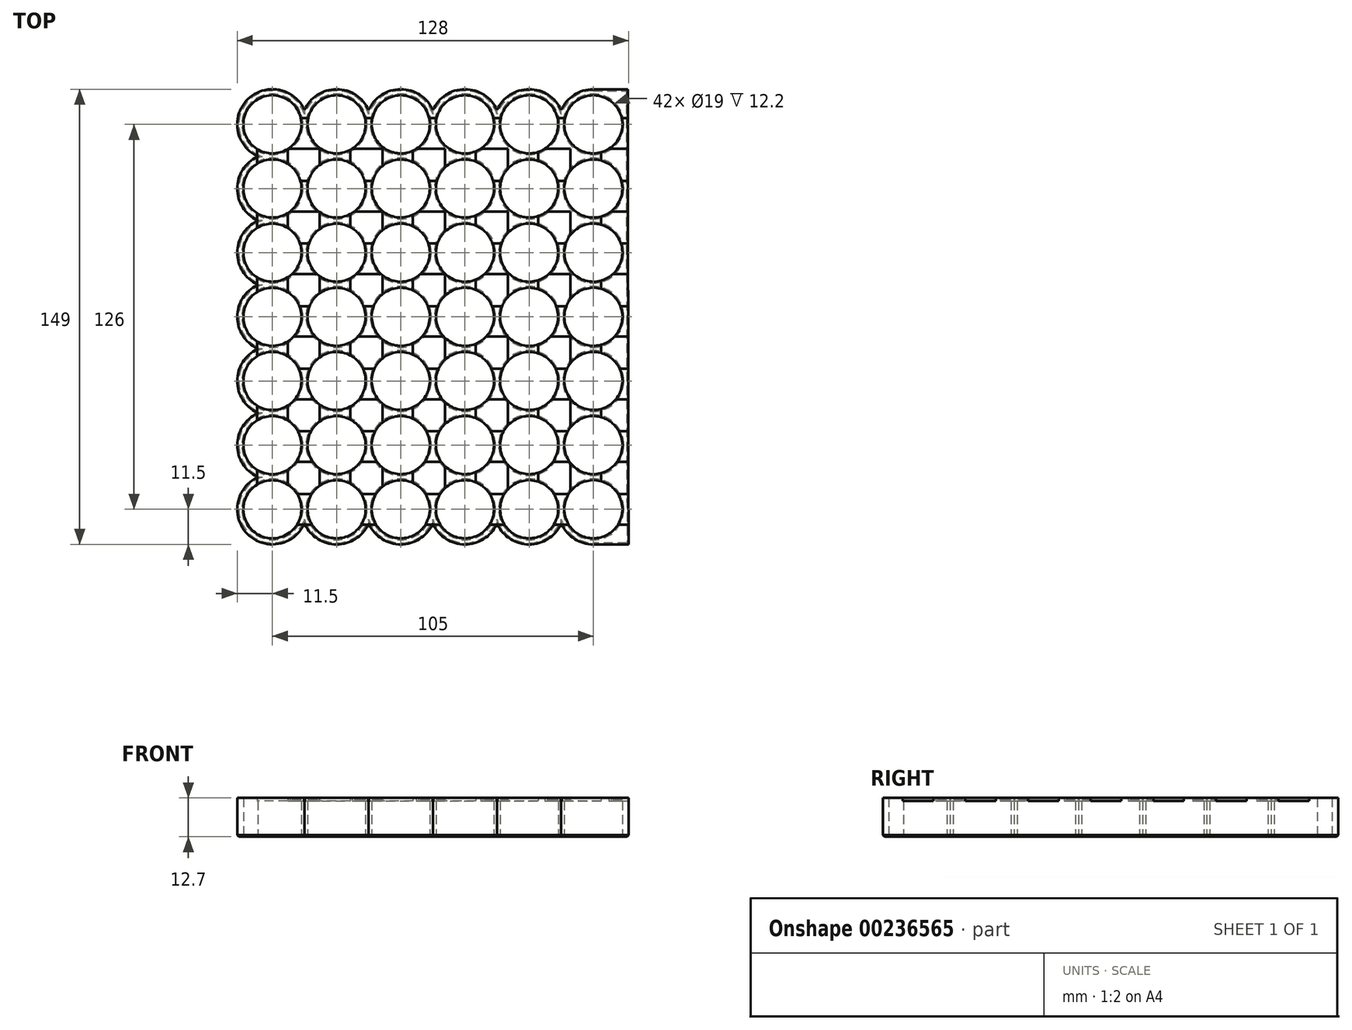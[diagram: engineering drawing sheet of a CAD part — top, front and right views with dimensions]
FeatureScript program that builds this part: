
annotation { "Feature Type Name" : "Feature", "Feature Type Description" : "" }
export const myFeature = defineFeature(function(context is Context, id is Id, definition is map)
    precondition{}
    {
        {
            var Q0;
            Q0=qCreatedBy(makeId("Top.planeOp"),FACE);
            var sketch = newSketch(context, id + "F0", { "sketchPlane" : qUnion([Q0])});
            skCircle(sketch, "E0", {"center": v(0, 0) * mm, "radius": 9.5 * mm});
            skCircle(sketch, "E1.0", {"center": v(0, 0) * mm, "radius": 11.5 * mm});
            skCircle(sketch, "E2.0.1.0", {"center": v(0, 21) * mm, "radius": 11.5 * mm});
            skCircle(sketch, "E2.0.1.1", {"center": v(0, 21) * mm, "radius": 9.5 * mm});
            skCircle(sketch, "E2.0.2.0", {"center": v(0, 42) * mm, "radius": 11.5 * mm});
            skCircle(sketch, "E2.0.2.1", {"center": v(0, 42) * mm, "radius": 9.5 * mm});
            skCircle(sketch, "E2.0.3.0", {"center": v(0, 63) * mm, "radius": 11.5 * mm});
            skCircle(sketch, "E2.0.3.1", {"center": v(0, 63) * mm, "radius": 9.5 * mm});
            skCircle(sketch, "E2.0.4.0", {"center": v(0, 84) * mm, "radius": 11.5 * mm});
            skCircle(sketch, "E2.0.4.1", {"center": v(0, 84) * mm, "radius": 9.5 * mm});
            skCircle(sketch, "E2.0.5.0", {"center": v(0, 105) * mm, "radius": 11.5 * mm});
            skCircle(sketch, "E2.0.5.1", {"center": v(0, 105) * mm, "radius": 9.5 * mm});
            skCircle(sketch, "E2.0.6.0", {"center": v(0, 126) * mm, "radius": 11.5 * mm});
            skCircle(sketch, "E2.0.6.1", {"center": v(0, 126) * mm, "radius": 9.5 * mm});
            skCircle(sketch, "E2.1.0.0", {"center": v(21, 0) * mm, "radius": 11.5 * mm});
            skCircle(sketch, "E2.1.0.1", {"center": v(21, 0) * mm, "radius": 9.5 * mm});
            skCircle(sketch, "E2.1.1.0", {"center": v(21, 21) * mm, "radius": 11.5 * mm});
            skCircle(sketch, "E2.1.1.1", {"center": v(21, 21) * mm, "radius": 9.5 * mm});
            skCircle(sketch, "E2.1.2.0", {"center": v(21, 42) * mm, "radius": 11.5 * mm});
            skCircle(sketch, "E2.1.2.1", {"center": v(21, 42) * mm, "radius": 9.5 * mm});
            skCircle(sketch, "E2.1.3.0", {"center": v(21, 63) * mm, "radius": 11.5 * mm});
            skCircle(sketch, "E2.1.3.1", {"center": v(21, 63) * mm, "radius": 9.5 * mm});
            skCircle(sketch, "E2.1.4.0", {"center": v(21, 84) * mm, "radius": 11.5 * mm});
            skCircle(sketch, "E2.1.4.1", {"center": v(21, 84) * mm, "radius": 9.5 * mm});
            skCircle(sketch, "E2.1.5.0", {"center": v(21, 105) * mm, "radius": 11.5 * mm});
            skCircle(sketch, "E2.1.5.1", {"center": v(21, 105) * mm, "radius": 9.5 * mm});
            skCircle(sketch, "E2.1.6.0", {"center": v(21, 126) * mm, "radius": 11.5 * mm});
            skCircle(sketch, "E2.1.6.1", {"center": v(21, 126) * mm, "radius": 9.5 * mm});
            skCircle(sketch, "E2.2.0.0", {"center": v(42, 0) * mm, "radius": 11.5 * mm});
            skCircle(sketch, "E2.2.0.1", {"center": v(42, 0) * mm, "radius": 9.5 * mm});
            skCircle(sketch, "E2.2.1.0", {"center": v(42, 21) * mm, "radius": 11.5 * mm});
            skCircle(sketch, "E2.2.1.1", {"center": v(42, 21) * mm, "radius": 9.5 * mm});
            skCircle(sketch, "E2.2.2.0", {"center": v(42, 42) * mm, "radius": 11.5 * mm});
            skCircle(sketch, "E2.2.2.1", {"center": v(42, 42) * mm, "radius": 9.5 * mm});
            skCircle(sketch, "E2.2.3.0", {"center": v(42, 63) * mm, "radius": 11.5 * mm});
            skCircle(sketch, "E2.2.3.1", {"center": v(42, 63) * mm, "radius": 9.5 * mm});
            skCircle(sketch, "E2.2.4.0", {"center": v(42, 84) * mm, "radius": 11.5 * mm});
            skCircle(sketch, "E2.2.4.1", {"center": v(42, 84) * mm, "radius": 9.5 * mm});
            skCircle(sketch, "E2.2.5.0", {"center": v(42, 105) * mm, "radius": 11.5 * mm});
            skCircle(sketch, "E2.2.5.1", {"center": v(42, 105) * mm, "radius": 9.5 * mm});
            skCircle(sketch, "E2.2.6.0", {"center": v(42, 126) * mm, "radius": 11.5 * mm});
            skCircle(sketch, "E2.2.6.1", {"center": v(42, 126) * mm, "radius": 9.5 * mm});
            skCircle(sketch, "E2.3.0.0", {"center": v(63, 0) * mm, "radius": 11.5 * mm});
            skCircle(sketch, "E2.3.0.1", {"center": v(63, 0) * mm, "radius": 9.5 * mm});
            skCircle(sketch, "E2.3.1.0", {"center": v(63, 21) * mm, "radius": 11.5 * mm});
            skCircle(sketch, "E2.3.1.1", {"center": v(63, 21) * mm, "radius": 9.5 * mm});
            skCircle(sketch, "E2.3.2.0", {"center": v(63, 42) * mm, "radius": 11.5 * mm});
            skCircle(sketch, "E2.3.2.1", {"center": v(63, 42) * mm, "radius": 9.5 * mm});
            skCircle(sketch, "E2.3.3.0", {"center": v(63, 63) * mm, "radius": 11.5 * mm});
            skCircle(sketch, "E2.3.3.1", {"center": v(63, 63) * mm, "radius": 9.5 * mm});
            skCircle(sketch, "E2.3.4.0", {"center": v(63, 84) * mm, "radius": 11.5 * mm});
            skCircle(sketch, "E2.3.4.1", {"center": v(63, 84) * mm, "radius": 9.5 * mm});
            skCircle(sketch, "E2.3.5.0", {"center": v(63, 105) * mm, "radius": 11.5 * mm});
            skCircle(sketch, "E2.3.5.1", {"center": v(63, 105) * mm, "radius": 9.5 * mm});
            skCircle(sketch, "E2.3.6.0", {"center": v(63, 126) * mm, "radius": 11.5 * mm});
            skCircle(sketch, "E2.3.6.1", {"center": v(63, 126) * mm, "radius": 9.5 * mm});
            skCircle(sketch, "E2.4.0.0", {"center": v(84, 0) * mm, "radius": 11.5 * mm});
            skCircle(sketch, "E2.4.0.1", {"center": v(84, 0) * mm, "radius": 9.5 * mm});
            skCircle(sketch, "E2.4.1.0", {"center": v(84, 21) * mm, "radius": 11.5 * mm});
            skCircle(sketch, "E2.4.1.1", {"center": v(84, 21) * mm, "radius": 9.5 * mm});
            skCircle(sketch, "E2.4.2.0", {"center": v(84, 42) * mm, "radius": 11.5 * mm});
            skCircle(sketch, "E2.4.2.1", {"center": v(84, 42) * mm, "radius": 9.5 * mm});
            skCircle(sketch, "E2.4.3.0", {"center": v(84, 63) * mm, "radius": 11.5 * mm});
            skCircle(sketch, "E2.4.3.1", {"center": v(84, 63) * mm, "radius": 9.5 * mm});
            skCircle(sketch, "E2.4.4.0", {"center": v(84, 84) * mm, "radius": 11.5 * mm});
            skCircle(sketch, "E2.4.4.1", {"center": v(84, 84) * mm, "radius": 9.5 * mm});
            skCircle(sketch, "E2.4.5.0", {"center": v(84, 105) * mm, "radius": 11.5 * mm});
            skCircle(sketch, "E2.4.5.1", {"center": v(84, 105) * mm, "radius": 9.5 * mm});
            skCircle(sketch, "E2.4.6.0", {"center": v(84, 126) * mm, "radius": 11.5 * mm});
            skCircle(sketch, "E2.4.6.1", {"center": v(84, 126) * mm, "radius": 9.5 * mm});
            skCircle(sketch, "E2.5.0.0", {"center": v(105, 0) * mm, "radius": 11.5 * mm});
            skCircle(sketch, "E2.5.0.1", {"center": v(105, 0) * mm, "radius": 9.5 * mm});
            skCircle(sketch, "E2.5.1.0", {"center": v(105, 21) * mm, "radius": 11.5 * mm});
            skCircle(sketch, "E2.5.1.1", {"center": v(105, 21) * mm, "radius": 9.5 * mm});
            skCircle(sketch, "E2.5.2.0", {"center": v(105, 42) * mm, "radius": 11.5 * mm});
            skCircle(sketch, "E2.5.2.1", {"center": v(105, 42) * mm, "radius": 9.5 * mm});
            skCircle(sketch, "E2.5.3.0", {"center": v(105, 63) * mm, "radius": 11.5 * mm});
            skCircle(sketch, "E2.5.3.1", {"center": v(105, 63) * mm, "radius": 9.5 * mm});
            skCircle(sketch, "E2.5.4.0", {"center": v(105, 84) * mm, "radius": 11.5 * mm});
            skCircle(sketch, "E2.5.4.1", {"center": v(105, 84) * mm, "radius": 9.5 * mm});
            skCircle(sketch, "E2.5.5.0", {"center": v(105, 105) * mm, "radius": 11.5 * mm});
            skCircle(sketch, "E2.5.5.1", {"center": v(105, 105) * mm, "radius": 9.5 * mm});
            skCircle(sketch, "E2.5.6.0", {"center": v(105, 126) * mm, "radius": 11.5 * mm});
            skCircle(sketch, "E2.5.6.1", {"center": v(105, 126) * mm, "radius": 9.5 * mm});
            skLineSegment(sketch, "E2.direction1", {"start": v(0, 0) * mm, "end": v(21, 0) * mm, "construction": true});
            skLineSegment(sketch, "E2.direction2", {"start": v(0, 0) * mm, "end": v(0, 21) * mm, "construction": true});
            skLineSegment(sketch, "E3", {"start": v(105, 0) * mm, "end": v(105, -11.5) * mm, "construction": true});
            skLineSegment(sketch, "E4", {"start": v(105, -11.5) * mm, "end": v(116.5, -11.5) * mm});
            skLineSegment(sketch, "E5", {"start": v(105, 126) * mm, "end": v(105, 137.5) * mm, "construction": true});
            skLineSegment(sketch, "E6", {"start": v(105, 137.5) * mm, "end": v(116.25, 137.5) * mm});
            skLineSegment(sketch, "E7", {"start": v(116.25, 137.5) * mm, "end": v(116.5, -11.5) * mm});
            skSolve(sketch);
        }
        {
            var Q0;
            {var subQ0=sQuery(id+"F0.wireOp",EDGE,"E2.10.4.0");var subQ1=sQuery(id+"F0.wireOp",EDGE,"E2.10.3.0");var subQ2=makeQuery(id+"F0.imprint","INTERSECT",VERTEX,{"disambiguationData":[OD(0.0)],"derivedFrom":[subQ1,subQ0]});Q0=makeQuery(id+"F0.imprint","IMPRINT",FACE,{"disambiguationData":[TD([[makeQuery(id+"F0.imprint","IMPRINT",EDGE,{"disambiguationData":[TD([[subQ2,-1.0]])],"derivedFrom":subQ1}),1.0]])]});}
            var Q1;
            {var subQ0=sQuery(id+"F0.wireOp",EDGE,"E2.1.5.0");var subQ1=sQuery(id+"F0.wireOp",EDGE,"E2.0.5.0");var subQ2=makeQuery(id+"F0.imprint","INTERSECT",VERTEX,{"disambiguationData":[OD(0.0)],"derivedFrom":[subQ1,subQ0]});Q1=makeQuery(id+"F0.imprint","IMPRINT",FACE,{"disambiguationData":[TD([[makeQuery(id+"F0.imprint","IMPRINT",EDGE,{"disambiguationData":[TD([[subQ2,-1.0]])],"derivedFrom":subQ1}),-1.0]])]});}
            var Q2;
            {var subQ0=sQuery(id+"F0.wireOp",EDGE,"E2.0.1.0");var subQ1=sQuery(id+"F0.wireOp",EDGE,"E1.0");var subQ2=makeQuery(id+"F0.imprint","INTERSECT",VERTEX,{"disambiguationData":[OD(1.0)],"derivedFrom":[subQ1,subQ0]});Q2=makeQuery(id+"F0.imprint","IMPRINT",FACE,{"disambiguationData":[TD([[makeQuery(id+"F0.imprint","IMPRINT",EDGE,{"disambiguationData":[TD([[subQ2,-1.0]])],"derivedFrom":subQ1}),-1.0]])]});}
            var Q3;
            {var subQ0=sQuery(id+"F0.wireOp",EDGE,"E2.2.3.0");var subQ1=sQuery(id+"F0.wireOp",EDGE,"E2.1.3.0");var subQ2=makeQuery(id+"F0.imprint","INTERSECT",VERTEX,{"disambiguationData":[OD(0.0)],"derivedFrom":[subQ1,subQ0]});Q3=makeQuery(id+"F0.imprint","IMPRINT",FACE,{"disambiguationData":[TD([[makeQuery(id+"F0.imprint","IMPRINT",EDGE,{"disambiguationData":[TD([[subQ2,-1.0]])],"derivedFrom":subQ1}),-1.0]])]});}
            var Q4;
            {var subQ0=sQuery(id+"F0.wireOp",EDGE,"E2.2.5.0");var subQ1=sQuery(id+"F0.wireOp",EDGE,"E2.1.5.0");var subQ2=makeQuery(id+"F0.imprint","INTERSECT",VERTEX,{"disambiguationData":[OD(0.0)],"derivedFrom":[subQ1,subQ0]});Q4=makeQuery(id+"F0.imprint","IMPRINT",FACE,{"disambiguationData":[TD([[makeQuery(id+"F0.imprint","IMPRINT",EDGE,{"disambiguationData":[TD([[subQ2,-1.0]])],"derivedFrom":subQ1}),-1.0]])]});}
            var Q5;
            {var subQ0=sQuery(id+"F0.wireOp",EDGE,"E2.3.1.0");var subQ1=sQuery(id+"F0.wireOp",EDGE,"E2.2.1.0");var subQ2=makeQuery(id+"F0.imprint","INTERSECT",VERTEX,{"disambiguationData":[OD(0.0)],"derivedFrom":[subQ1,subQ0]});Q5=makeQuery(id+"F0.imprint","IMPRINT",FACE,{"disambiguationData":[TD([[makeQuery(id+"F0.imprint","IMPRINT",EDGE,{"disambiguationData":[TD([[subQ2,-1.0]])],"derivedFrom":subQ1}),-1.0]])]});}
            var Q6;
            {var subQ0=sQuery(id+"F0.wireOp",EDGE,"E2.3.3.0");var subQ1=sQuery(id+"F0.wireOp",EDGE,"E2.2.3.0");var subQ2=makeQuery(id+"F0.imprint","INTERSECT",VERTEX,{"disambiguationData":[OD(0.0)],"derivedFrom":[subQ1,subQ0]});Q6=makeQuery(id+"F0.imprint","IMPRINT",FACE,{"disambiguationData":[TD([[makeQuery(id+"F0.imprint","IMPRINT",EDGE,{"disambiguationData":[TD([[subQ2,-1.0]])],"derivedFrom":subQ1}),-1.0]])]});}
            var Q7;
            {var subQ0=sQuery(id+"F0.wireOp",EDGE,"E2.1.3.0");var subQ1=sQuery(id+"F0.wireOp",EDGE,"E2.0.3.0");var subQ2=makeQuery(id+"F0.imprint","INTERSECT",VERTEX,{"disambiguationData":[OD(0.0)],"derivedFrom":[subQ1,subQ0]});Q7=makeQuery(id+"F0.imprint","IMPRINT",FACE,{"disambiguationData":[TD([[makeQuery(id+"F0.imprint","IMPRINT",EDGE,{"disambiguationData":[TD([[subQ2,1.0]])],"derivedFrom":subQ1}),1.0]])]});}
            var Q8;
            {var subQ0=sQuery(id+"F0.wireOp",EDGE,"E2.2.1.0");var subQ1=sQuery(id+"F0.wireOp",EDGE,"E2.1.1.0");var subQ2=makeQuery(id+"F0.imprint","INTERSECT",VERTEX,{"disambiguationData":[OD(0.0)],"derivedFrom":[subQ1,subQ0]});Q8=makeQuery(id+"F0.imprint","IMPRINT",FACE,{"disambiguationData":[TD([[makeQuery(id+"F0.imprint","IMPRINT",EDGE,{"disambiguationData":[TD([[subQ2,-1.0]])],"derivedFrom":subQ1}),-1.0]])]});}
            var Q9;
            {var subQ0=sQuery(id+"F0.wireOp",EDGE,"E2.7.6.0");var subQ1=sQuery(id+"F0.wireOp",EDGE,"E2.6.6.0");var subQ2=makeQuery(id+"F0.imprint","INTERSECT",VERTEX,{"disambiguationData":[OD(0.0)],"derivedFrom":[subQ1,subQ0]});Q9=makeQuery(id+"F0.imprint","IMPRINT",FACE,{"disambiguationData":[TD([[makeQuery(id+"F0.imprint","IMPRINT",EDGE,{"disambiguationData":[TD([[subQ2,1.0]])],"derivedFrom":subQ1}),-1.0]])]});}
            var Q10;
            {var subQ0=sQuery(id+"F0.wireOp",EDGE,"E2.11.6.0");var subQ1=sQuery(id+"F0.wireOp",EDGE,"E2.10.6.0");var subQ2=makeQuery(id+"F0.imprint","INTERSECT",VERTEX,{"disambiguationData":[OD(0.0)],"derivedFrom":[subQ1,subQ0]});Q10=makeQuery(id+"F0.imprint","IMPRINT",FACE,{"disambiguationData":[TD([[makeQuery(id+"F0.imprint","IMPRINT",EDGE,{"disambiguationData":[TD([[subQ2,1.0]])],"derivedFrom":subQ1}),-1.0]])]});}
            var Q11;
            {var subQ0=sQuery(id+"F0.wireOp",EDGE,"E2.11.3.0");var subQ1=sQuery(id+"F0.wireOp",EDGE,"E2.10.3.0");var subQ2=makeQuery(id+"F0.imprint","INTERSECT",VERTEX,{"disambiguationData":[OD(0.0)],"derivedFrom":[subQ1,subQ0]});Q11=makeQuery(id+"F0.imprint","IMPRINT",FACE,{"disambiguationData":[TD([[makeQuery(id+"F0.imprint","IMPRINT",EDGE,{"disambiguationData":[TD([[subQ2,-1.0]])],"derivedFrom":subQ1}),-1.0]])]});}
            var Q12;
            {var subQ0=sQuery(id+"F0.wireOp",EDGE,"E2.11.5.0");var subQ1=sQuery(id+"F0.wireOp",EDGE,"E2.10.5.0");var subQ2=makeQuery(id+"F0.imprint","INTERSECT",VERTEX,{"disambiguationData":[OD(0.0)],"derivedFrom":[subQ1,subQ0]});Q12=makeQuery(id+"F0.imprint","IMPRINT",FACE,{"disambiguationData":[TD([[makeQuery(id+"F0.imprint","IMPRINT",EDGE,{"disambiguationData":[TD([[subQ2,-1.0]])],"derivedFrom":subQ1}),-1.0]])]});}
            var Q13;
            {var subQ0=sQuery(id+"F0.wireOp",EDGE,"E2.9.5.0");var subQ1=sQuery(id+"F0.wireOp",EDGE,"E2.8.5.0");var subQ2=makeQuery(id+"F0.imprint","INTERSECT",VERTEX,{"disambiguationData":[OD(0.0)],"derivedFrom":[subQ1,subQ0]});Q13=makeQuery(id+"F0.imprint","IMPRINT",FACE,{"disambiguationData":[TD([[makeQuery(id+"F0.imprint","IMPRINT",EDGE,{"disambiguationData":[TD([[subQ2,-1.0]])],"derivedFrom":subQ1}),-1.0]])]});}
            var Q14;
            {var subQ0=sQuery(id+"F0.wireOp",EDGE,"E2.10.1.0");var subQ1=sQuery(id+"F0.wireOp",EDGE,"E2.9.1.0");var subQ2=makeQuery(id+"F0.imprint","INTERSECT",VERTEX,{"disambiguationData":[OD(0.0)],"derivedFrom":[subQ1,subQ0]});Q14=makeQuery(id+"F0.imprint","IMPRINT",FACE,{"disambiguationData":[TD([[makeQuery(id+"F0.imprint","IMPRINT",EDGE,{"disambiguationData":[TD([[subQ2,-1.0]])],"derivedFrom":subQ1}),-1.0]])]});}
            var Q15;
            {var subQ0=sQuery(id+"F0.wireOp",EDGE,"E2.10.3.0");var subQ1=sQuery(id+"F0.wireOp",EDGE,"E2.9.3.0");var subQ2=makeQuery(id+"F0.imprint","INTERSECT",VERTEX,{"disambiguationData":[OD(0.0)],"derivedFrom":[subQ1,subQ0]});Q15=makeQuery(id+"F0.imprint","IMPRINT",FACE,{"disambiguationData":[TD([[makeQuery(id+"F0.imprint","IMPRINT",EDGE,{"disambiguationData":[TD([[subQ2,-1.0]])],"derivedFrom":subQ1}),-1.0]])]});}
            var Q16;
            {var subQ0=sQuery(id+"F0.wireOp",EDGE,"E2.10.5.0");var subQ1=sQuery(id+"F0.wireOp",EDGE,"E2.9.5.0");var subQ2=makeQuery(id+"F0.imprint","INTERSECT",VERTEX,{"disambiguationData":[OD(0.0)],"derivedFrom":[subQ1,subQ0]});Q16=makeQuery(id+"F0.imprint","IMPRINT",FACE,{"disambiguationData":[TD([[makeQuery(id+"F0.imprint","IMPRINT",EDGE,{"disambiguationData":[TD([[subQ2,-1.0]])],"derivedFrom":subQ1}),-1.0]])]});}
            var Q17;
            {var subQ0=sQuery(id+"F0.wireOp",EDGE,"E2.8.3.0");var subQ1=sQuery(id+"F0.wireOp",EDGE,"E2.7.3.0");var subQ2=makeQuery(id+"F0.imprint","INTERSECT",VERTEX,{"disambiguationData":[OD(0.0)],"derivedFrom":[subQ1,subQ0]});Q17=makeQuery(id+"F0.imprint","IMPRINT",FACE,{"disambiguationData":[TD([[makeQuery(id+"F0.imprint","IMPRINT",EDGE,{"disambiguationData":[TD([[subQ2,-1.0]])],"derivedFrom":subQ1}),-1.0]])]});}
            var Q18;
            {var subQ0=sQuery(id+"F0.wireOp",EDGE,"E2.8.5.0");var subQ1=sQuery(id+"F0.wireOp",EDGE,"E2.7.5.0");var subQ2=makeQuery(id+"F0.imprint","INTERSECT",VERTEX,{"disambiguationData":[OD(0.0)],"derivedFrom":[subQ1,subQ0]});Q18=makeQuery(id+"F0.imprint","IMPRINT",FACE,{"disambiguationData":[TD([[makeQuery(id+"F0.imprint","IMPRINT",EDGE,{"disambiguationData":[TD([[subQ2,-1.0]])],"derivedFrom":subQ1}),-1.0]])]});}
            var Q19;
            {var subQ0=sQuery(id+"F0.wireOp",EDGE,"E2.9.1.0");var subQ1=sQuery(id+"F0.wireOp",EDGE,"E2.8.1.0");var subQ2=makeQuery(id+"F0.imprint","INTERSECT",VERTEX,{"disambiguationData":[OD(0.0)],"derivedFrom":[subQ1,subQ0]});Q19=makeQuery(id+"F0.imprint","IMPRINT",FACE,{"disambiguationData":[TD([[makeQuery(id+"F0.imprint","IMPRINT",EDGE,{"disambiguationData":[TD([[subQ2,-1.0]])],"derivedFrom":subQ1}),-1.0]])]});}
            var Q20;
            {var subQ0=sQuery(id+"F0.wireOp",EDGE,"E2.9.3.0");var subQ1=sQuery(id+"F0.wireOp",EDGE,"E2.8.3.0");var subQ2=makeQuery(id+"F0.imprint","INTERSECT",VERTEX,{"disambiguationData":[OD(0.0)],"derivedFrom":[subQ1,subQ0]});Q20=makeQuery(id+"F0.imprint","IMPRINT",FACE,{"disambiguationData":[TD([[makeQuery(id+"F0.imprint","IMPRINT",EDGE,{"disambiguationData":[TD([[subQ2,-1.0]])],"derivedFrom":subQ1}),-1.0]])]});}
            var Q21;
            {var subQ0=sQuery(id+"F0.wireOp",EDGE,"E2.7.5.0");var subQ1=sQuery(id+"F0.wireOp",EDGE,"E2.6.5.0");var subQ2=makeQuery(id+"F0.imprint","INTERSECT",VERTEX,{"disambiguationData":[OD(0.0)],"derivedFrom":[subQ1,subQ0]});Q21=makeQuery(id+"F0.imprint","IMPRINT",FACE,{"disambiguationData":[TD([[makeQuery(id+"F0.imprint","IMPRINT",EDGE,{"disambiguationData":[TD([[subQ2,-1.0]])],"derivedFrom":subQ1}),-1.0]])]});}
            var Q22;
            {var subQ0=sQuery(id+"F0.wireOp",EDGE,"E2.8.1.0");var subQ1=sQuery(id+"F0.wireOp",EDGE,"E2.7.1.0");var subQ2=makeQuery(id+"F0.imprint","INTERSECT",VERTEX,{"disambiguationData":[OD(0.0)],"derivedFrom":[subQ1,subQ0]});Q22=makeQuery(id+"F0.imprint","IMPRINT",FACE,{"disambiguationData":[TD([[makeQuery(id+"F0.imprint","IMPRINT",EDGE,{"disambiguationData":[TD([[subQ2,-1.0]])],"derivedFrom":subQ1}),-1.0]])]});}
            var Q23;
            {var subQ0=sQuery(id+"F0.wireOp",EDGE,"E2.6.3.0");var subQ1=sQuery(id+"F0.wireOp",EDGE,"E2.5.3.0");var subQ2=makeQuery(id+"F0.imprint","INTERSECT",VERTEX,{"disambiguationData":[OD(0.0)],"derivedFrom":[subQ1,subQ0]});Q23=makeQuery(id+"F0.imprint","IMPRINT",FACE,{"disambiguationData":[TD([[makeQuery(id+"F0.imprint","IMPRINT",EDGE,{"disambiguationData":[TD([[subQ2,-1.0]])],"derivedFrom":subQ1}),-1.0]])]});}
            var Q24;
            {var subQ0=sQuery(id+"F0.wireOp",EDGE,"E2.6.5.0");var subQ1=sQuery(id+"F0.wireOp",EDGE,"E2.5.5.0");var subQ2=makeQuery(id+"F0.imprint","INTERSECT",VERTEX,{"disambiguationData":[OD(0.0)],"derivedFrom":[subQ1,subQ0]});Q24=makeQuery(id+"F0.imprint","IMPRINT",FACE,{"disambiguationData":[TD([[makeQuery(id+"F0.imprint","IMPRINT",EDGE,{"disambiguationData":[TD([[subQ2,-1.0]])],"derivedFrom":subQ1}),-1.0]])]});}
            var Q25;
            {var subQ0=sQuery(id+"F0.wireOp",EDGE,"E2.7.1.0");var subQ1=sQuery(id+"F0.wireOp",EDGE,"E2.6.1.0");var subQ2=makeQuery(id+"F0.imprint","INTERSECT",VERTEX,{"disambiguationData":[OD(0.0)],"derivedFrom":[subQ1,subQ0]});Q25=makeQuery(id+"F0.imprint","IMPRINT",FACE,{"disambiguationData":[TD([[makeQuery(id+"F0.imprint","IMPRINT",EDGE,{"disambiguationData":[TD([[subQ2,-1.0]])],"derivedFrom":subQ1}),-1.0]])]});}
            var Q26;
            {var subQ0=sQuery(id+"F0.wireOp",EDGE,"E2.7.3.0");var subQ1=sQuery(id+"F0.wireOp",EDGE,"E2.6.3.0");var subQ2=makeQuery(id+"F0.imprint","INTERSECT",VERTEX,{"disambiguationData":[OD(0.0)],"derivedFrom":[subQ1,subQ0]});Q26=makeQuery(id+"F0.imprint","IMPRINT",FACE,{"disambiguationData":[TD([[makeQuery(id+"F0.imprint","IMPRINT",EDGE,{"disambiguationData":[TD([[subQ2,-1.0]])],"derivedFrom":subQ1}),-1.0]])]});}
            var Q27;
            {var subQ0=sQuery(id+"F0.wireOp",EDGE,"E2.5.1.0");var subQ1=sQuery(id+"F0.wireOp",EDGE,"E2.4.1.0");var subQ2=makeQuery(id+"F0.imprint","INTERSECT",VERTEX,{"disambiguationData":[OD(0.0)],"derivedFrom":[subQ1,subQ0]});Q27=makeQuery(id+"F0.imprint","IMPRINT",FACE,{"disambiguationData":[TD([[makeQuery(id+"F0.imprint","IMPRINT",EDGE,{"disambiguationData":[TD([[subQ2,-1.0]])],"derivedFrom":subQ1}),-1.0]])]});}
            var Q28;
            {var subQ0=sQuery(id+"F0.wireOp",EDGE,"E2.5.3.0");var subQ1=sQuery(id+"F0.wireOp",EDGE,"E2.4.3.0");var subQ2=makeQuery(id+"F0.imprint","INTERSECT",VERTEX,{"disambiguationData":[OD(0.0)],"derivedFrom":[subQ1,subQ0]});Q28=makeQuery(id+"F0.imprint","IMPRINT",FACE,{"disambiguationData":[TD([[makeQuery(id+"F0.imprint","IMPRINT",EDGE,{"disambiguationData":[TD([[subQ2,-1.0]])],"derivedFrom":subQ1}),-1.0]])]});}
            var Q29;
            {var subQ0=sQuery(id+"F0.wireOp",EDGE,"E2.5.5.0");var subQ1=sQuery(id+"F0.wireOp",EDGE,"E2.4.5.0");var subQ2=makeQuery(id+"F0.imprint","INTERSECT",VERTEX,{"disambiguationData":[OD(0.0)],"derivedFrom":[subQ1,subQ0]});Q29=makeQuery(id+"F0.imprint","IMPRINT",FACE,{"disambiguationData":[TD([[makeQuery(id+"F0.imprint","IMPRINT",EDGE,{"disambiguationData":[TD([[subQ2,-1.0]])],"derivedFrom":subQ1}),-1.0]])]});}
            var Q30;
            {var subQ0=sQuery(id+"F0.wireOp",EDGE,"E2.6.1.0");var subQ1=sQuery(id+"F0.wireOp",EDGE,"E2.5.1.0");var subQ2=makeQuery(id+"F0.imprint","INTERSECT",VERTEX,{"disambiguationData":[OD(0.0)],"derivedFrom":[subQ1,subQ0]});Q30=makeQuery(id+"F0.imprint","IMPRINT",FACE,{"disambiguationData":[TD([[makeQuery(id+"F0.imprint","IMPRINT",EDGE,{"disambiguationData":[TD([[subQ2,-1.0]])],"derivedFrom":subQ1}),-1.0]])]});}
            var Q31;
            {var subQ0=sQuery(id+"F0.wireOp",EDGE,"E2.3.5.0");var subQ1=sQuery(id+"F0.wireOp",EDGE,"E2.2.5.0");var subQ2=makeQuery(id+"F0.imprint","INTERSECT",VERTEX,{"disambiguationData":[OD(0.0)],"derivedFrom":[subQ1,subQ0]});Q31=makeQuery(id+"F0.imprint","IMPRINT",FACE,{"disambiguationData":[TD([[makeQuery(id+"F0.imprint","IMPRINT",EDGE,{"disambiguationData":[TD([[subQ2,-1.0]])],"derivedFrom":subQ1}),-1.0]])]});}
            var Q32;
            {var subQ0=sQuery(id+"F0.wireOp",EDGE,"E2.4.1.0");var subQ1=sQuery(id+"F0.wireOp",EDGE,"E2.3.1.0");var subQ2=makeQuery(id+"F0.imprint","INTERSECT",VERTEX,{"disambiguationData":[OD(0.0)],"derivedFrom":[subQ1,subQ0]});Q32=makeQuery(id+"F0.imprint","IMPRINT",FACE,{"disambiguationData":[TD([[makeQuery(id+"F0.imprint","IMPRINT",EDGE,{"disambiguationData":[TD([[subQ2,-1.0]])],"derivedFrom":subQ1}),-1.0]])]});}
            var Q33;
            {var subQ0=sQuery(id+"F0.wireOp",EDGE,"E2.4.3.0");var subQ1=sQuery(id+"F0.wireOp",EDGE,"E2.3.3.0");var subQ2=makeQuery(id+"F0.imprint","INTERSECT",VERTEX,{"disambiguationData":[OD(0.0)],"derivedFrom":[subQ1,subQ0]});Q33=makeQuery(id+"F0.imprint","IMPRINT",FACE,{"disambiguationData":[TD([[makeQuery(id+"F0.imprint","IMPRINT",EDGE,{"disambiguationData":[TD([[subQ2,-1.0]])],"derivedFrom":subQ1}),-1.0]])]});}
            var Q34;
            {var subQ0=sQuery(id+"F0.wireOp",EDGE,"E2.4.5.0");var subQ1=sQuery(id+"F0.wireOp",EDGE,"E2.3.5.0");var subQ2=makeQuery(id+"F0.imprint","INTERSECT",VERTEX,{"disambiguationData":[OD(0.0)],"derivedFrom":[subQ1,subQ0]});Q34=makeQuery(id+"F0.imprint","IMPRINT",FACE,{"disambiguationData":[TD([[makeQuery(id+"F0.imprint","IMPRINT",EDGE,{"disambiguationData":[TD([[subQ2,-1.0]])],"derivedFrom":subQ1}),-1.0]])]});}
            var Q35;
            {var subQ0=sQuery(id+"F0.wireOp",EDGE,"E2.11.1.0");var subQ1=sQuery(id+"F0.wireOp",EDGE,"E2.10.1.0");var subQ2=makeQuery(id+"F0.imprint","INTERSECT",VERTEX,{"disambiguationData":[OD(0.0)],"derivedFrom":[subQ1,subQ0]});Q35=makeQuery(id+"F0.imprint","IMPRINT",FACE,{"disambiguationData":[TD([[makeQuery(id+"F0.imprint","IMPRINT",EDGE,{"disambiguationData":[TD([[subQ2,-1.0]])],"derivedFrom":subQ1}),1.0]])]});}
            var Q36;
            {var subQ0=sQuery(id+"F0.wireOp",EDGE,"E2.1.0.0");var subQ1=sQuery(id+"F0.wireOp",EDGE,"E1.0");var subQ2=makeQuery(id+"F0.imprint","INTERSECT",VERTEX,{"disambiguationData":[OD(1.0)],"derivedFrom":[subQ1,subQ0]});Q36=makeQuery(id+"F0.imprint","IMPRINT",FACE,{"disambiguationData":[TD([[makeQuery(id+"F0.imprint","IMPRINT",EDGE,{"disambiguationData":[TD([[subQ2,-1.0]])],"derivedFrom":subQ1}),-1.0]])]});}
            var Q37;
            {var subQ0=sQuery(id+"F0.wireOp",EDGE,"E2.10.3.0");var subQ1=sQuery(id+"F0.wireOp",EDGE,"E2.9.3.0");var subQ2=makeQuery(id+"F0.imprint","INTERSECT",VERTEX,{"disambiguationData":[OD(0.0)],"derivedFrom":[subQ1,subQ0]});Q37=makeQuery(id+"F0.imprint","IMPRINT",FACE,{"disambiguationData":[TD([[makeQuery(id+"F0.imprint","IMPRINT",EDGE,{"disambiguationData":[TD([[subQ2,-1.0]])],"derivedFrom":subQ1}),1.0]])]});}
            var Q38;
            {var subQ0=sQuery(id+"F0.wireOp",EDGE,"E2.8.5.0");var subQ1=sQuery(id+"F0.wireOp",EDGE,"E2.7.5.0");var subQ2=makeQuery(id+"F0.imprint","INTERSECT",VERTEX,{"disambiguationData":[OD(0.0)],"derivedFrom":[subQ1,subQ0]});Q38=makeQuery(id+"F0.imprint","IMPRINT",FACE,{"disambiguationData":[TD([[makeQuery(id+"F0.imprint","IMPRINT",EDGE,{"disambiguationData":[TD([[subQ2,-1.0]])],"derivedFrom":subQ1}),1.0]])]});}
            var Q39;
            {var subQ0=sQuery(id+"F0.wireOp",EDGE,"E2.9.3.0");var subQ1=sQuery(id+"F0.wireOp",EDGE,"E2.8.3.0");var subQ2=makeQuery(id+"F0.imprint","INTERSECT",VERTEX,{"disambiguationData":[OD(0.0)],"derivedFrom":[subQ1,subQ0]});Q39=makeQuery(id+"F0.imprint","IMPRINT",FACE,{"disambiguationData":[TD([[makeQuery(id+"F0.imprint","IMPRINT",EDGE,{"disambiguationData":[TD([[subQ2,-1.0]])],"derivedFrom":subQ1}),1.0]])]});}
            var Q40;
            {var subQ0=sQuery(id+"F0.wireOp",EDGE,"E2.5.3.0");var subQ1=sQuery(id+"F0.wireOp",EDGE,"E2.4.3.0");var subQ2=makeQuery(id+"F0.imprint","INTERSECT",VERTEX,{"disambiguationData":[OD(0.0)],"derivedFrom":[subQ1,subQ0]});Q40=makeQuery(id+"F0.imprint","IMPRINT",FACE,{"disambiguationData":[TD([[makeQuery(id+"F0.imprint","IMPRINT",EDGE,{"disambiguationData":[TD([[subQ2,-1.0]])],"derivedFrom":subQ1}),1.0]])]});}
            var Q41;
            {var subQ0=sQuery(id+"F0.wireOp",EDGE,"E2.0.2.0");var subQ1=sQuery(id+"F0.wireOp",EDGE,"E2.0.1.0");var subQ2=makeQuery(id+"F0.imprint","INTERSECT",VERTEX,{"disambiguationData":[OD(0.0)],"derivedFrom":[subQ1,subQ0]});Q41=makeQuery(id+"F0.imprint","IMPRINT",FACE,{"disambiguationData":[TD([[makeQuery(id+"F0.imprint","IMPRINT",EDGE,{"disambiguationData":[TD([[subQ2,1.0]])],"derivedFrom":subQ1}),-1.0]])]});}
            var Q42;
            {var subQ0=sQuery(id+"F0.wireOp",EDGE,"E2.6.1.0");var subQ1=sQuery(id+"F0.wireOp",EDGE,"E2.5.1.0");var subQ2=makeQuery(id+"F0.imprint","INTERSECT",VERTEX,{"disambiguationData":[OD(0.0)],"derivedFrom":[subQ1,subQ0]});Q42=makeQuery(id+"F0.imprint","IMPRINT",FACE,{"disambiguationData":[TD([[makeQuery(id+"F0.imprint","IMPRINT",EDGE,{"disambiguationData":[TD([[subQ2,-1.0]])],"derivedFrom":subQ1}),1.0]])]});}
            var Q43;
            {var subQ0=sQuery(id+"F0.wireOp",EDGE,"E2.3.5.0");var subQ1=sQuery(id+"F0.wireOp",EDGE,"E2.2.5.0");var subQ2=makeQuery(id+"F0.imprint","INTERSECT",VERTEX,{"disambiguationData":[OD(0.0)],"derivedFrom":[subQ1,subQ0]});Q43=makeQuery(id+"F0.imprint","IMPRINT",FACE,{"disambiguationData":[TD([[makeQuery(id+"F0.imprint","IMPRINT",EDGE,{"disambiguationData":[TD([[subQ2,-1.0]])],"derivedFrom":subQ1}),1.0]])]});}
            var Q44;
            {var subQ0=sQuery(id+"F0.wireOp",EDGE,"E2.1.0.0");var subQ1=sQuery(id+"F0.wireOp",EDGE,"E1.0");var subQ2=makeQuery(id+"F0.imprint","INTERSECT",VERTEX,{"disambiguationData":[OD(0.0)],"derivedFrom":[subQ1,subQ0]});Q44=makeQuery(id+"F0.imprint","IMPRINT",FACE,{"disambiguationData":[TD([[makeQuery(id+"F0.imprint","IMPRINT",EDGE,{"disambiguationData":[TD([[subQ2,-1.0]])],"derivedFrom":subQ1}),-1.0]])]});}
            var Q45;
            {var subQ0=sQuery(id+"F0.wireOp",EDGE,"E2.4.3.0");var subQ1=sQuery(id+"F0.wireOp",EDGE,"E2.3.3.0");var subQ2=makeQuery(id+"F0.imprint","INTERSECT",VERTEX,{"disambiguationData":[OD(0.0)],"derivedFrom":[subQ1,subQ0]});Q45=makeQuery(id+"F0.imprint","IMPRINT",FACE,{"disambiguationData":[TD([[makeQuery(id+"F0.imprint","IMPRINT",EDGE,{"disambiguationData":[TD([[subQ2,-1.0]])],"derivedFrom":subQ1}),1.0]])]});}
            var Q46;
            {var subQ0=sQuery(id+"F0.wireOp",EDGE,"E2.0.1.0");var subQ1=sQuery(id+"F0.wireOp",EDGE,"E1.0");var subQ2=makeQuery(id+"F0.imprint","INTERSECT",VERTEX,{"disambiguationData":[OD(0.0)],"derivedFrom":[subQ1,subQ0]});Q46=makeQuery(id+"F0.imprint","IMPRINT",FACE,{"disambiguationData":[TD([[makeQuery(id+"F0.imprint","IMPRINT",EDGE,{"disambiguationData":[TD([[subQ2,1.0]])],"derivedFrom":subQ1}),-1.0]])]});}
            var Q47;
            {var subQ0=sQuery(id+"F0.wireOp",EDGE,"E2.0.1.0");var subQ1=sQuery(id+"F0.wireOp",EDGE,"E0");var subQ2=makeQuery(id+"F0.imprint","INTERSECT",VERTEX,{"derivedFrom":[subQ1,subQ0]});Q47=makeQuery(id+"F0.imprint","IMPRINT",FACE,{"disambiguationData":[TD([[makeQuery(id+"F0.imprint","IMPRINT",EDGE,{"disambiguationData":[TD([[subQ2,-1.0]])],"derivedFrom":subQ1}),-1.0]])]});}
            var Q48;
            {var subQ0=sQuery(id+"F0.wireOp",EDGE,"E2.11.1.0");var subQ1=sQuery(id+"F0.wireOp",EDGE,"E2.10.1.0");var subQ2=makeQuery(id+"F0.imprint","INTERSECT",VERTEX,{"disambiguationData":[OD(0.0)],"derivedFrom":[subQ1,subQ0]});Q48=makeQuery(id+"F0.imprint","IMPRINT",FACE,{"disambiguationData":[TD([[makeQuery(id+"F0.imprint","IMPRINT",EDGE,{"disambiguationData":[TD([[subQ2,1.0]])],"derivedFrom":subQ1}),-1.0]])]});}
            var Q49;
            {var subQ0=sQuery(id+"F0.wireOp",EDGE,"E2.9.5.0");var subQ1=sQuery(id+"F0.wireOp",EDGE,"E2.8.5.0");var subQ2=makeQuery(id+"F0.imprint","INTERSECT",VERTEX,{"disambiguationData":[OD(0.0)],"derivedFrom":[subQ1,subQ0]});Q49=makeQuery(id+"F0.imprint","IMPRINT",FACE,{"disambiguationData":[TD([[makeQuery(id+"F0.imprint","IMPRINT",EDGE,{"disambiguationData":[TD([[subQ2,1.0]])],"derivedFrom":subQ1}),-1.0]])]});}
            var Q50;
            {var subQ0=sQuery(id+"F0.wireOp",EDGE,"E2.0.5.0");var subQ1=sQuery(id+"F0.wireOp",EDGE,"E2.0.4.0");var subQ2=makeQuery(id+"F0.imprint","INTERSECT",VERTEX,{"disambiguationData":[OD(0.0)],"derivedFrom":[subQ1,subQ0]});Q50=makeQuery(id+"F0.imprint","IMPRINT",FACE,{"disambiguationData":[TD([[makeQuery(id+"F0.imprint","IMPRINT",EDGE,{"disambiguationData":[TD([[subQ2,1.0]])],"derivedFrom":subQ1}),-1.0]])]});}
            var Q51;
            {var subQ0=sQuery(id+"F0.wireOp",EDGE,"E2.0.6.0");var subQ1=sQuery(id+"F0.wireOp",EDGE,"E2.0.5.0");var subQ2=makeQuery(id+"F0.imprint","INTERSECT",VERTEX,{"disambiguationData":[OD(0.0)],"derivedFrom":[subQ1,subQ0]});Q51=makeQuery(id+"F0.imprint","IMPRINT",FACE,{"disambiguationData":[TD([[makeQuery(id+"F0.imprint","IMPRINT",EDGE,{"disambiguationData":[TD([[subQ2,1.0]])],"derivedFrom":subQ1}),-1.0]])]});}
            var Q52;
            {var subQ0=sQuery(id+"F0.wireOp",EDGE,"E2.11.0.0");var subQ1=sQuery(id+"F0.wireOp",EDGE,"E2.10.0.0");var subQ2=makeQuery(id+"F0.imprint","INTERSECT",VERTEX,{"disambiguationData":[OD(0.0)],"derivedFrom":[subQ1,subQ0]});Q52=makeQuery(id+"F0.imprint","IMPRINT",FACE,{"disambiguationData":[TD([[makeQuery(id+"F0.imprint","IMPRINT",EDGE,{"disambiguationData":[TD([[subQ2,-1.0]])],"derivedFrom":subQ1}),-1.0]])]});}
            var Q53;
            {var subQ0=sQuery(id+"F0.wireOp",EDGE,"E2.8.3.0");var subQ1=sQuery(id+"F0.wireOp",EDGE,"E2.7.3.0");var subQ2=makeQuery(id+"F0.imprint","INTERSECT",VERTEX,{"disambiguationData":[OD(0.0)],"derivedFrom":[subQ1,subQ0]});Q53=makeQuery(id+"F0.imprint","IMPRINT",FACE,{"disambiguationData":[TD([[makeQuery(id+"F0.imprint","IMPRINT",EDGE,{"disambiguationData":[TD([[subQ2,1.0]])],"derivedFrom":subQ1}),-1.0]])]});}
            var Q54;
            {var subQ0=sQuery(id+"F0.wireOp",EDGE,"E2.8.5.0");var subQ1=sQuery(id+"F0.wireOp",EDGE,"E2.7.5.0");var subQ2=makeQuery(id+"F0.imprint","INTERSECT",VERTEX,{"disambiguationData":[OD(0.0)],"derivedFrom":[subQ1,subQ0]});Q54=makeQuery(id+"F0.imprint","IMPRINT",FACE,{"disambiguationData":[TD([[makeQuery(id+"F0.imprint","IMPRINT",EDGE,{"disambiguationData":[TD([[subQ2,1.0]])],"derivedFrom":subQ1}),-1.0]])]});}
            var Q55;
            {var subQ0=sQuery(id+"F0.wireOp",EDGE,"E2.7.3.0");var subQ1=sQuery(id+"F0.wireOp",EDGE,"E2.6.3.0");var subQ2=makeQuery(id+"F0.imprint","INTERSECT",VERTEX,{"disambiguationData":[OD(0.0)],"derivedFrom":[subQ1,subQ0]});Q55=makeQuery(id+"F0.imprint","IMPRINT",FACE,{"disambiguationData":[TD([[makeQuery(id+"F0.imprint","IMPRINT",EDGE,{"disambiguationData":[TD([[subQ2,1.0]])],"derivedFrom":subQ1}),-1.0]])]});}
            var Q56;
            {var subQ0=sQuery(id+"F0.wireOp",EDGE,"E2.5.5.0");var subQ1=sQuery(id+"F0.wireOp",EDGE,"E2.4.5.0");var subQ2=makeQuery(id+"F0.imprint","INTERSECT",VERTEX,{"disambiguationData":[OD(0.0)],"derivedFrom":[subQ1,subQ0]});Q56=makeQuery(id+"F0.imprint","IMPRINT",FACE,{"disambiguationData":[TD([[makeQuery(id+"F0.imprint","IMPRINT",EDGE,{"disambiguationData":[TD([[subQ2,1.0]])],"derivedFrom":subQ1}),-1.0]])]});}
            var Q57;
            {var subQ0=sQuery(id+"F0.wireOp",EDGE,"E2.6.1.0");var subQ1=sQuery(id+"F0.wireOp",EDGE,"E2.5.1.0");var subQ2=makeQuery(id+"F0.imprint","INTERSECT",VERTEX,{"disambiguationData":[OD(0.0)],"derivedFrom":[subQ1,subQ0]});Q57=makeQuery(id+"F0.imprint","IMPRINT",FACE,{"disambiguationData":[TD([[makeQuery(id+"F0.imprint","IMPRINT",EDGE,{"disambiguationData":[TD([[subQ2,1.0]])],"derivedFrom":subQ1}),-1.0]])]});}
            var Q58;
            {var subQ0=sQuery(id+"F0.wireOp",EDGE,"E2.4.5.0");var subQ1=sQuery(id+"F0.wireOp",EDGE,"E2.3.5.0");var subQ2=makeQuery(id+"F0.imprint","INTERSECT",VERTEX,{"disambiguationData":[OD(0.0)],"derivedFrom":[subQ1,subQ0]});Q58=makeQuery(id+"F0.imprint","IMPRINT",FACE,{"disambiguationData":[TD([[makeQuery(id+"F0.imprint","IMPRINT",EDGE,{"disambiguationData":[TD([[subQ2,1.0]])],"derivedFrom":subQ1}),-1.0]])]});}
            var Q59;
            {var subQ0=sQuery(id+"F0.wireOp",EDGE,"E2.3.3.0");var subQ1=sQuery(id+"F0.wireOp",EDGE,"E2.2.3.0");var subQ2=makeQuery(id+"F0.imprint","INTERSECT",VERTEX,{"disambiguationData":[OD(0.0)],"derivedFrom":[subQ1,subQ0]});Q59=makeQuery(id+"F0.imprint","IMPRINT",FACE,{"disambiguationData":[TD([[makeQuery(id+"F0.imprint","IMPRINT",EDGE,{"disambiguationData":[TD([[subQ2,1.0]])],"derivedFrom":subQ1}),-1.0]])]});}
            var Q60;
            {var subQ0=sQuery(id+"F0.wireOp",EDGE,"E2.1.5.0");var subQ1=sQuery(id+"F0.wireOp",EDGE,"E2.0.5.0");var subQ2=makeQuery(id+"F0.imprint","INTERSECT",VERTEX,{"disambiguationData":[OD(0.0)],"derivedFrom":[subQ1,subQ0]});Q60=makeQuery(id+"F0.imprint","IMPRINT",FACE,{"disambiguationData":[TD([[makeQuery(id+"F0.imprint","IMPRINT",EDGE,{"disambiguationData":[TD([[subQ2,1.0]])],"derivedFrom":subQ1}),1.0]])]});}
            var Q61;
            {var subQ0=sQuery(id+"F0.wireOp",EDGE,"E2.11.5.0");var subQ1=sQuery(id+"F0.wireOp",EDGE,"E2.10.5.0");var subQ2=makeQuery(id+"F0.imprint","INTERSECT",VERTEX,{"disambiguationData":[OD(0.0)],"derivedFrom":[subQ1,subQ0]});Q61=makeQuery(id+"F0.imprint","IMPRINT",FACE,{"disambiguationData":[TD([[makeQuery(id+"F0.imprint","IMPRINT",EDGE,{"disambiguationData":[TD([[subQ2,1.0]])],"derivedFrom":subQ1}),1.0]])]});}
            var Q62;
            {var subQ0=sQuery(id+"F0.wireOp",EDGE,"E2.11.1.0");var subQ1=sQuery(id+"F0.wireOp",EDGE,"E2.10.1.0");var subQ2=makeQuery(id+"F0.imprint","INTERSECT",VERTEX,{"disambiguationData":[OD(0.0)],"derivedFrom":[subQ1,subQ0]});Q62=makeQuery(id+"F0.imprint","IMPRINT",FACE,{"disambiguationData":[TD([[makeQuery(id+"F0.imprint","IMPRINT",EDGE,{"disambiguationData":[TD([[subQ2,1.0]])],"derivedFrom":subQ1}),1.0]])]});}
            var Q63;
            {var subQ0=sQuery(id+"F0.wireOp",EDGE,"E2.11.3.0");var subQ1=sQuery(id+"F0.wireOp",EDGE,"E2.10.3.0");var subQ2=makeQuery(id+"F0.imprint","INTERSECT",VERTEX,{"disambiguationData":[OD(0.0)],"derivedFrom":[subQ1,subQ0]});Q63=makeQuery(id+"F0.imprint","IMPRINT",FACE,{"disambiguationData":[TD([[makeQuery(id+"F0.imprint","IMPRINT",EDGE,{"disambiguationData":[TD([[subQ2,1.0]])],"derivedFrom":subQ1}),1.0]])]});}
            var Q64;
            {var subQ0=sQuery(id+"F0.wireOp",EDGE,"E2.6.1.0");var subQ1=sQuery(id+"F0.wireOp",EDGE,"E2.5.1.0");var subQ2=makeQuery(id+"F0.imprint","INTERSECT",VERTEX,{"disambiguationData":[OD(0.0)],"derivedFrom":[subQ1,subQ0]});Q64=makeQuery(id+"F0.imprint","IMPRINT",FACE,{"disambiguationData":[TD([[makeQuery(id+"F0.imprint","IMPRINT",EDGE,{"disambiguationData":[TD([[subQ2,1.0]])],"derivedFrom":subQ1}),1.0]])]});}
            var Q65;
            {var subQ0=sQuery(id+"F0.wireOp",EDGE,"E2.6.3.0");var subQ1=sQuery(id+"F0.wireOp",EDGE,"E2.5.3.0");var subQ2=makeQuery(id+"F0.imprint","INTERSECT",VERTEX,{"disambiguationData":[OD(0.0)],"derivedFrom":[subQ1,subQ0]});Q65=makeQuery(id+"F0.imprint","IMPRINT",FACE,{"disambiguationData":[TD([[makeQuery(id+"F0.imprint","IMPRINT",EDGE,{"disambiguationData":[TD([[subQ2,1.0]])],"derivedFrom":subQ1}),1.0]])]});}
            var Q66;
            {var subQ0=sQuery(id+"F0.wireOp",EDGE,"E2.6.5.0");var subQ1=sQuery(id+"F0.wireOp",EDGE,"E2.5.5.0");var subQ2=makeQuery(id+"F0.imprint","INTERSECT",VERTEX,{"disambiguationData":[OD(0.0)],"derivedFrom":[subQ1,subQ0]});Q66=makeQuery(id+"F0.imprint","IMPRINT",FACE,{"disambiguationData":[TD([[makeQuery(id+"F0.imprint","IMPRINT",EDGE,{"disambiguationData":[TD([[subQ2,1.0]])],"derivedFrom":subQ1}),1.0]])]});}
            var Q67;
            {var subQ0=sQuery(id+"F0.wireOp",EDGE,"E2.10.1.0");var subQ1=sQuery(id+"F0.wireOp",EDGE,"E2.10.0.0");var subQ2=makeQuery(id+"F0.imprint","INTERSECT",VERTEX,{"disambiguationData":[OD(0.0)],"derivedFrom":[subQ1,subQ0]});Q67=makeQuery(id+"F0.imprint","IMPRINT",FACE,{"disambiguationData":[TD([[makeQuery(id+"F0.imprint","IMPRINT",EDGE,{"disambiguationData":[TD([[subQ2,-1.0]])],"derivedFrom":subQ1}),-1.0]])]});}
            var Q68;
            {var subQ0=sQuery(id+"F0.wireOp",EDGE,"E2.5.1.0");var subQ1=sQuery(id+"F0.wireOp",EDGE,"E2.5.0.0");var subQ2=makeQuery(id+"F0.imprint","INTERSECT",VERTEX,{"disambiguationData":[OD(0.0)],"derivedFrom":[subQ1,subQ0]});Q68=makeQuery(id+"F0.imprint","IMPRINT",FACE,{"disambiguationData":[TD([[makeQuery(id+"F0.imprint","IMPRINT",EDGE,{"disambiguationData":[TD([[subQ2,-1.0]])],"derivedFrom":subQ1}),-1.0]])]});}
            var Q69;
            {var subQ0=sQuery(id+"F0.wireOp",EDGE,"E2.6.6.0");var subQ1=sQuery(id+"F0.wireOp",EDGE,"E2.5.6.0");var subQ2=makeQuery(id+"F0.imprint","INTERSECT",VERTEX,{"disambiguationData":[OD(0.0)],"derivedFrom":[subQ1,subQ0]});Q69=makeQuery(id+"F0.imprint","IMPRINT",FACE,{"disambiguationData":[TD([[makeQuery(id+"F0.imprint","IMPRINT",EDGE,{"disambiguationData":[TD([[subQ2,1.0]])],"derivedFrom":subQ1}),-1.0]])]});}
            var Q70;
            {var subQ0=sQuery(id+"F0.wireOp",EDGE,"E2.10.6.0");var subQ1=sQuery(id+"F0.wireOp",EDGE,"E2.9.6.0");var subQ2=makeQuery(id+"F0.imprint","INTERSECT",VERTEX,{"disambiguationData":[OD(0.0)],"derivedFrom":[subQ1,subQ0]});Q70=makeQuery(id+"F0.imprint","IMPRINT",FACE,{"disambiguationData":[TD([[makeQuery(id+"F0.imprint","IMPRINT",EDGE,{"disambiguationData":[TD([[subQ2,1.0]])],"derivedFrom":subQ1}),-1.0]])]});}
            var Q71;
            {var subQ0=sQuery(id+"F0.wireOp",EDGE,"E2.1.2.0");var subQ1=sQuery(id+"F0.wireOp",EDGE,"E2.0.2.0");var subQ2=makeQuery(id+"F0.imprint","INTERSECT",VERTEX,{"disambiguationData":[OD(0.0)],"derivedFrom":[subQ1,subQ0]});Q71=makeQuery(id+"F0.imprint","IMPRINT",FACE,{"disambiguationData":[TD([[makeQuery(id+"F0.imprint","IMPRINT",EDGE,{"disambiguationData":[TD([[subQ2,-1.0]])],"derivedFrom":subQ1}),-1.0]])]});}
            var Q72;
            {var subQ0=sQuery(id+"F0.wireOp",EDGE,"E2.7.4.1");var subQ1=sQuery(id+"F0.wireOp",EDGE,"E2.6.4.0");var subQ2=makeQuery(id+"F0.imprint","INTERSECT",VERTEX,{"derivedFrom":[subQ1,subQ0]});Q72=makeQuery(id+"F0.imprint","IMPRINT",FACE,{"disambiguationData":[TD([[makeQuery(id+"F0.imprint","IMPRINT",EDGE,{"disambiguationData":[TD([[subQ2,1.0]])],"derivedFrom":subQ1}),-1.0]])]});}
            var Q73;
            {var subQ0=sQuery(id+"F0.wireOp",EDGE,"E2.9.5.0");var subQ1=sQuery(id+"F0.wireOp",EDGE,"E2.9.4.0");var subQ2=makeQuery(id+"F0.imprint","INTERSECT",VERTEX,{"disambiguationData":[OD(0.0)],"derivedFrom":[subQ1,subQ0]});Q73=makeQuery(id+"F0.imprint","IMPRINT",FACE,{"disambiguationData":[TD([[makeQuery(id+"F0.imprint","IMPRINT",EDGE,{"disambiguationData":[TD([[subQ2,-1.0]])],"derivedFrom":subQ1}),-1.0]])]});}
            var Q74;
            {var subQ0=sQuery(id+"F0.wireOp",EDGE,"E2.9.0.0");var subQ1=sQuery(id+"F0.wireOp",EDGE,"E2.8.0.0");var subQ2=makeQuery(id+"F0.imprint","INTERSECT",VERTEX,{"disambiguationData":[OD(1.0)],"derivedFrom":[subQ1,subQ0]});Q74=makeQuery(id+"F0.imprint","IMPRINT",FACE,{"disambiguationData":[TD([[makeQuery(id+"F0.imprint","IMPRINT",EDGE,{"disambiguationData":[TD([[subQ2,-1.0]])],"derivedFrom":subQ1}),-1.0]])]});}
            var Q75;
            {var subQ0=sQuery(id+"F0.wireOp",EDGE,"E2.8.3.0");var subQ1=sQuery(id+"F0.wireOp",EDGE,"E2.8.2.0");var subQ2=makeQuery(id+"F0.imprint","INTERSECT",VERTEX,{"disambiguationData":[OD(0.0)],"derivedFrom":[subQ1,subQ0]});Q75=makeQuery(id+"F0.imprint","IMPRINT",FACE,{"disambiguationData":[TD([[makeQuery(id+"F0.imprint","IMPRINT",EDGE,{"disambiguationData":[TD([[subQ2,-1.0]])],"derivedFrom":subQ1}),-1.0]])]});}
            var Q76;
            {var subQ0=sQuery(id+"F0.wireOp",EDGE,"E2.8.5.0");var subQ1=sQuery(id+"F0.wireOp",EDGE,"E2.8.4.0");var subQ2=makeQuery(id+"F0.imprint","INTERSECT",VERTEX,{"disambiguationData":[OD(0.0)],"derivedFrom":[subQ1,subQ0]});Q76=makeQuery(id+"F0.imprint","IMPRINT",FACE,{"disambiguationData":[TD([[makeQuery(id+"F0.imprint","IMPRINT",EDGE,{"disambiguationData":[TD([[subQ2,-1.0]])],"derivedFrom":subQ1}),-1.0]])]});}
            var Q77;
            {var subQ0=sQuery(id+"F0.wireOp",EDGE,"E2.10.0.0");var subQ1=sQuery(id+"F0.wireOp",EDGE,"E2.9.0.0");var subQ2=makeQuery(id+"F0.imprint","INTERSECT",VERTEX,{"disambiguationData":[OD(1.0)],"derivedFrom":[subQ1,subQ0]});Q77=makeQuery(id+"F0.imprint","IMPRINT",FACE,{"disambiguationData":[TD([[makeQuery(id+"F0.imprint","IMPRINT",EDGE,{"disambiguationData":[TD([[subQ2,-1.0]])],"derivedFrom":subQ1}),-1.0]])]});}
            var Q78;
            {var subQ0=sQuery(id+"F0.wireOp",EDGE,"E2.7.3.0");var subQ1=sQuery(id+"F0.wireOp",EDGE,"E2.7.2.0");var subQ2=makeQuery(id+"F0.imprint","INTERSECT",VERTEX,{"disambiguationData":[OD(0.0)],"derivedFrom":[subQ1,subQ0]});Q78=makeQuery(id+"F0.imprint","IMPRINT",FACE,{"disambiguationData":[TD([[makeQuery(id+"F0.imprint","IMPRINT",EDGE,{"disambiguationData":[TD([[subQ2,-1.0]])],"derivedFrom":subQ1}),-1.0]])]});}
            var Q79;
            {var subQ0=sQuery(id+"F0.wireOp",EDGE,"E2.7.0.0");var subQ1=sQuery(id+"F0.wireOp",EDGE,"E2.6.0.0");var subQ2=makeQuery(id+"F0.imprint","INTERSECT",VERTEX,{"disambiguationData":[OD(1.0)],"derivedFrom":[subQ1,subQ0]});Q79=makeQuery(id+"F0.imprint","IMPRINT",FACE,{"disambiguationData":[TD([[makeQuery(id+"F0.imprint","IMPRINT",EDGE,{"disambiguationData":[TD([[subQ2,-1.0]])],"derivedFrom":subQ1}),-1.0]])]});}
            var Q80;
            {var subQ0=sQuery(id+"F0.wireOp",EDGE,"E2.8.0.0");var subQ1=sQuery(id+"F0.wireOp",EDGE,"E2.7.0.0");var subQ2=makeQuery(id+"F0.imprint","INTERSECT",VERTEX,{"disambiguationData":[OD(1.0)],"derivedFrom":[subQ1,subQ0]});Q80=makeQuery(id+"F0.imprint","IMPRINT",FACE,{"disambiguationData":[TD([[makeQuery(id+"F0.imprint","IMPRINT",EDGE,{"disambiguationData":[TD([[subQ2,-1.0]])],"derivedFrom":subQ1}),-1.0]])]});}
            var Q81;
            {var subQ0=sQuery(id+"F0.wireOp",EDGE,"E2.4.5.0");var subQ1=sQuery(id+"F0.wireOp",EDGE,"E2.4.4.0");var subQ2=makeQuery(id+"F0.imprint","INTERSECT",VERTEX,{"disambiguationData":[OD(0.0)],"derivedFrom":[subQ1,subQ0]});Q81=makeQuery(id+"F0.imprint","IMPRINT",FACE,{"disambiguationData":[TD([[makeQuery(id+"F0.imprint","IMPRINT",EDGE,{"disambiguationData":[TD([[subQ2,-1.0]])],"derivedFrom":subQ1}),-1.0]])]});}
            var Q82;
            {var subQ0=sQuery(id+"F0.wireOp",EDGE,"E2.6.0.0");var subQ1=sQuery(id+"F0.wireOp",EDGE,"E2.5.0.0");var subQ2=makeQuery(id+"F0.imprint","INTERSECT",VERTEX,{"disambiguationData":[OD(1.0)],"derivedFrom":[subQ1,subQ0]});Q82=makeQuery(id+"F0.imprint","IMPRINT",FACE,{"disambiguationData":[TD([[makeQuery(id+"F0.imprint","IMPRINT",EDGE,{"disambiguationData":[TD([[subQ2,-1.0]])],"derivedFrom":subQ1}),-1.0]])]});}
            var Q83;
            {var subQ0=sQuery(id+"F0.wireOp",EDGE,"E2.5.0.0");var subQ1=sQuery(id+"F0.wireOp",EDGE,"E2.4.0.0");var subQ2=makeQuery(id+"F0.imprint","INTERSECT",VERTEX,{"disambiguationData":[OD(1.0)],"derivedFrom":[subQ1,subQ0]});Q83=makeQuery(id+"F0.imprint","IMPRINT",FACE,{"disambiguationData":[TD([[makeQuery(id+"F0.imprint","IMPRINT",EDGE,{"disambiguationData":[TD([[subQ2,-1.0]])],"derivedFrom":subQ1}),-1.0]])]});}
            var Q84;
            {var subQ0=sQuery(id+"F0.wireOp",EDGE,"E2.4.3.0");var subQ1=sQuery(id+"F0.wireOp",EDGE,"E2.4.2.0");var subQ2=makeQuery(id+"F0.imprint","INTERSECT",VERTEX,{"disambiguationData":[OD(0.0)],"derivedFrom":[subQ1,subQ0]});Q84=makeQuery(id+"F0.imprint","IMPRINT",FACE,{"disambiguationData":[TD([[makeQuery(id+"F0.imprint","IMPRINT",EDGE,{"disambiguationData":[TD([[subQ2,-1.0]])],"derivedFrom":subQ1}),-1.0]])]});}
            var Q85;
            {var subQ0=sQuery(id+"F0.wireOp",EDGE,"E2.3.0.0");var subQ1=sQuery(id+"F0.wireOp",EDGE,"E2.2.0.0");var subQ2=makeQuery(id+"F0.imprint","INTERSECT",VERTEX,{"disambiguationData":[OD(1.0)],"derivedFrom":[subQ1,subQ0]});Q85=makeQuery(id+"F0.imprint","IMPRINT",FACE,{"disambiguationData":[TD([[makeQuery(id+"F0.imprint","IMPRINT",EDGE,{"disambiguationData":[TD([[subQ2,-1.0]])],"derivedFrom":subQ1}),-1.0]])]});}
            var Q86;
            {var subQ0=sQuery(id+"F0.wireOp",EDGE,"E2.2.3.0");var subQ1=sQuery(id+"F0.wireOp",EDGE,"E2.2.2.0");var subQ2=makeQuery(id+"F0.imprint","INTERSECT",VERTEX,{"disambiguationData":[OD(0.0)],"derivedFrom":[subQ1,subQ0]});Q86=makeQuery(id+"F0.imprint","IMPRINT",FACE,{"disambiguationData":[TD([[makeQuery(id+"F0.imprint","IMPRINT",EDGE,{"disambiguationData":[TD([[subQ2,-1.0]])],"derivedFrom":subQ1}),-1.0]])]});}
            var Q87;
            {var subQ0=sQuery(id+"F0.wireOp",EDGE,"E2.4.0.0");var subQ1=sQuery(id+"F0.wireOp",EDGE,"E2.3.0.0");var subQ2=makeQuery(id+"F0.imprint","INTERSECT",VERTEX,{"disambiguationData":[OD(1.0)],"derivedFrom":[subQ1,subQ0]});Q87=makeQuery(id+"F0.imprint","IMPRINT",FACE,{"disambiguationData":[TD([[makeQuery(id+"F0.imprint","IMPRINT",EDGE,{"disambiguationData":[TD([[subQ2,-1.0]])],"derivedFrom":subQ1}),-1.0]])]});}
            var Q88;
            {var subQ0=sQuery(id+"F0.wireOp",EDGE,"E2.1.4.0");var subQ1=sQuery(id+"F0.wireOp",EDGE,"E2.0.4.0");var subQ2=makeQuery(id+"F0.imprint","INTERSECT",VERTEX,{"disambiguationData":[OD(0.0)],"derivedFrom":[subQ1,subQ0]});Q88=makeQuery(id+"F0.imprint","IMPRINT",FACE,{"disambiguationData":[TD([[makeQuery(id+"F0.imprint","IMPRINT",EDGE,{"disambiguationData":[TD([[subQ2,-1.0]])],"derivedFrom":subQ1}),-1.0]])]});}
            var Q89;
            {var subQ0=sQuery(id+"F0.wireOp",EDGE,"E2.2.0.0");var subQ1=sQuery(id+"F0.wireOp",EDGE,"E2.1.0.0");var subQ2=makeQuery(id+"F0.imprint","INTERSECT",VERTEX,{"disambiguationData":[OD(1.0)],"derivedFrom":[subQ1,subQ0]});Q89=makeQuery(id+"F0.imprint","IMPRINT",FACE,{"disambiguationData":[TD([[makeQuery(id+"F0.imprint","IMPRINT",EDGE,{"disambiguationData":[TD([[subQ2,-1.0]])],"derivedFrom":subQ1}),-1.0]])]});}
            var Q90;
            {var subQ0=sQuery(id+"F0.wireOp",EDGE,"E2.6.0.0");var subQ1=sQuery(id+"F0.wireOp",EDGE,"E2.5.0.0");var subQ2=makeQuery(id+"F0.imprint","INTERSECT",VERTEX,{"disambiguationData":[OD(0.0)],"derivedFrom":[subQ1,subQ0]});Q90=makeQuery(id+"F0.imprint","IMPRINT",FACE,{"disambiguationData":[TD([[makeQuery(id+"F0.imprint","IMPRINT",EDGE,{"disambiguationData":[TD([[subQ2,-1.0]])],"derivedFrom":subQ1}),-1.0]])]});}
            var Q91;
            {var subQ0=sQuery(id+"F0.wireOp",EDGE,"E2.10.0.0");var subQ1=sQuery(id+"F0.wireOp",EDGE,"E2.9.0.0");var subQ2=makeQuery(id+"F0.imprint","INTERSECT",VERTEX,{"disambiguationData":[OD(0.0)],"derivedFrom":[subQ1,subQ0]});Q91=makeQuery(id+"F0.imprint","IMPRINT",FACE,{"disambiguationData":[TD([[makeQuery(id+"F0.imprint","IMPRINT",EDGE,{"disambiguationData":[TD([[subQ2,-1.0]])],"derivedFrom":subQ1}),-1.0]])]});}
            var Q92;
            {var subQ0=sQuery(id+"F0.wireOp",EDGE,"E2.7.0.0");var subQ1=sQuery(id+"F0.wireOp",EDGE,"E2.6.0.0");var subQ2=makeQuery(id+"F0.imprint","INTERSECT",VERTEX,{"disambiguationData":[OD(1.0)],"derivedFrom":[subQ1,subQ0]});Q92=makeQuery(id+"F0.imprint","IMPRINT",FACE,{"disambiguationData":[TD([[makeQuery(id+"F0.imprint","IMPRINT",EDGE,{"disambiguationData":[TD([[subQ2,-1.0]])],"derivedFrom":subQ1}),1.0]])]});}
            var Q93;
            {var subQ0=sQuery(id+"F0.wireOp",EDGE,"E2.3.0.0");var subQ1=sQuery(id+"F0.wireOp",EDGE,"E2.2.0.0");var subQ2=makeQuery(id+"F0.imprint","INTERSECT",VERTEX,{"disambiguationData":[OD(1.0)],"derivedFrom":[subQ1,subQ0]});Q93=makeQuery(id+"F0.imprint","IMPRINT",FACE,{"disambiguationData":[TD([[makeQuery(id+"F0.imprint","IMPRINT",EDGE,{"disambiguationData":[TD([[subQ2,-1.0]])],"derivedFrom":subQ1}),1.0]])]});}
            var Q94;
            {var subQ0=sQuery(id+"F0.wireOp",EDGE,"E2.11.5.0");var subQ1=sQuery(id+"F0.wireOp",EDGE,"E2.11.4.0");var subQ2=makeQuery(id+"F0.imprint","INTERSECT",VERTEX,{"disambiguationData":[OD(0.0)],"derivedFrom":[subQ1,subQ0]});Q94=makeQuery(id+"F0.imprint","IMPRINT",FACE,{"disambiguationData":[TD([[makeQuery(id+"F0.imprint","IMPRINT",EDGE,{"disambiguationData":[TD([[subQ2,-1.0]])],"derivedFrom":subQ1}),-1.0]])]});}
            var Q95;
            {var subQ0=sQuery(id+"F0.wireOp",EDGE,"E2.1.2.0");var subQ1=sQuery(id+"F0.wireOp",EDGE,"E2.0.2.0");var subQ2=makeQuery(id+"F0.imprint","INTERSECT",VERTEX,{"disambiguationData":[OD(0.0)],"derivedFrom":[subQ1,subQ0]});Q95=makeQuery(id+"F0.imprint","IMPRINT",FACE,{"disambiguationData":[TD([[makeQuery(id+"F0.imprint","IMPRINT",EDGE,{"disambiguationData":[TD([[subQ2,1.0]])],"derivedFrom":subQ1}),1.0]])]});}
            var Q96;
            {var subQ0=sQuery(id+"F0.wireOp",EDGE,"E2.1.6.0");var subQ1=sQuery(id+"F0.wireOp",EDGE,"E2.0.6.0");var subQ2=makeQuery(id+"F0.imprint","INTERSECT",VERTEX,{"disambiguationData":[OD(0.0)],"derivedFrom":[subQ1,subQ0]});Q96=makeQuery(id+"F0.imprint","IMPRINT",FACE,{"disambiguationData":[TD([[makeQuery(id+"F0.imprint","IMPRINT",EDGE,{"disambiguationData":[TD([[subQ2,1.0]])],"derivedFrom":subQ1}),-1.0]])]});}
            var Q97;
            {var subQ0=sQuery(id+"F0.wireOp",EDGE,"E2.9.0.0");var subQ1=sQuery(id+"F0.wireOp",EDGE,"E2.8.0.0");var subQ2=makeQuery(id+"F0.imprint","INTERSECT",VERTEX,{"disambiguationData":[OD(1.0)],"derivedFrom":[subQ1,subQ0]});Q97=makeQuery(id+"F0.imprint","IMPRINT",FACE,{"disambiguationData":[TD([[makeQuery(id+"F0.imprint","IMPRINT",EDGE,{"disambiguationData":[TD([[subQ2,1.0]])],"derivedFrom":subQ1}),-1.0]])]});}
            var Q98;
            {var subQ0=sQuery(id+"F0.wireOp",EDGE,"E2.9.2.0");var subQ1=sQuery(id+"F0.wireOp",EDGE,"E2.8.2.0");var subQ2=makeQuery(id+"F0.imprint","INTERSECT",VERTEX,{"disambiguationData":[OD(0.0)],"derivedFrom":[subQ1,subQ0]});Q98=makeQuery(id+"F0.imprint","IMPRINT",FACE,{"disambiguationData":[TD([[makeQuery(id+"F0.imprint","IMPRINT",EDGE,{"disambiguationData":[TD([[subQ2,-1.0]])],"derivedFrom":subQ1}),-1.0]])]});}
            var Q99;
            {var subQ0=sQuery(id+"F0.wireOp",EDGE,"E2.9.4.0");var subQ1=sQuery(id+"F0.wireOp",EDGE,"E2.8.4.0");var subQ2=makeQuery(id+"F0.imprint","INTERSECT",VERTEX,{"disambiguationData":[OD(0.0)],"derivedFrom":[subQ1,subQ0]});Q99=makeQuery(id+"F0.imprint","IMPRINT",FACE,{"disambiguationData":[TD([[makeQuery(id+"F0.imprint","IMPRINT",EDGE,{"disambiguationData":[TD([[subQ2,-1.0]])],"derivedFrom":subQ1}),-1.0]])]});}
            var Q100;
            {var subQ0=sQuery(id+"F0.wireOp",EDGE,"E2.10.0.0");var subQ1=sQuery(id+"F0.wireOp",EDGE,"E2.9.0.0");var subQ2=makeQuery(id+"F0.imprint","INTERSECT",VERTEX,{"disambiguationData":[OD(1.0)],"derivedFrom":[subQ1,subQ0]});Q100=makeQuery(id+"F0.imprint","IMPRINT",FACE,{"disambiguationData":[TD([[makeQuery(id+"F0.imprint","IMPRINT",EDGE,{"disambiguationData":[TD([[subQ2,1.0]])],"derivedFrom":subQ1}),-1.0]])]});}
            var Q101;
            {var subQ0=sQuery(id+"F0.wireOp",EDGE,"E2.8.2.0");var subQ1=sQuery(id+"F0.wireOp",EDGE,"E2.7.2.0");var subQ2=makeQuery(id+"F0.imprint","INTERSECT",VERTEX,{"disambiguationData":[OD(0.0)],"derivedFrom":[subQ1,subQ0]});Q101=makeQuery(id+"F0.imprint","IMPRINT",FACE,{"disambiguationData":[TD([[makeQuery(id+"F0.imprint","IMPRINT",EDGE,{"disambiguationData":[TD([[subQ2,-1.0]])],"derivedFrom":subQ1}),-1.0]])]});}
            var Q102;
            {var subQ0=sQuery(id+"F0.wireOp",EDGE,"E2.8.4.0");var subQ1=sQuery(id+"F0.wireOp",EDGE,"E2.7.4.0");var subQ2=makeQuery(id+"F0.imprint","INTERSECT",VERTEX,{"disambiguationData":[OD(0.0)],"derivedFrom":[subQ1,subQ0]});Q102=makeQuery(id+"F0.imprint","IMPRINT",FACE,{"disambiguationData":[TD([[makeQuery(id+"F0.imprint","IMPRINT",EDGE,{"disambiguationData":[TD([[subQ2,-1.0]])],"derivedFrom":subQ1}),-1.0]])]});}
            var Q103;
            {var subQ0=sQuery(id+"F0.wireOp",EDGE,"E2.7.2.0");var subQ1=sQuery(id+"F0.wireOp",EDGE,"E2.6.2.0");var subQ2=makeQuery(id+"F0.imprint","INTERSECT",VERTEX,{"disambiguationData":[OD(0.0)],"derivedFrom":[subQ1,subQ0]});Q103=makeQuery(id+"F0.imprint","IMPRINT",FACE,{"disambiguationData":[TD([[makeQuery(id+"F0.imprint","IMPRINT",EDGE,{"disambiguationData":[TD([[subQ2,-1.0]])],"derivedFrom":subQ1}),-1.0]])]});}
            var Q104;
            {var subQ0=sQuery(id+"F0.wireOp",EDGE,"E2.7.4.0");var subQ1=sQuery(id+"F0.wireOp",EDGE,"E2.6.4.0");var subQ2=makeQuery(id+"F0.imprint","INTERSECT",VERTEX,{"disambiguationData":[OD(0.0)],"derivedFrom":[subQ1,subQ0]});Q104=makeQuery(id+"F0.imprint","IMPRINT",FACE,{"disambiguationData":[TD([[makeQuery(id+"F0.imprint","IMPRINT",EDGE,{"disambiguationData":[TD([[subQ2,-1.0]])],"derivedFrom":subQ1}),-1.0]])]});}
            var Q105;
            {var subQ0=sQuery(id+"F0.wireOp",EDGE,"E2.5.4.0");var subQ1=sQuery(id+"F0.wireOp",EDGE,"E2.4.4.0");var subQ2=makeQuery(id+"F0.imprint","INTERSECT",VERTEX,{"disambiguationData":[OD(0.0)],"derivedFrom":[subQ1,subQ0]});Q105=makeQuery(id+"F0.imprint","IMPRINT",FACE,{"disambiguationData":[TD([[makeQuery(id+"F0.imprint","IMPRINT",EDGE,{"disambiguationData":[TD([[subQ2,-1.0]])],"derivedFrom":subQ1}),-1.0]])]});}
            var Q106;
            {var subQ0=sQuery(id+"F0.wireOp",EDGE,"E2.6.2.0");var subQ1=sQuery(id+"F0.wireOp",EDGE,"E2.5.2.0");var subQ2=makeQuery(id+"F0.imprint","INTERSECT",VERTEX,{"disambiguationData":[OD(0.0)],"derivedFrom":[subQ1,subQ0]});Q106=makeQuery(id+"F0.imprint","IMPRINT",FACE,{"disambiguationData":[TD([[makeQuery(id+"F0.imprint","IMPRINT",EDGE,{"disambiguationData":[TD([[subQ2,-1.0]])],"derivedFrom":subQ1}),-1.0]])]});}
            var Q107;
            {var subQ0=sQuery(id+"F0.wireOp",EDGE,"E2.6.4.0");var subQ1=sQuery(id+"F0.wireOp",EDGE,"E2.5.4.0");var subQ2=makeQuery(id+"F0.imprint","INTERSECT",VERTEX,{"disambiguationData":[OD(0.0)],"derivedFrom":[subQ1,subQ0]});Q107=makeQuery(id+"F0.imprint","IMPRINT",FACE,{"disambiguationData":[TD([[makeQuery(id+"F0.imprint","IMPRINT",EDGE,{"disambiguationData":[TD([[subQ2,-1.0]])],"derivedFrom":subQ1}),-1.0]])]});}
            var Q108;
            {var subQ0=sQuery(id+"F0.wireOp",EDGE,"E2.4.2.0");var subQ1=sQuery(id+"F0.wireOp",EDGE,"E2.3.2.0");var subQ2=makeQuery(id+"F0.imprint","INTERSECT",VERTEX,{"disambiguationData":[OD(0.0)],"derivedFrom":[subQ1,subQ0]});Q108=makeQuery(id+"F0.imprint","IMPRINT",FACE,{"disambiguationData":[TD([[makeQuery(id+"F0.imprint","IMPRINT",EDGE,{"disambiguationData":[TD([[subQ2,-1.0]])],"derivedFrom":subQ1}),-1.0]])]});}
            var Q109;
            {var subQ0=sQuery(id+"F0.wireOp",EDGE,"E2.4.4.0");var subQ1=sQuery(id+"F0.wireOp",EDGE,"E2.3.4.0");var subQ2=makeQuery(id+"F0.imprint","INTERSECT",VERTEX,{"disambiguationData":[OD(0.0)],"derivedFrom":[subQ1,subQ0]});Q109=makeQuery(id+"F0.imprint","IMPRINT",FACE,{"disambiguationData":[TD([[makeQuery(id+"F0.imprint","IMPRINT",EDGE,{"disambiguationData":[TD([[subQ2,-1.0]])],"derivedFrom":subQ1}),-1.0]])]});}
            var Q110;
            {var subQ0=sQuery(id+"F0.wireOp",EDGE,"E2.5.0.0");var subQ1=sQuery(id+"F0.wireOp",EDGE,"E2.4.0.0");var subQ2=makeQuery(id+"F0.imprint","INTERSECT",VERTEX,{"disambiguationData":[OD(1.0)],"derivedFrom":[subQ1,subQ0]});Q110=makeQuery(id+"F0.imprint","IMPRINT",FACE,{"disambiguationData":[TD([[makeQuery(id+"F0.imprint","IMPRINT",EDGE,{"disambiguationData":[TD([[subQ2,1.0]])],"derivedFrom":subQ1}),-1.0]])]});}
            var Q111;
            {var subQ0=sQuery(id+"F0.wireOp",EDGE,"E2.5.2.0");var subQ1=sQuery(id+"F0.wireOp",EDGE,"E2.4.2.0");var subQ2=makeQuery(id+"F0.imprint","INTERSECT",VERTEX,{"disambiguationData":[OD(0.0)],"derivedFrom":[subQ1,subQ0]});Q111=makeQuery(id+"F0.imprint","IMPRINT",FACE,{"disambiguationData":[TD([[makeQuery(id+"F0.imprint","IMPRINT",EDGE,{"disambiguationData":[TD([[subQ2,-1.0]])],"derivedFrom":subQ1}),-1.0]])]});}
            var Q112;
            {var subQ0=sQuery(id+"F0.wireOp",EDGE,"E2.3.2.0");var subQ1=sQuery(id+"F0.wireOp",EDGE,"E2.2.2.0");var subQ2=makeQuery(id+"F0.imprint","INTERSECT",VERTEX,{"disambiguationData":[OD(0.0)],"derivedFrom":[subQ1,subQ0]});Q112=makeQuery(id+"F0.imprint","IMPRINT",FACE,{"disambiguationData":[TD([[makeQuery(id+"F0.imprint","IMPRINT",EDGE,{"disambiguationData":[TD([[subQ2,-1.0]])],"derivedFrom":subQ1}),-1.0]])]});}
            var Q113;
            {var subQ0=sQuery(id+"F0.wireOp",EDGE,"E2.3.4.0");var subQ1=sQuery(id+"F0.wireOp",EDGE,"E2.2.4.0");var subQ2=makeQuery(id+"F0.imprint","INTERSECT",VERTEX,{"disambiguationData":[OD(0.0)],"derivedFrom":[subQ1,subQ0]});Q113=makeQuery(id+"F0.imprint","IMPRINT",FACE,{"disambiguationData":[TD([[makeQuery(id+"F0.imprint","IMPRINT",EDGE,{"disambiguationData":[TD([[subQ2,-1.0]])],"derivedFrom":subQ1}),-1.0]])]});}
            var Q114;
            {var subQ0=sQuery(id+"F0.wireOp",EDGE,"E2.2.2.0");var subQ1=sQuery(id+"F0.wireOp",EDGE,"E2.1.2.0");var subQ2=makeQuery(id+"F0.imprint","INTERSECT",VERTEX,{"disambiguationData":[OD(0.0)],"derivedFrom":[subQ1,subQ0]});Q114=makeQuery(id+"F0.imprint","IMPRINT",FACE,{"disambiguationData":[TD([[makeQuery(id+"F0.imprint","IMPRINT",EDGE,{"disambiguationData":[TD([[subQ2,-1.0]])],"derivedFrom":subQ1}),-1.0]])]});}
            var Q115;
            {var subQ0=sQuery(id+"F0.wireOp",EDGE,"E2.2.4.0");var subQ1=sQuery(id+"F0.wireOp",EDGE,"E2.1.4.0");var subQ2=makeQuery(id+"F0.imprint","INTERSECT",VERTEX,{"disambiguationData":[OD(0.0)],"derivedFrom":[subQ1,subQ0]});Q115=makeQuery(id+"F0.imprint","IMPRINT",FACE,{"disambiguationData":[TD([[makeQuery(id+"F0.imprint","IMPRINT",EDGE,{"disambiguationData":[TD([[subQ2,-1.0]])],"derivedFrom":subQ1}),-1.0]])]});}
            var Q116;
            {var subQ0=sQuery(id+"F0.wireOp",EDGE,"E2.11.4.0");var subQ1=sQuery(id+"F0.wireOp",EDGE,"E2.10.4.0");var subQ2=makeQuery(id+"F0.imprint","INTERSECT",VERTEX,{"disambiguationData":[OD(0.0)],"derivedFrom":[subQ1,subQ0]});Q116=makeQuery(id+"F0.imprint","IMPRINT",FACE,{"disambiguationData":[TD([[makeQuery(id+"F0.imprint","IMPRINT",EDGE,{"disambiguationData":[TD([[subQ2,-1.0]])],"derivedFrom":subQ1}),-1.0]])]});}
            var Q117;
            {var subQ0=sQuery(id+"F0.wireOp",EDGE,"E2.10.2.0");var subQ1=sQuery(id+"F0.wireOp",EDGE,"E2.9.2.0");var subQ2=makeQuery(id+"F0.imprint","INTERSECT",VERTEX,{"disambiguationData":[OD(0.0)],"derivedFrom":[subQ1,subQ0]});Q117=makeQuery(id+"F0.imprint","IMPRINT",FACE,{"disambiguationData":[TD([[makeQuery(id+"F0.imprint","IMPRINT",EDGE,{"disambiguationData":[TD([[subQ2,-1.0]])],"derivedFrom":subQ1}),-1.0]])]});}
            var Q118;
            {var subQ0=sQuery(id+"F0.wireOp",EDGE,"E2.10.4.0");var subQ1=sQuery(id+"F0.wireOp",EDGE,"E2.9.4.0");var subQ2=makeQuery(id+"F0.imprint","INTERSECT",VERTEX,{"disambiguationData":[OD(0.0)],"derivedFrom":[subQ1,subQ0]});Q118=makeQuery(id+"F0.imprint","IMPRINT",FACE,{"disambiguationData":[TD([[makeQuery(id+"F0.imprint","IMPRINT",EDGE,{"disambiguationData":[TD([[subQ2,-1.0]])],"derivedFrom":subQ1}),-1.0]])]});}
            var Q119;
            {var subQ0=sQuery(id+"F0.wireOp",EDGE,"E2.11.2.0");var subQ1=sQuery(id+"F0.wireOp",EDGE,"E2.10.2.0");var subQ2=makeQuery(id+"F0.imprint","INTERSECT",VERTEX,{"disambiguationData":[OD(0.0)],"derivedFrom":[subQ1,subQ0]});Q119=makeQuery(id+"F0.imprint","IMPRINT",FACE,{"disambiguationData":[TD([[makeQuery(id+"F0.imprint","IMPRINT",EDGE,{"disambiguationData":[TD([[subQ2,-1.0]])],"derivedFrom":subQ1}),-1.0]])]});}
            var Q120;
            {var subQ0=sQuery(id+"F0.wireOp",EDGE,"E2.5.6.0");var subQ1=sQuery(id+"F0.wireOp",EDGE,"E2.4.6.0");var subQ2=makeQuery(id+"F0.imprint","INTERSECT",VERTEX,{"disambiguationData":[OD(0.0)],"derivedFrom":[subQ1,subQ0]});Q120=makeQuery(id+"F0.imprint","IMPRINT",FACE,{"disambiguationData":[TD([[makeQuery(id+"F0.imprint","IMPRINT",EDGE,{"disambiguationData":[TD([[subQ2,1.0]])],"derivedFrom":subQ1}),-1.0]])]});}
            var Q121;
            {var subQ0=sQuery(id+"F0.wireOp",EDGE,"E2.7.4.0");var subQ1=sQuery(id+"F0.wireOp",EDGE,"E2.6.4.0");var subQ2=makeQuery(id+"F0.imprint","INTERSECT",VERTEX,{"disambiguationData":[OD(0.0)],"derivedFrom":[subQ1,subQ0]});Q121=makeQuery(id+"F0.imprint","IMPRINT",FACE,{"disambiguationData":[TD([[makeQuery(id+"F0.imprint","IMPRINT",EDGE,{"disambiguationData":[TD([[subQ2,1.0]])],"derivedFrom":subQ1}),-1.0]])]});}
            var Q122;
            {var subQ0=sQuery(id+"F0.wireOp",EDGE,"E2.5.0.0");var subQ1=sQuery(id+"F0.wireOp",EDGE,"E2.4.0.0");var subQ2=makeQuery(id+"F0.imprint","INTERSECT",VERTEX,{"disambiguationData":[OD(0.0)],"derivedFrom":[subQ1,subQ0]});Q122=makeQuery(id+"F0.imprint","IMPRINT",FACE,{"disambiguationData":[TD([[makeQuery(id+"F0.imprint","IMPRINT",EDGE,{"disambiguationData":[TD([[subQ2,-1.0]])],"derivedFrom":subQ1}),-1.0]])]});}
            var Q123;
            {var subQ0=sQuery(id+"F0.wireOp",EDGE,"E2.11.4.0");var subQ1=sQuery(id+"F0.wireOp",EDGE,"E2.10.4.0");var subQ2=makeQuery(id+"F0.imprint","INTERSECT",VERTEX,{"disambiguationData":[OD(0.0)],"derivedFrom":[subQ1,subQ0]});Q123=makeQuery(id+"F0.imprint","IMPRINT",FACE,{"disambiguationData":[TD([[makeQuery(id+"F0.imprint","IMPRINT",EDGE,{"disambiguationData":[TD([[subQ2,1.0]])],"derivedFrom":subQ1}),1.0]])]});}
            var Q124;
            {var subQ0=sQuery(id+"F0.wireOp",EDGE,"E2.11.6.0");var subQ1=sQuery(id+"F0.wireOp",EDGE,"E2.10.6.0");var subQ2=makeQuery(id+"F0.imprint","INTERSECT",VERTEX,{"disambiguationData":[OD(0.0)],"derivedFrom":[subQ1,subQ0]});Q124=makeQuery(id+"F0.imprint","IMPRINT",FACE,{"disambiguationData":[TD([[makeQuery(id+"F0.imprint","IMPRINT",EDGE,{"disambiguationData":[TD([[subQ2,1.0]])],"derivedFrom":subQ1}),1.0]])]});}
            var Q125;
            {var subQ0=sQuery(id+"F0.wireOp",EDGE,"E2.11.2.0");var subQ1=sQuery(id+"F0.wireOp",EDGE,"E2.10.2.0");var subQ2=makeQuery(id+"F0.imprint","INTERSECT",VERTEX,{"disambiguationData":[OD(0.0)],"derivedFrom":[subQ1,subQ0]});Q125=makeQuery(id+"F0.imprint","IMPRINT",FACE,{"disambiguationData":[TD([[makeQuery(id+"F0.imprint","IMPRINT",EDGE,{"disambiguationData":[TD([[subQ2,1.0]])],"derivedFrom":subQ1}),1.0]])]});}
            var Q126;
            {var subQ0=sQuery(id+"F0.wireOp",EDGE,"E2.6.6.0");var subQ1=sQuery(id+"F0.wireOp",EDGE,"E2.5.6.0");var subQ2=makeQuery(id+"F0.imprint","INTERSECT",VERTEX,{"disambiguationData":[OD(0.0)],"derivedFrom":[subQ1,subQ0]});Q126=makeQuery(id+"F0.imprint","IMPRINT",FACE,{"disambiguationData":[TD([[makeQuery(id+"F0.imprint","IMPRINT",EDGE,{"disambiguationData":[TD([[subQ2,1.0]])],"derivedFrom":subQ1}),1.0]])]});}
            var Q127;
            {var subQ0=sQuery(id+"F0.wireOp",EDGE,"E2.6.2.0");var subQ1=sQuery(id+"F0.wireOp",EDGE,"E2.5.2.0");var subQ2=makeQuery(id+"F0.imprint","INTERSECT",VERTEX,{"disambiguationData":[OD(0.0)],"derivedFrom":[subQ1,subQ0]});Q127=makeQuery(id+"F0.imprint","IMPRINT",FACE,{"disambiguationData":[TD([[makeQuery(id+"F0.imprint","IMPRINT",EDGE,{"disambiguationData":[TD([[subQ2,1.0]])],"derivedFrom":subQ1}),1.0]])]});}
            var Q128;
            {var subQ0=sQuery(id+"F0.wireOp",EDGE,"E2.6.4.0");var subQ1=sQuery(id+"F0.wireOp",EDGE,"E2.5.4.0");var subQ2=makeQuery(id+"F0.imprint","INTERSECT",VERTEX,{"disambiguationData":[OD(0.0)],"derivedFrom":[subQ1,subQ0]});Q128=makeQuery(id+"F0.imprint","IMPRINT",FACE,{"disambiguationData":[TD([[makeQuery(id+"F0.imprint","IMPRINT",EDGE,{"disambiguationData":[TD([[subQ2,1.0]])],"derivedFrom":subQ1}),1.0]])]});}
            var Q129;
            {var subQ0=sQuery(id+"F0.wireOp",EDGE,"E2.1.6.0");var subQ1=sQuery(id+"F0.wireOp",EDGE,"E2.0.6.0");var subQ2=makeQuery(id+"F0.imprint","INTERSECT",VERTEX,{"disambiguationData":[OD(0.0)],"derivedFrom":[subQ1,subQ0]});Q129=makeQuery(id+"F0.imprint","IMPRINT",FACE,{"disambiguationData":[TD([[makeQuery(id+"F0.imprint","IMPRINT",EDGE,{"disambiguationData":[TD([[subQ2,1.0]])],"derivedFrom":subQ1}),1.0]])]});}
            var Q130;
            {var subQ0=sQuery(id+"F0.wireOp",EDGE,"E2.1.1.0");var subQ1=sQuery(id+"F0.wireOp",EDGE,"E2.0.1.0");var subQ2=makeQuery(id+"F0.imprint","INTERSECT",VERTEX,{"disambiguationData":[OD(0.0)],"derivedFrom":[subQ1,subQ0]});Q130=makeQuery(id+"F0.imprint","IMPRINT",FACE,{"disambiguationData":[TD([[makeQuery(id+"F0.imprint","IMPRINT",EDGE,{"disambiguationData":[TD([[subQ2,-1.0]])],"derivedFrom":subQ1}),-1.0]])]});}
            var Q131;
            {var subQ0=sQuery(id+"F0.wireOp",EDGE,"E2.1.4.0");var subQ1=sQuery(id+"F0.wireOp",EDGE,"E2.0.4.0");var subQ2=makeQuery(id+"F0.imprint","INTERSECT",VERTEX,{"disambiguationData":[OD(0.0)],"derivedFrom":[subQ1,subQ0]});Q131=makeQuery(id+"F0.imprint","IMPRINT",FACE,{"disambiguationData":[TD([[makeQuery(id+"F0.imprint","IMPRINT",EDGE,{"disambiguationData":[TD([[subQ2,1.0]])],"derivedFrom":subQ1}),1.0]])]});}
            var Q132;
            {var subQ0=sQuery(id+"F0.wireOp",EDGE,"E2.10.4.0");var subQ1=sQuery(id+"F0.wireOp",EDGE,"E2.9.4.0");var subQ2=makeQuery(id+"F0.imprint","INTERSECT",VERTEX,{"disambiguationData":[OD(0.0)],"derivedFrom":[subQ1,subQ0]});Q132=makeQuery(id+"F0.imprint","IMPRINT",FACE,{"disambiguationData":[TD([[makeQuery(id+"F0.imprint","IMPRINT",EDGE,{"disambiguationData":[TD([[subQ2,-1.0]])],"derivedFrom":subQ1}),1.0]])]});}
            var Q133;
            {var subQ0=sQuery(id+"F0.wireOp",EDGE,"E2.11.0.0");var subQ1=sQuery(id+"F0.wireOp",EDGE,"E2.10.0.0");var subQ2=makeQuery(id+"F0.imprint","INTERSECT",VERTEX,{"disambiguationData":[OD(1.0)],"derivedFrom":[subQ1,subQ0]});Q133=makeQuery(id+"F0.imprint","IMPRINT",FACE,{"disambiguationData":[TD([[makeQuery(id+"F0.imprint","IMPRINT",EDGE,{"disambiguationData":[TD([[subQ2,1.0]])],"derivedFrom":subQ1}),1.0]])]});}
            var Q134;
            {var subQ0=sQuery(id+"F0.wireOp",EDGE,"E2.6.0.0");var subQ1=sQuery(id+"F0.wireOp",EDGE,"E2.5.0.0");var subQ2=makeQuery(id+"F0.imprint","INTERSECT",VERTEX,{"disambiguationData":[OD(1.0)],"derivedFrom":[subQ1,subQ0]});Q134=makeQuery(id+"F0.imprint","IMPRINT",FACE,{"disambiguationData":[TD([[makeQuery(id+"F0.imprint","IMPRINT",EDGE,{"disambiguationData":[TD([[subQ2,1.0]])],"derivedFrom":subQ1}),1.0]])]});}
            var Q135;
            {var subQ0=sQuery(id+"F0.wireOp",EDGE,"E2.1.4.0");var subQ1=sQuery(id+"F0.wireOp",EDGE,"E2.1.3.0");var subQ2=makeQuery(id+"F0.imprint","INTERSECT",VERTEX,{"disambiguationData":[OD(0.0)],"derivedFrom":[subQ1,subQ0]});Q135=makeQuery(id+"F0.imprint","IMPRINT",FACE,{"disambiguationData":[TD([[makeQuery(id+"F0.imprint","IMPRINT",EDGE,{"disambiguationData":[TD([[subQ2,-1.0]])],"derivedFrom":subQ1}),1.0]])]});}
            var Q136;
            {var subQ0=sQuery(id+"F0.wireOp",EDGE,"E2.1.1.0");var subQ1=sQuery(id+"F0.wireOp",EDGE,"E2.0.1.0");var subQ2=makeQuery(id+"F0.imprint","INTERSECT",VERTEX,{"disambiguationData":[OD(0.0)],"derivedFrom":[subQ1,subQ0]});Q136=makeQuery(id+"F0.imprint","IMPRINT",FACE,{"disambiguationData":[TD([[makeQuery(id+"F0.imprint","IMPRINT",EDGE,{"disambiguationData":[TD([[subQ2,-1.0]])],"derivedFrom":subQ1}),1.0]])]});}
            var Q137;
            {var subQ0=sQuery(id+"F0.wireOp",EDGE,"E2.4.6.0");var subQ1=sQuery(id+"F0.wireOp",EDGE,"E2.3.6.0");var subQ2=makeQuery(id+"F0.imprint","INTERSECT",VERTEX,{"disambiguationData":[OD(0.0)],"derivedFrom":[subQ1,subQ0]});Q137=makeQuery(id+"F0.imprint","IMPRINT",FACE,{"disambiguationData":[TD([[makeQuery(id+"F0.imprint","IMPRINT",EDGE,{"disambiguationData":[TD([[subQ2,1.0]])],"derivedFrom":subQ1}),-1.0]])]});}
            var Q138;
            {var subQ0=sQuery(id+"F0.wireOp",EDGE,"E2.7.3.1");var subQ1=sQuery(id+"F0.wireOp",EDGE,"E2.6.3.0");var subQ2=makeQuery(id+"F0.imprint","INTERSECT",VERTEX,{"derivedFrom":[subQ1,subQ0]});Q138=makeQuery(id+"F0.imprint","IMPRINT",FACE,{"disambiguationData":[TD([[makeQuery(id+"F0.imprint","IMPRINT",EDGE,{"disambiguationData":[TD([[subQ2,1.0]])],"derivedFrom":subQ1}),-1.0]])]});}
            var Q139;
            {var subQ0=sQuery(id+"F0.wireOp",EDGE,"E2.6.1.1");var subQ1=sQuery(id+"F0.wireOp",EDGE,"E2.5.1.0");var subQ2=makeQuery(id+"F0.imprint","INTERSECT",VERTEX,{"derivedFrom":[subQ1,subQ0]});Q139=makeQuery(id+"F0.imprint","IMPRINT",FACE,{"disambiguationData":[TD([[makeQuery(id+"F0.imprint","IMPRINT",EDGE,{"disambiguationData":[TD([[subQ2,1.0]])],"derivedFrom":subQ1}),-1.0]])]});}
            var Q140;
            {var subQ0=sQuery(id+"F0.wireOp",EDGE,"E2.3.5.1");var subQ1=sQuery(id+"F0.wireOp",EDGE,"E2.2.5.0");var subQ2=makeQuery(id+"F0.imprint","INTERSECT",VERTEX,{"derivedFrom":[subQ1,subQ0]});Q140=makeQuery(id+"F0.imprint","IMPRINT",FACE,{"disambiguationData":[TD([[makeQuery(id+"F0.imprint","IMPRINT",EDGE,{"disambiguationData":[TD([[subQ2,1.0]])],"derivedFrom":subQ1}),-1.0]])]});}
            var Q141;
            {var subQ0=sQuery(id+"F0.wireOp",EDGE,"E2.4.3.1");var subQ1=sQuery(id+"F0.wireOp",EDGE,"E2.3.3.0");var subQ2=makeQuery(id+"F0.imprint","INTERSECT",VERTEX,{"derivedFrom":[subQ1,subQ0]});Q141=makeQuery(id+"F0.imprint","IMPRINT",FACE,{"disambiguationData":[TD([[makeQuery(id+"F0.imprint","IMPRINT",EDGE,{"disambiguationData":[TD([[subQ2,1.0]])],"derivedFrom":subQ1}),-1.0]])]});}
            var Q142;
            {var subQ0=sQuery(id+"F0.wireOp",EDGE,"E2.3.3.1");var subQ1=sQuery(id+"F0.wireOp",EDGE,"E2.2.3.0");var subQ2=makeQuery(id+"F0.imprint","INTERSECT",VERTEX,{"derivedFrom":[subQ1,subQ0]});Q142=makeQuery(id+"F0.imprint","IMPRINT",FACE,{"disambiguationData":[TD([[makeQuery(id+"F0.imprint","IMPRINT",EDGE,{"disambiguationData":[TD([[subQ2,1.0]])],"derivedFrom":subQ1}),-1.0]])]});}
            var Q143;
            {var subQ0=sQuery(id+"F0.wireOp",EDGE,"E2.1.3.0");var subQ1=sQuery(id+"F0.wireOp",EDGE,"E2.0.3.0");var subQ2=makeQuery(id+"F0.imprint","INTERSECT",VERTEX,{"disambiguationData":[OD(0.0)],"derivedFrom":[subQ1,subQ0]});Q143=makeQuery(id+"F0.imprint","IMPRINT",FACE,{"disambiguationData":[TD([[makeQuery(id+"F0.imprint","IMPRINT",EDGE,{"disambiguationData":[TD([[subQ2,-1.0]])],"derivedFrom":subQ1}),-1.0]])]});}
            var Q144;
            {var subQ0=sQuery(id+"F0.wireOp",EDGE,"E2.11.2.0");var subQ1=sQuery(id+"F0.wireOp",EDGE,"E2.11.1.0");var subQ2=makeQuery(id+"F0.imprint","INTERSECT",VERTEX,{"disambiguationData":[OD(0.0)],"derivedFrom":[subQ1,subQ0]});Q144=makeQuery(id+"F0.imprint","IMPRINT",FACE,{"disambiguationData":[TD([[makeQuery(id+"F0.imprint","IMPRINT",EDGE,{"disambiguationData":[TD([[subQ2,-1.0]])],"derivedFrom":subQ1}),-1.0]])]});}
            var Q145;
            {var subQ0=sQuery(id+"F0.wireOp",EDGE,"E2.11.1.1");var subQ1=sQuery(id+"F0.wireOp",EDGE,"E2.10.1.0");var subQ2=makeQuery(id+"F0.imprint","INTERSECT",VERTEX,{"derivedFrom":[subQ1,subQ0]});Q145=makeQuery(id+"F0.imprint","IMPRINT",FACE,{"disambiguationData":[TD([[makeQuery(id+"F0.imprint","IMPRINT",EDGE,{"disambiguationData":[TD([[subQ2,1.0]])],"derivedFrom":subQ1}),-1.0]])]});}
            var Q146;
            {var subQ0=sQuery(id+"F0.wireOp",EDGE,"E2.8.5.1");var subQ1=sQuery(id+"F0.wireOp",EDGE,"E2.7.5.0");var subQ2=makeQuery(id+"F0.imprint","INTERSECT",VERTEX,{"derivedFrom":[subQ1,subQ0]});Q146=makeQuery(id+"F0.imprint","IMPRINT",FACE,{"disambiguationData":[TD([[makeQuery(id+"F0.imprint","IMPRINT",EDGE,{"disambiguationData":[TD([[subQ2,1.0]])],"derivedFrom":subQ1}),-1.0]])]});}
            var Q147;
            {var subQ0=sQuery(id+"F0.wireOp",EDGE,"E2.9.3.1");var subQ1=sQuery(id+"F0.wireOp",EDGE,"E2.8.3.0");var subQ2=makeQuery(id+"F0.imprint","INTERSECT",VERTEX,{"derivedFrom":[subQ1,subQ0]});Q147=makeQuery(id+"F0.imprint","IMPRINT",FACE,{"disambiguationData":[TD([[makeQuery(id+"F0.imprint","IMPRINT",EDGE,{"disambiguationData":[TD([[subQ2,1.0]])],"derivedFrom":subQ1}),-1.0]])]});}
            var Q148;
            {var subQ0=sQuery(id+"F0.wireOp",EDGE,"E2.7.5.1");var subQ1=sQuery(id+"F0.wireOp",EDGE,"E2.6.5.0");var subQ2=makeQuery(id+"F0.imprint","INTERSECT",VERTEX,{"derivedFrom":[subQ1,subQ0]});Q148=makeQuery(id+"F0.imprint","IMPRINT",FACE,{"disambiguationData":[TD([[makeQuery(id+"F0.imprint","IMPRINT",EDGE,{"disambiguationData":[TD([[subQ2,1.0]])],"derivedFrom":subQ1}),-1.0]])]});}
            var Q149;
            {var subQ0=sQuery(id+"F0.wireOp",EDGE,"E2.4.4.0");var subQ1=sQuery(id+"F0.wireOp",EDGE,"E2.4.3.0");var subQ2=makeQuery(id+"F0.imprint","INTERSECT",VERTEX,{"disambiguationData":[OD(0.0)],"derivedFrom":[subQ1,subQ0]});Q149=makeQuery(id+"F0.imprint","IMPRINT",FACE,{"disambiguationData":[TD([[makeQuery(id+"F0.imprint","IMPRINT",EDGE,{"disambiguationData":[TD([[subQ2,-1.0]])],"derivedFrom":subQ1}),-1.0]])]});}
            var Q150;
            {var subQ0=sQuery(id+"F0.wireOp",EDGE,"E2.1.1.0");var subQ1=sQuery(id+"F0.wireOp",EDGE,"E2.0.1.0");var subQ2=makeQuery(id+"F0.imprint","INTERSECT",VERTEX,{"disambiguationData":[OD(0.0)],"derivedFrom":[subQ1,subQ0]});Q150=makeQuery(id+"F0.imprint","IMPRINT",FACE,{"disambiguationData":[TD([[makeQuery(id+"F0.imprint","IMPRINT",EDGE,{"disambiguationData":[TD([[subQ2,1.0]])],"derivedFrom":subQ1}),1.0]])]});}
            var Q151;
            {var subQ0=sQuery(id+"F0.wireOp",EDGE,"E2.11.1.0");var subQ1=sQuery(id+"F0.wireOp",EDGE,"E2.11.0.0");var subQ2=makeQuery(id+"F0.imprint","INTERSECT",VERTEX,{"disambiguationData":[OD(0.0)],"derivedFrom":[subQ1,subQ0]});Q151=makeQuery(id+"F0.imprint","IMPRINT",FACE,{"disambiguationData":[TD([[makeQuery(id+"F0.imprint","IMPRINT",EDGE,{"disambiguationData":[TD([[subQ2,-1.0]])],"derivedFrom":subQ1}),-1.0]])]});}
            var Q152;
            {var subQ0=sQuery(id+"F0.wireOp",EDGE,"E2.9.4.0");var subQ1=sQuery(id+"F0.wireOp",EDGE,"E2.9.3.0");var subQ2=makeQuery(id+"F0.imprint","INTERSECT",VERTEX,{"disambiguationData":[OD(0.0)],"derivedFrom":[subQ1,subQ0]});Q152=makeQuery(id+"F0.imprint","IMPRINT",FACE,{"disambiguationData":[TD([[makeQuery(id+"F0.imprint","IMPRINT",EDGE,{"disambiguationData":[TD([[subQ2,-1.0]])],"derivedFrom":subQ1}),-1.0]])]});}
            var Q153;
            {var subQ0=sQuery(id+"F0.wireOp",EDGE,"E2.8.6.0");var subQ1=sQuery(id+"F0.wireOp",EDGE,"E2.8.5.0");var subQ2=makeQuery(id+"F0.imprint","INTERSECT",VERTEX,{"disambiguationData":[OD(0.0)],"derivedFrom":[subQ1,subQ0]});Q153=makeQuery(id+"F0.imprint","IMPRINT",FACE,{"disambiguationData":[TD([[makeQuery(id+"F0.imprint","IMPRINT",EDGE,{"disambiguationData":[TD([[subQ2,-1.0]])],"derivedFrom":subQ1}),1.0]])]});}
            var Q154;
            {var subQ0=sQuery(id+"F0.wireOp",EDGE,"E2.10.2.0");var subQ1=sQuery(id+"F0.wireOp",EDGE,"E2.10.1.0");var subQ2=makeQuery(id+"F0.imprint","INTERSECT",VERTEX,{"disambiguationData":[OD(0.0)],"derivedFrom":[subQ1,subQ0]});Q154=makeQuery(id+"F0.imprint","IMPRINT",FACE,{"disambiguationData":[TD([[makeQuery(id+"F0.imprint","IMPRINT",EDGE,{"disambiguationData":[TD([[subQ2,-1.0]])],"derivedFrom":subQ1}),1.0]])]});}
            var Q155;
            {var subQ0=sQuery(id+"F0.wireOp",EDGE,"E2.2.4.0");var subQ1=sQuery(id+"F0.wireOp",EDGE,"E2.2.3.0");var subQ2=makeQuery(id+"F0.imprint","INTERSECT",VERTEX,{"disambiguationData":[OD(0.0)],"derivedFrom":[subQ1,subQ0]});Q155=makeQuery(id+"F0.imprint","IMPRINT",FACE,{"disambiguationData":[TD([[makeQuery(id+"F0.imprint","IMPRINT",EDGE,{"disambiguationData":[TD([[subQ2,-1.0]])],"derivedFrom":subQ1}),1.0]])]});}
            var Q156;
            {var subQ0=sQuery(id+"F0.wireOp",EDGE,"E2.1.3.0");var subQ1=sQuery(id+"F0.wireOp",EDGE,"E2.0.3.0");var subQ2=makeQuery(id+"F0.imprint","INTERSECT",VERTEX,{"disambiguationData":[OD(0.0)],"derivedFrom":[subQ1,subQ0]});Q156=makeQuery(id+"F0.imprint","IMPRINT",FACE,{"disambiguationData":[TD([[makeQuery(id+"F0.imprint","IMPRINT",EDGE,{"disambiguationData":[TD([[subQ2,1.0]])],"derivedFrom":subQ1}),-1.0]])]});}
            var Q157;
            {var subQ0=sQuery(id+"F0.wireOp",EDGE,"E2.9.4.0");var subQ1=sQuery(id+"F0.wireOp",EDGE,"E2.9.3.0");var subQ2=makeQuery(id+"F0.imprint","INTERSECT",VERTEX,{"disambiguationData":[OD(0.0)],"derivedFrom":[subQ1,subQ0]});Q157=makeQuery(id+"F0.imprint","IMPRINT",FACE,{"disambiguationData":[TD([[makeQuery(id+"F0.imprint","IMPRINT",EDGE,{"disambiguationData":[TD([[subQ2,-1.0]])],"derivedFrom":subQ1}),1.0]])]});}
            var Q158;
            {var subQ0=sQuery(id+"F0.wireOp",EDGE,"E2.9.6.0");var subQ1=sQuery(id+"F0.wireOp",EDGE,"E2.9.5.0");var subQ2=makeQuery(id+"F0.imprint","INTERSECT",VERTEX,{"disambiguationData":[OD(0.0)],"derivedFrom":[subQ1,subQ0]});Q158=makeQuery(id+"F0.imprint","IMPRINT",FACE,{"disambiguationData":[TD([[makeQuery(id+"F0.imprint","IMPRINT",EDGE,{"disambiguationData":[TD([[subQ2,-1.0]])],"derivedFrom":subQ1}),1.0]])]});}
            var Q159;
            {var subQ0=sQuery(id+"F0.wireOp",EDGE,"E2.7.4.0");var subQ1=sQuery(id+"F0.wireOp",EDGE,"E2.7.3.0");var subQ2=makeQuery(id+"F0.imprint","INTERSECT",VERTEX,{"disambiguationData":[OD(0.0)],"derivedFrom":[subQ1,subQ0]});Q159=makeQuery(id+"F0.imprint","IMPRINT",FACE,{"disambiguationData":[TD([[makeQuery(id+"F0.imprint","IMPRINT",EDGE,{"disambiguationData":[TD([[subQ2,-1.0]])],"derivedFrom":subQ1}),1.0]])]});}
            var Q160;
            {var subQ0=sQuery(id+"F0.wireOp",EDGE,"E2.7.6.0");var subQ1=sQuery(id+"F0.wireOp",EDGE,"E2.7.5.0");var subQ2=makeQuery(id+"F0.imprint","INTERSECT",VERTEX,{"disambiguationData":[OD(0.0)],"derivedFrom":[subQ1,subQ0]});Q160=makeQuery(id+"F0.imprint","IMPRINT",FACE,{"disambiguationData":[TD([[makeQuery(id+"F0.imprint","IMPRINT",EDGE,{"disambiguationData":[TD([[subQ2,-1.0]])],"derivedFrom":subQ1}),1.0]])]});}
            var Q161;
            {var subQ0=sQuery(id+"F0.wireOp",EDGE,"E2.8.4.0");var subQ1=sQuery(id+"F0.wireOp",EDGE,"E2.8.3.0");var subQ2=makeQuery(id+"F0.imprint","INTERSECT",VERTEX,{"disambiguationData":[OD(0.0)],"derivedFrom":[subQ1,subQ0]});Q161=makeQuery(id+"F0.imprint","IMPRINT",FACE,{"disambiguationData":[TD([[makeQuery(id+"F0.imprint","IMPRINT",EDGE,{"disambiguationData":[TD([[subQ2,-1.0]])],"derivedFrom":subQ1}),1.0]])]});}
            var Q162;
            {var subQ0=sQuery(id+"F0.wireOp",EDGE,"E2.5.4.0");var subQ1=sQuery(id+"F0.wireOp",EDGE,"E2.5.3.0");var subQ2=makeQuery(id+"F0.imprint","INTERSECT",VERTEX,{"disambiguationData":[OD(0.0)],"derivedFrom":[subQ1,subQ0]});Q162=makeQuery(id+"F0.imprint","IMPRINT",FACE,{"disambiguationData":[TD([[makeQuery(id+"F0.imprint","IMPRINT",EDGE,{"disambiguationData":[TD([[subQ2,-1.0]])],"derivedFrom":subQ1}),1.0]])]});}
            var Q163;
            {var subQ0=sQuery(id+"F0.wireOp",EDGE,"E2.5.6.0");var subQ1=sQuery(id+"F0.wireOp",EDGE,"E2.5.5.0");var subQ2=makeQuery(id+"F0.imprint","INTERSECT",VERTEX,{"disambiguationData":[OD(0.0)],"derivedFrom":[subQ1,subQ0]});Q163=makeQuery(id+"F0.imprint","IMPRINT",FACE,{"disambiguationData":[TD([[makeQuery(id+"F0.imprint","IMPRINT",EDGE,{"disambiguationData":[TD([[subQ2,-1.0]])],"derivedFrom":subQ1}),1.0]])]});}
            var Q164;
            {var subQ0=sQuery(id+"F0.wireOp",EDGE,"E2.6.2.0");var subQ1=sQuery(id+"F0.wireOp",EDGE,"E2.6.1.0");var subQ2=makeQuery(id+"F0.imprint","INTERSECT",VERTEX,{"disambiguationData":[OD(0.0)],"derivedFrom":[subQ1,subQ0]});Q164=makeQuery(id+"F0.imprint","IMPRINT",FACE,{"disambiguationData":[TD([[makeQuery(id+"F0.imprint","IMPRINT",EDGE,{"disambiguationData":[TD([[subQ2,-1.0]])],"derivedFrom":subQ1}),1.0]])]});}
            var Q165;
            {var subQ0=sQuery(id+"F0.wireOp",EDGE,"E2.6.4.0");var subQ1=sQuery(id+"F0.wireOp",EDGE,"E2.6.3.0");var subQ2=makeQuery(id+"F0.imprint","INTERSECT",VERTEX,{"disambiguationData":[OD(0.0)],"derivedFrom":[subQ1,subQ0]});Q165=makeQuery(id+"F0.imprint","IMPRINT",FACE,{"disambiguationData":[TD([[makeQuery(id+"F0.imprint","IMPRINT",EDGE,{"disambiguationData":[TD([[subQ2,-1.0]])],"derivedFrom":subQ1}),1.0]])]});}
            var Q166;
            {var subQ0=sQuery(id+"F0.wireOp",EDGE,"E2.4.4.0");var subQ1=sQuery(id+"F0.wireOp",EDGE,"E2.4.3.0");var subQ2=makeQuery(id+"F0.imprint","INTERSECT",VERTEX,{"disambiguationData":[OD(0.0)],"derivedFrom":[subQ1,subQ0]});Q166=makeQuery(id+"F0.imprint","IMPRINT",FACE,{"disambiguationData":[TD([[makeQuery(id+"F0.imprint","IMPRINT",EDGE,{"disambiguationData":[TD([[subQ2,-1.0]])],"derivedFrom":subQ1}),1.0]])]});}
            var Q167;
            {var subQ0=sQuery(id+"F0.wireOp",EDGE,"E2.4.6.0");var subQ1=sQuery(id+"F0.wireOp",EDGE,"E2.4.5.0");var subQ2=makeQuery(id+"F0.imprint","INTERSECT",VERTEX,{"disambiguationData":[OD(0.0)],"derivedFrom":[subQ1,subQ0]});Q167=makeQuery(id+"F0.imprint","IMPRINT",FACE,{"disambiguationData":[TD([[makeQuery(id+"F0.imprint","IMPRINT",EDGE,{"disambiguationData":[TD([[subQ2,-1.0]])],"derivedFrom":subQ1}),1.0]])]});}
            var Q168;
            {var subQ0=sQuery(id+"F0.wireOp",EDGE,"E2.5.2.0");var subQ1=sQuery(id+"F0.wireOp",EDGE,"E2.5.1.0");var subQ2=makeQuery(id+"F0.imprint","INTERSECT",VERTEX,{"disambiguationData":[OD(0.0)],"derivedFrom":[subQ1,subQ0]});Q168=makeQuery(id+"F0.imprint","IMPRINT",FACE,{"disambiguationData":[TD([[makeQuery(id+"F0.imprint","IMPRINT",EDGE,{"disambiguationData":[TD([[subQ2,-1.0]])],"derivedFrom":subQ1}),1.0]])]});}
            var Q169;
            {var subQ0=sQuery(id+"F0.wireOp",EDGE,"E2.0.1.0");var subQ1=sQuery(id+"F0.wireOp",EDGE,"E1.0");var subQ2=makeQuery(id+"F0.imprint","INTERSECT",VERTEX,{"disambiguationData":[OD(1.0)],"derivedFrom":[subQ1,subQ0]});Q169=makeQuery(id+"F0.imprint","IMPRINT",FACE,{"disambiguationData":[TD([[makeQuery(id+"F0.imprint","IMPRINT",EDGE,{"disambiguationData":[TD([[subQ2,-1.0]])],"derivedFrom":subQ1}),1.0]])]});}
            var Q170;
            {var subQ0=sQuery(id+"F0.wireOp",EDGE,"E2.1.5.0");var subQ1=sQuery(id+"F0.wireOp",EDGE,"E2.0.5.0");var subQ2=makeQuery(id+"F0.imprint","INTERSECT",VERTEX,{"disambiguationData":[OD(0.0)],"derivedFrom":[subQ1,subQ0]});Q170=makeQuery(id+"F0.imprint","IMPRINT",FACE,{"disambiguationData":[TD([[makeQuery(id+"F0.imprint","IMPRINT",EDGE,{"disambiguationData":[TD([[subQ2,-1.0]])],"derivedFrom":subQ1}),1.0]])]});}
            var Q171;
            {var subQ0=sQuery(id+"F0.wireOp",EDGE,"E2.3.6.0");var subQ1=sQuery(id+"F0.wireOp",EDGE,"E2.2.6.0");var subQ2=makeQuery(id+"F0.imprint","INTERSECT",VERTEX,{"disambiguationData":[OD(0.0)],"derivedFrom":[subQ1,subQ0]});Q171=makeQuery(id+"F0.imprint","IMPRINT",FACE,{"disambiguationData":[TD([[makeQuery(id+"F0.imprint","IMPRINT",EDGE,{"disambiguationData":[TD([[subQ2,1.0]])],"derivedFrom":subQ1}),-1.0]])]});}
            var Q172;
            {var subQ0=sQuery(id+"F0.wireOp",EDGE,"E2.11.3.0");var subQ1=sQuery(id+"F0.wireOp",EDGE,"E2.10.3.0");var subQ2=makeQuery(id+"F0.imprint","INTERSECT",VERTEX,{"disambiguationData":[OD(0.0)],"derivedFrom":[subQ1,subQ0]});Q172=makeQuery(id+"F0.imprint","IMPRINT",FACE,{"disambiguationData":[TD([[makeQuery(id+"F0.imprint","IMPRINT",EDGE,{"disambiguationData":[TD([[subQ2,-1.0]])],"derivedFrom":subQ1}),1.0]])]});}
            var Q173;
            {var subQ0=sQuery(id+"F0.wireOp",EDGE,"E2.11.5.0");var subQ1=sQuery(id+"F0.wireOp",EDGE,"E2.10.5.0");var subQ2=makeQuery(id+"F0.imprint","INTERSECT",VERTEX,{"disambiguationData":[OD(0.0)],"derivedFrom":[subQ1,subQ0]});Q173=makeQuery(id+"F0.imprint","IMPRINT",FACE,{"disambiguationData":[TD([[makeQuery(id+"F0.imprint","IMPRINT",EDGE,{"disambiguationData":[TD([[subQ2,-1.0]])],"derivedFrom":subQ1}),1.0]])]});}
            var Q174;
            {var subQ0=sQuery(id+"F0.wireOp",EDGE,"E2.1.2.1");var subQ1=sQuery(id+"F0.wireOp",EDGE,"E2.0.2.0");var subQ2=makeQuery(id+"F0.imprint","INTERSECT",VERTEX,{"derivedFrom":[subQ1,subQ0]});Q174=makeQuery(id+"F0.imprint","IMPRINT",FACE,{"disambiguationData":[TD([[makeQuery(id+"F0.imprint","IMPRINT",EDGE,{"disambiguationData":[TD([[subQ2,1.0]])],"derivedFrom":subQ1}),-1.0]])]});}
            var Q175;
            {var subQ0=sQuery(id+"F0.wireOp",EDGE,"E2.1.5.0");var subQ1=sQuery(id+"F0.wireOp",EDGE,"E2.0.5.0");var subQ2=makeQuery(id+"F0.imprint","INTERSECT",VERTEX,{"disambiguationData":[OD(0.0)],"derivedFrom":[subQ1,subQ0]});Q175=makeQuery(id+"F0.imprint","IMPRINT",FACE,{"disambiguationData":[TD([[makeQuery(id+"F0.imprint","IMPRINT",EDGE,{"disambiguationData":[TD([[subQ2,1.0]])],"derivedFrom":subQ1}),-1.0]])]});}
            var Q176;
            {var subQ0=sQuery(id+"F0.wireOp",EDGE,"E2.2.1.0");var subQ1=sQuery(id+"F0.wireOp",EDGE,"E2.1.1.0");var subQ2=makeQuery(id+"F0.imprint","INTERSECT",VERTEX,{"disambiguationData":[OD(0.0)],"derivedFrom":[subQ1,subQ0]});Q176=makeQuery(id+"F0.imprint","IMPRINT",FACE,{"disambiguationData":[TD([[makeQuery(id+"F0.imprint","IMPRINT",EDGE,{"disambiguationData":[TD([[subQ2,-1.0]])],"derivedFrom":subQ1}),1.0]])]});}
            var Q177;
            {var subQ0=sQuery(id+"F0.wireOp",EDGE,"E2.9.5.0");var subQ1=sQuery(id+"F0.wireOp",EDGE,"E2.8.5.0");var subQ2=makeQuery(id+"F0.imprint","INTERSECT",VERTEX,{"disambiguationData":[OD(0.0)],"derivedFrom":[subQ1,subQ0]});Q177=makeQuery(id+"F0.imprint","IMPRINT",FACE,{"disambiguationData":[TD([[makeQuery(id+"F0.imprint","IMPRINT",EDGE,{"disambiguationData":[TD([[subQ2,-1.0]])],"derivedFrom":subQ1}),1.0]])]});}
            var Q178;
            {var subQ0=sQuery(id+"F0.wireOp",EDGE,"E2.10.1.0");var subQ1=sQuery(id+"F0.wireOp",EDGE,"E2.9.1.0");var subQ2=makeQuery(id+"F0.imprint","INTERSECT",VERTEX,{"disambiguationData":[OD(0.0)],"derivedFrom":[subQ1,subQ0]});Q178=makeQuery(id+"F0.imprint","IMPRINT",FACE,{"disambiguationData":[TD([[makeQuery(id+"F0.imprint","IMPRINT",EDGE,{"disambiguationData":[TD([[subQ2,-1.0]])],"derivedFrom":subQ1}),1.0]])]});}
            var Q179;
            {var subQ0=sQuery(id+"F0.wireOp",EDGE,"E2.10.5.0");var subQ1=sQuery(id+"F0.wireOp",EDGE,"E2.9.5.0");var subQ2=makeQuery(id+"F0.imprint","INTERSECT",VERTEX,{"disambiguationData":[OD(0.0)],"derivedFrom":[subQ1,subQ0]});Q179=makeQuery(id+"F0.imprint","IMPRINT",FACE,{"disambiguationData":[TD([[makeQuery(id+"F0.imprint","IMPRINT",EDGE,{"disambiguationData":[TD([[subQ2,-1.0]])],"derivedFrom":subQ1}),1.0]])]});}
            var Q180;
            {var subQ0=sQuery(id+"F0.wireOp",EDGE,"E2.8.3.0");var subQ1=sQuery(id+"F0.wireOp",EDGE,"E2.7.3.0");var subQ2=makeQuery(id+"F0.imprint","INTERSECT",VERTEX,{"disambiguationData":[OD(0.0)],"derivedFrom":[subQ1,subQ0]});Q180=makeQuery(id+"F0.imprint","IMPRINT",FACE,{"disambiguationData":[TD([[makeQuery(id+"F0.imprint","IMPRINT",EDGE,{"disambiguationData":[TD([[subQ2,-1.0]])],"derivedFrom":subQ1}),1.0]])]});}
            var Q181;
            {var subQ0=sQuery(id+"F0.wireOp",EDGE,"E2.9.1.0");var subQ1=sQuery(id+"F0.wireOp",EDGE,"E2.8.1.0");var subQ2=makeQuery(id+"F0.imprint","INTERSECT",VERTEX,{"disambiguationData":[OD(0.0)],"derivedFrom":[subQ1,subQ0]});Q181=makeQuery(id+"F0.imprint","IMPRINT",FACE,{"disambiguationData":[TD([[makeQuery(id+"F0.imprint","IMPRINT",EDGE,{"disambiguationData":[TD([[subQ2,-1.0]])],"derivedFrom":subQ1}),1.0]])]});}
            var Q182;
            {var subQ0=sQuery(id+"F0.wireOp",EDGE,"E2.0.4.0");var subQ1=sQuery(id+"F0.wireOp",EDGE,"E2.0.3.0");var subQ2=makeQuery(id+"F0.imprint","INTERSECT",VERTEX,{"disambiguationData":[OD(0.0)],"derivedFrom":[subQ1,subQ0]});Q182=makeQuery(id+"F0.imprint","IMPRINT",FACE,{"disambiguationData":[TD([[makeQuery(id+"F0.imprint","IMPRINT",EDGE,{"disambiguationData":[TD([[subQ2,1.0]])],"derivedFrom":subQ1}),-1.0]])]});}
            var Q183;
            {var subQ0=sQuery(id+"F0.wireOp",EDGE,"E2.7.5.0");var subQ1=sQuery(id+"F0.wireOp",EDGE,"E2.6.5.0");var subQ2=makeQuery(id+"F0.imprint","INTERSECT",VERTEX,{"disambiguationData":[OD(0.0)],"derivedFrom":[subQ1,subQ0]});Q183=makeQuery(id+"F0.imprint","IMPRINT",FACE,{"disambiguationData":[TD([[makeQuery(id+"F0.imprint","IMPRINT",EDGE,{"disambiguationData":[TD([[subQ2,-1.0]])],"derivedFrom":subQ1}),1.0]])]});}
            var Q184;
            {var subQ0=sQuery(id+"F0.wireOp",EDGE,"E2.8.1.0");var subQ1=sQuery(id+"F0.wireOp",EDGE,"E2.7.1.0");var subQ2=makeQuery(id+"F0.imprint","INTERSECT",VERTEX,{"disambiguationData":[OD(0.0)],"derivedFrom":[subQ1,subQ0]});Q184=makeQuery(id+"F0.imprint","IMPRINT",FACE,{"disambiguationData":[TD([[makeQuery(id+"F0.imprint","IMPRINT",EDGE,{"disambiguationData":[TD([[subQ2,-1.0]])],"derivedFrom":subQ1}),1.0]])]});}
            var Q185;
            {var subQ0=sQuery(id+"F0.wireOp",EDGE,"E2.0.3.0");var subQ1=sQuery(id+"F0.wireOp",EDGE,"E2.0.2.0");var subQ2=makeQuery(id+"F0.imprint","INTERSECT",VERTEX,{"disambiguationData":[OD(0.0)],"derivedFrom":[subQ1,subQ0]});Q185=makeQuery(id+"F0.imprint","IMPRINT",FACE,{"disambiguationData":[TD([[makeQuery(id+"F0.imprint","IMPRINT",EDGE,{"disambiguationData":[TD([[subQ2,1.0]])],"derivedFrom":subQ1}),-1.0]])]});}
            var Q186;
            {var subQ0=sQuery(id+"F0.wireOp",EDGE,"E2.6.3.0");var subQ1=sQuery(id+"F0.wireOp",EDGE,"E2.5.3.0");var subQ2=makeQuery(id+"F0.imprint","INTERSECT",VERTEX,{"disambiguationData":[OD(0.0)],"derivedFrom":[subQ1,subQ0]});Q186=makeQuery(id+"F0.imprint","IMPRINT",FACE,{"disambiguationData":[TD([[makeQuery(id+"F0.imprint","IMPRINT",EDGE,{"disambiguationData":[TD([[subQ2,-1.0]])],"derivedFrom":subQ1}),1.0]])]});}
            var Q187;
            {var subQ0=sQuery(id+"F0.wireOp",EDGE,"E2.6.5.0");var subQ1=sQuery(id+"F0.wireOp",EDGE,"E2.5.5.0");var subQ2=makeQuery(id+"F0.imprint","INTERSECT",VERTEX,{"disambiguationData":[OD(0.0)],"derivedFrom":[subQ1,subQ0]});Q187=makeQuery(id+"F0.imprint","IMPRINT",FACE,{"disambiguationData":[TD([[makeQuery(id+"F0.imprint","IMPRINT",EDGE,{"disambiguationData":[TD([[subQ2,-1.0]])],"derivedFrom":subQ1}),1.0]])]});}
            var Q188;
            {var subQ0=sQuery(id+"F0.wireOp",EDGE,"E2.7.1.0");var subQ1=sQuery(id+"F0.wireOp",EDGE,"E2.6.1.0");var subQ2=makeQuery(id+"F0.imprint","INTERSECT",VERTEX,{"disambiguationData":[OD(0.0)],"derivedFrom":[subQ1,subQ0]});Q188=makeQuery(id+"F0.imprint","IMPRINT",FACE,{"disambiguationData":[TD([[makeQuery(id+"F0.imprint","IMPRINT",EDGE,{"disambiguationData":[TD([[subQ2,-1.0]])],"derivedFrom":subQ1}),1.0]])]});}
            var Q189;
            {var subQ0=sQuery(id+"F0.wireOp",EDGE,"E2.7.3.0");var subQ1=sQuery(id+"F0.wireOp",EDGE,"E2.6.3.0");var subQ2=makeQuery(id+"F0.imprint","INTERSECT",VERTEX,{"disambiguationData":[OD(0.0)],"derivedFrom":[subQ1,subQ0]});Q189=makeQuery(id+"F0.imprint","IMPRINT",FACE,{"disambiguationData":[TD([[makeQuery(id+"F0.imprint","IMPRINT",EDGE,{"disambiguationData":[TD([[subQ2,-1.0]])],"derivedFrom":subQ1}),1.0]])]});}
            var Q190;
            {var subQ0=sQuery(id+"F0.wireOp",EDGE,"E2.5.1.0");var subQ1=sQuery(id+"F0.wireOp",EDGE,"E2.4.1.0");var subQ2=makeQuery(id+"F0.imprint","INTERSECT",VERTEX,{"disambiguationData":[OD(0.0)],"derivedFrom":[subQ1,subQ0]});Q190=makeQuery(id+"F0.imprint","IMPRINT",FACE,{"disambiguationData":[TD([[makeQuery(id+"F0.imprint","IMPRINT",EDGE,{"disambiguationData":[TD([[subQ2,-1.0]])],"derivedFrom":subQ1}),1.0]])]});}
            var Q191;
            {var subQ0=sQuery(id+"F0.wireOp",EDGE,"E2.5.5.0");var subQ1=sQuery(id+"F0.wireOp",EDGE,"E2.4.5.0");var subQ2=makeQuery(id+"F0.imprint","INTERSECT",VERTEX,{"disambiguationData":[OD(0.0)],"derivedFrom":[subQ1,subQ0]});Q191=makeQuery(id+"F0.imprint","IMPRINT",FACE,{"disambiguationData":[TD([[makeQuery(id+"F0.imprint","IMPRINT",EDGE,{"disambiguationData":[TD([[subQ2,-1.0]])],"derivedFrom":subQ1}),1.0]])]});}
            var Q192;
            {var subQ0=sQuery(id+"F0.wireOp",EDGE,"E2.4.1.0");var subQ1=sQuery(id+"F0.wireOp",EDGE,"E2.3.1.0");var subQ2=makeQuery(id+"F0.imprint","INTERSECT",VERTEX,{"disambiguationData":[OD(0.0)],"derivedFrom":[subQ1,subQ0]});Q192=makeQuery(id+"F0.imprint","IMPRINT",FACE,{"disambiguationData":[TD([[makeQuery(id+"F0.imprint","IMPRINT",EDGE,{"disambiguationData":[TD([[subQ2,-1.0]])],"derivedFrom":subQ1}),1.0]])]});}
            var Q193;
            {var subQ0=sQuery(id+"F0.wireOp",EDGE,"E2.4.5.0");var subQ1=sQuery(id+"F0.wireOp",EDGE,"E2.3.5.0");var subQ2=makeQuery(id+"F0.imprint","INTERSECT",VERTEX,{"disambiguationData":[OD(0.0)],"derivedFrom":[subQ1,subQ0]});Q193=makeQuery(id+"F0.imprint","IMPRINT",FACE,{"disambiguationData":[TD([[makeQuery(id+"F0.imprint","IMPRINT",EDGE,{"disambiguationData":[TD([[subQ2,-1.0]])],"derivedFrom":subQ1}),1.0]])]});}
            var Q194;
            {var subQ0=sQuery(id+"F0.wireOp",EDGE,"E2.2.3.0");var subQ1=sQuery(id+"F0.wireOp",EDGE,"E2.1.3.0");var subQ2=makeQuery(id+"F0.imprint","INTERSECT",VERTEX,{"disambiguationData":[OD(0.0)],"derivedFrom":[subQ1,subQ0]});Q194=makeQuery(id+"F0.imprint","IMPRINT",FACE,{"disambiguationData":[TD([[makeQuery(id+"F0.imprint","IMPRINT",EDGE,{"disambiguationData":[TD([[subQ2,-1.0]])],"derivedFrom":subQ1}),1.0]])]});}
            var Q195;
            {var subQ0=sQuery(id+"F0.wireOp",EDGE,"E2.2.5.0");var subQ1=sQuery(id+"F0.wireOp",EDGE,"E2.1.5.0");var subQ2=makeQuery(id+"F0.imprint","INTERSECT",VERTEX,{"disambiguationData":[OD(0.0)],"derivedFrom":[subQ1,subQ0]});Q195=makeQuery(id+"F0.imprint","IMPRINT",FACE,{"disambiguationData":[TD([[makeQuery(id+"F0.imprint","IMPRINT",EDGE,{"disambiguationData":[TD([[subQ2,-1.0]])],"derivedFrom":subQ1}),1.0]])]});}
            var Q196;
            {var subQ0=sQuery(id+"F0.wireOp",EDGE,"E2.3.1.0");var subQ1=sQuery(id+"F0.wireOp",EDGE,"E2.2.1.0");var subQ2=makeQuery(id+"F0.imprint","INTERSECT",VERTEX,{"disambiguationData":[OD(0.0)],"derivedFrom":[subQ1,subQ0]});Q196=makeQuery(id+"F0.imprint","IMPRINT",FACE,{"disambiguationData":[TD([[makeQuery(id+"F0.imprint","IMPRINT",EDGE,{"disambiguationData":[TD([[subQ2,-1.0]])],"derivedFrom":subQ1}),1.0]])]});}
            var Q197;
            {var subQ0=sQuery(id+"F0.wireOp",EDGE,"E2.3.3.0");var subQ1=sQuery(id+"F0.wireOp",EDGE,"E2.2.3.0");var subQ2=makeQuery(id+"F0.imprint","INTERSECT",VERTEX,{"disambiguationData":[OD(0.0)],"derivedFrom":[subQ1,subQ0]});Q197=makeQuery(id+"F0.imprint","IMPRINT",FACE,{"disambiguationData":[TD([[makeQuery(id+"F0.imprint","IMPRINT",EDGE,{"disambiguationData":[TD([[subQ2,-1.0]])],"derivedFrom":subQ1}),1.0]])]});}
            var Q198;
            {var subQ0=sQuery(id+"F0.wireOp",EDGE,"E2.11.3.0");var subQ1=sQuery(id+"F0.wireOp",EDGE,"E2.10.3.0");var subQ2=makeQuery(id+"F0.imprint","INTERSECT",VERTEX,{"disambiguationData":[OD(0.0)],"derivedFrom":[subQ1,subQ0]});Q198=makeQuery(id+"F0.imprint","IMPRINT",FACE,{"disambiguationData":[TD([[makeQuery(id+"F0.imprint","IMPRINT",EDGE,{"disambiguationData":[TD([[subQ2,1.0]])],"derivedFrom":subQ1}),-1.0]])]});}
            var Q199;
            {var subQ0=sQuery(id+"F0.wireOp",EDGE,"E2.11.5.0");var subQ1=sQuery(id+"F0.wireOp",EDGE,"E2.10.5.0");var subQ2=makeQuery(id+"F0.imprint","INTERSECT",VERTEX,{"disambiguationData":[OD(0.0)],"derivedFrom":[subQ1,subQ0]});Q199=makeQuery(id+"F0.imprint","IMPRINT",FACE,{"disambiguationData":[TD([[makeQuery(id+"F0.imprint","IMPRINT",EDGE,{"disambiguationData":[TD([[subQ2,1.0]])],"derivedFrom":subQ1}),-1.0]])]});}
            var Q200;
            {var subQ0=sQuery(id+"F0.wireOp",EDGE,"E2.10.1.0");var subQ1=sQuery(id+"F0.wireOp",EDGE,"E2.9.1.0");var subQ2=makeQuery(id+"F0.imprint","INTERSECT",VERTEX,{"disambiguationData":[OD(0.0)],"derivedFrom":[subQ1,subQ0]});Q200=makeQuery(id+"F0.imprint","IMPRINT",FACE,{"disambiguationData":[TD([[makeQuery(id+"F0.imprint","IMPRINT",EDGE,{"disambiguationData":[TD([[subQ2,1.0]])],"derivedFrom":subQ1}),-1.0]])]});}
            var Q201;
            {var subQ0=sQuery(id+"F0.wireOp",EDGE,"E2.10.3.0");var subQ1=sQuery(id+"F0.wireOp",EDGE,"E2.9.3.0");var subQ2=makeQuery(id+"F0.imprint","INTERSECT",VERTEX,{"disambiguationData":[OD(0.0)],"derivedFrom":[subQ1,subQ0]});Q201=makeQuery(id+"F0.imprint","IMPRINT",FACE,{"disambiguationData":[TD([[makeQuery(id+"F0.imprint","IMPRINT",EDGE,{"disambiguationData":[TD([[subQ2,1.0]])],"derivedFrom":subQ1}),-1.0]])]});}
            var Q202;
            {var subQ0=sQuery(id+"F0.wireOp",EDGE,"E2.10.5.0");var subQ1=sQuery(id+"F0.wireOp",EDGE,"E2.9.5.0");var subQ2=makeQuery(id+"F0.imprint","INTERSECT",VERTEX,{"disambiguationData":[OD(0.0)],"derivedFrom":[subQ1,subQ0]});Q202=makeQuery(id+"F0.imprint","IMPRINT",FACE,{"disambiguationData":[TD([[makeQuery(id+"F0.imprint","IMPRINT",EDGE,{"disambiguationData":[TD([[subQ2,1.0]])],"derivedFrom":subQ1}),-1.0]])]});}
            var Q203;
            {var subQ0=sQuery(id+"F0.wireOp",EDGE,"E2.3.0.0");var subQ1=sQuery(id+"F0.wireOp",EDGE,"E2.2.0.0");var subQ2=makeQuery(id+"F0.imprint","INTERSECT",VERTEX,{"disambiguationData":[OD(0.0)],"derivedFrom":[subQ1,subQ0]});Q203=makeQuery(id+"F0.imprint","IMPRINT",FACE,{"disambiguationData":[TD([[makeQuery(id+"F0.imprint","IMPRINT",EDGE,{"disambiguationData":[TD([[subQ2,-1.0]])],"derivedFrom":subQ1}),-1.0]])]});}
            var Q204;
            {var subQ0=sQuery(id+"F0.wireOp",EDGE,"E2.7.0.0");var subQ1=sQuery(id+"F0.wireOp",EDGE,"E2.6.0.0");var subQ2=makeQuery(id+"F0.imprint","INTERSECT",VERTEX,{"disambiguationData":[OD(0.0)],"derivedFrom":[subQ1,subQ0]});Q204=makeQuery(id+"F0.imprint","IMPRINT",FACE,{"disambiguationData":[TD([[makeQuery(id+"F0.imprint","IMPRINT",EDGE,{"disambiguationData":[TD([[subQ2,-1.0]])],"derivedFrom":subQ1}),-1.0]])]});}
            var Q205;
            {var subQ0=sQuery(id+"F0.wireOp",EDGE,"E2.9.1.0");var subQ1=sQuery(id+"F0.wireOp",EDGE,"E2.8.1.0");var subQ2=makeQuery(id+"F0.imprint","INTERSECT",VERTEX,{"disambiguationData":[OD(0.0)],"derivedFrom":[subQ1,subQ0]});Q205=makeQuery(id+"F0.imprint","IMPRINT",FACE,{"disambiguationData":[TD([[makeQuery(id+"F0.imprint","IMPRINT",EDGE,{"disambiguationData":[TD([[subQ2,1.0]])],"derivedFrom":subQ1}),-1.0]])]});}
            var Q206;
            {var subQ0=sQuery(id+"F0.wireOp",EDGE,"E2.9.3.0");var subQ1=sQuery(id+"F0.wireOp",EDGE,"E2.8.3.0");var subQ2=makeQuery(id+"F0.imprint","INTERSECT",VERTEX,{"disambiguationData":[OD(0.0)],"derivedFrom":[subQ1,subQ0]});Q206=makeQuery(id+"F0.imprint","IMPRINT",FACE,{"disambiguationData":[TD([[makeQuery(id+"F0.imprint","IMPRINT",EDGE,{"disambiguationData":[TD([[subQ2,1.0]])],"derivedFrom":subQ1}),-1.0]])]});}
            var Q207;
            {var subQ0=sQuery(id+"F0.wireOp",EDGE,"E2.7.5.0");var subQ1=sQuery(id+"F0.wireOp",EDGE,"E2.6.5.0");var subQ2=makeQuery(id+"F0.imprint","INTERSECT",VERTEX,{"disambiguationData":[OD(0.0)],"derivedFrom":[subQ1,subQ0]});Q207=makeQuery(id+"F0.imprint","IMPRINT",FACE,{"disambiguationData":[TD([[makeQuery(id+"F0.imprint","IMPRINT",EDGE,{"disambiguationData":[TD([[subQ2,1.0]])],"derivedFrom":subQ1}),-1.0]])]});}
            var Q208;
            {var subQ0=sQuery(id+"F0.wireOp",EDGE,"E2.8.1.0");var subQ1=sQuery(id+"F0.wireOp",EDGE,"E2.7.1.0");var subQ2=makeQuery(id+"F0.imprint","INTERSECT",VERTEX,{"disambiguationData":[OD(0.0)],"derivedFrom":[subQ1,subQ0]});Q208=makeQuery(id+"F0.imprint","IMPRINT",FACE,{"disambiguationData":[TD([[makeQuery(id+"F0.imprint","IMPRINT",EDGE,{"disambiguationData":[TD([[subQ2,1.0]])],"derivedFrom":subQ1}),-1.0]])]});}
            var Q209;
            {var subQ0=sQuery(id+"F0.wireOp",EDGE,"E2.6.3.0");var subQ1=sQuery(id+"F0.wireOp",EDGE,"E2.5.3.0");var subQ2=makeQuery(id+"F0.imprint","INTERSECT",VERTEX,{"disambiguationData":[OD(0.0)],"derivedFrom":[subQ1,subQ0]});Q209=makeQuery(id+"F0.imprint","IMPRINT",FACE,{"disambiguationData":[TD([[makeQuery(id+"F0.imprint","IMPRINT",EDGE,{"disambiguationData":[TD([[subQ2,1.0]])],"derivedFrom":subQ1}),-1.0]])]});}
            var Q210;
            {var subQ0=sQuery(id+"F0.wireOp",EDGE,"E2.6.5.0");var subQ1=sQuery(id+"F0.wireOp",EDGE,"E2.5.5.0");var subQ2=makeQuery(id+"F0.imprint","INTERSECT",VERTEX,{"disambiguationData":[OD(0.0)],"derivedFrom":[subQ1,subQ0]});Q210=makeQuery(id+"F0.imprint","IMPRINT",FACE,{"disambiguationData":[TD([[makeQuery(id+"F0.imprint","IMPRINT",EDGE,{"disambiguationData":[TD([[subQ2,1.0]])],"derivedFrom":subQ1}),-1.0]])]});}
            var Q211;
            {var subQ0=sQuery(id+"F0.wireOp",EDGE,"E2.7.1.0");var subQ1=sQuery(id+"F0.wireOp",EDGE,"E2.6.1.0");var subQ2=makeQuery(id+"F0.imprint","INTERSECT",VERTEX,{"disambiguationData":[OD(0.0)],"derivedFrom":[subQ1,subQ0]});Q211=makeQuery(id+"F0.imprint","IMPRINT",FACE,{"disambiguationData":[TD([[makeQuery(id+"F0.imprint","IMPRINT",EDGE,{"disambiguationData":[TD([[subQ2,1.0]])],"derivedFrom":subQ1}),-1.0]])]});}
            var Q212;
            {var subQ0=sQuery(id+"F0.wireOp",EDGE,"E2.5.1.0");var subQ1=sQuery(id+"F0.wireOp",EDGE,"E2.4.1.0");var subQ2=makeQuery(id+"F0.imprint","INTERSECT",VERTEX,{"disambiguationData":[OD(0.0)],"derivedFrom":[subQ1,subQ0]});Q212=makeQuery(id+"F0.imprint","IMPRINT",FACE,{"disambiguationData":[TD([[makeQuery(id+"F0.imprint","IMPRINT",EDGE,{"disambiguationData":[TD([[subQ2,1.0]])],"derivedFrom":subQ1}),-1.0]])]});}
            var Q213;
            {var subQ0=sQuery(id+"F0.wireOp",EDGE,"E2.5.3.0");var subQ1=sQuery(id+"F0.wireOp",EDGE,"E2.4.3.0");var subQ2=makeQuery(id+"F0.imprint","INTERSECT",VERTEX,{"disambiguationData":[OD(0.0)],"derivedFrom":[subQ1,subQ0]});Q213=makeQuery(id+"F0.imprint","IMPRINT",FACE,{"disambiguationData":[TD([[makeQuery(id+"F0.imprint","IMPRINT",EDGE,{"disambiguationData":[TD([[subQ2,1.0]])],"derivedFrom":subQ1}),-1.0]])]});}
            var Q214;
            {var subQ0=sQuery(id+"F0.wireOp",EDGE,"E2.3.5.0");var subQ1=sQuery(id+"F0.wireOp",EDGE,"E2.2.5.0");var subQ2=makeQuery(id+"F0.imprint","INTERSECT",VERTEX,{"disambiguationData":[OD(0.0)],"derivedFrom":[subQ1,subQ0]});Q214=makeQuery(id+"F0.imprint","IMPRINT",FACE,{"disambiguationData":[TD([[makeQuery(id+"F0.imprint","IMPRINT",EDGE,{"disambiguationData":[TD([[subQ2,1.0]])],"derivedFrom":subQ1}),-1.0]])]});}
            var Q215;
            {var subQ0=sQuery(id+"F0.wireOp",EDGE,"E2.4.1.0");var subQ1=sQuery(id+"F0.wireOp",EDGE,"E2.3.1.0");var subQ2=makeQuery(id+"F0.imprint","INTERSECT",VERTEX,{"disambiguationData":[OD(0.0)],"derivedFrom":[subQ1,subQ0]});Q215=makeQuery(id+"F0.imprint","IMPRINT",FACE,{"disambiguationData":[TD([[makeQuery(id+"F0.imprint","IMPRINT",EDGE,{"disambiguationData":[TD([[subQ2,1.0]])],"derivedFrom":subQ1}),-1.0]])]});}
            var Q216;
            {var subQ0=sQuery(id+"F0.wireOp",EDGE,"E2.4.3.0");var subQ1=sQuery(id+"F0.wireOp",EDGE,"E2.3.3.0");var subQ2=makeQuery(id+"F0.imprint","INTERSECT",VERTEX,{"disambiguationData":[OD(0.0)],"derivedFrom":[subQ1,subQ0]});Q216=makeQuery(id+"F0.imprint","IMPRINT",FACE,{"disambiguationData":[TD([[makeQuery(id+"F0.imprint","IMPRINT",EDGE,{"disambiguationData":[TD([[subQ2,1.0]])],"derivedFrom":subQ1}),-1.0]])]});}
            var Q217;
            {var subQ0=sQuery(id+"F0.wireOp",EDGE,"E2.2.3.0");var subQ1=sQuery(id+"F0.wireOp",EDGE,"E2.1.3.0");var subQ2=makeQuery(id+"F0.imprint","INTERSECT",VERTEX,{"disambiguationData":[OD(0.0)],"derivedFrom":[subQ1,subQ0]});Q217=makeQuery(id+"F0.imprint","IMPRINT",FACE,{"disambiguationData":[TD([[makeQuery(id+"F0.imprint","IMPRINT",EDGE,{"disambiguationData":[TD([[subQ2,1.0]])],"derivedFrom":subQ1}),-1.0]])]});}
            var Q218;
            {var subQ0=sQuery(id+"F0.wireOp",EDGE,"E2.2.5.0");var subQ1=sQuery(id+"F0.wireOp",EDGE,"E2.1.5.0");var subQ2=makeQuery(id+"F0.imprint","INTERSECT",VERTEX,{"disambiguationData":[OD(0.0)],"derivedFrom":[subQ1,subQ0]});Q218=makeQuery(id+"F0.imprint","IMPRINT",FACE,{"disambiguationData":[TD([[makeQuery(id+"F0.imprint","IMPRINT",EDGE,{"disambiguationData":[TD([[subQ2,1.0]])],"derivedFrom":subQ1}),-1.0]])]});}
            var Q219;
            {var subQ0=sQuery(id+"F0.wireOp",EDGE,"E2.3.1.0");var subQ1=sQuery(id+"F0.wireOp",EDGE,"E2.2.1.0");var subQ2=makeQuery(id+"F0.imprint","INTERSECT",VERTEX,{"disambiguationData":[OD(0.0)],"derivedFrom":[subQ1,subQ0]});Q219=makeQuery(id+"F0.imprint","IMPRINT",FACE,{"disambiguationData":[TD([[makeQuery(id+"F0.imprint","IMPRINT",EDGE,{"disambiguationData":[TD([[subQ2,1.0]])],"derivedFrom":subQ1}),-1.0]])]});}
            var Q220;
            {var subQ0=sQuery(id+"F0.wireOp",EDGE,"E2.1.0.0");var subQ1=sQuery(id+"F0.wireOp",EDGE,"E1.0");var subQ2=makeQuery(id+"F0.imprint","INTERSECT",VERTEX,{"disambiguationData":[OD(1.0)],"derivedFrom":[subQ1,subQ0]});Q220=makeQuery(id+"F0.imprint","IMPRINT",FACE,{"disambiguationData":[TD([[makeQuery(id+"F0.imprint","IMPRINT",EDGE,{"disambiguationData":[TD([[subQ2,1.0]])],"derivedFrom":subQ1}),-1.0]])]});}
            var Q221;
            {var subQ0=sQuery(id+"F0.wireOp",EDGE,"E2.0.3.0");var subQ1=sQuery(id+"F0.wireOp",EDGE,"E2.0.2.0");var subQ2=makeQuery(id+"F0.imprint","INTERSECT",VERTEX,{"disambiguationData":[OD(1.0)],"derivedFrom":[subQ1,subQ0]});Q221=makeQuery(id+"F0.imprint","IMPRINT",FACE,{"disambiguationData":[TD([[makeQuery(id+"F0.imprint","IMPRINT",EDGE,{"disambiguationData":[TD([[subQ2,-1.0]])],"derivedFrom":subQ1}),-1.0]])]});}
            var Q222;
            {var subQ0=sQuery(id+"F0.wireOp",EDGE,"E2.2.1.0");var subQ1=sQuery(id+"F0.wireOp",EDGE,"E2.1.1.0");var subQ2=makeQuery(id+"F0.imprint","INTERSECT",VERTEX,{"disambiguationData":[OD(0.0)],"derivedFrom":[subQ1,subQ0]});Q222=makeQuery(id+"F0.imprint","IMPRINT",FACE,{"disambiguationData":[TD([[makeQuery(id+"F0.imprint","IMPRINT",EDGE,{"disambiguationData":[TD([[subQ2,1.0]])],"derivedFrom":subQ1}),-1.0]])]});}
            var Q223;
            {var subQ0=sQuery(id+"F0.wireOp",EDGE,"E2.10.3.0");var subQ1=sQuery(id+"F0.wireOp",EDGE,"E2.9.3.0");var subQ2=makeQuery(id+"F0.imprint","INTERSECT",VERTEX,{"disambiguationData":[OD(0.0)],"derivedFrom":[subQ1,subQ0]});Q223=makeQuery(id+"F0.imprint","IMPRINT",FACE,{"disambiguationData":[TD([[makeQuery(id+"F0.imprint","IMPRINT",EDGE,{"disambiguationData":[TD([[subQ2,1.0]])],"derivedFrom":subQ1}),1.0]])]});}
            var Q224;
            {var subQ0=sQuery(id+"F0.wireOp",EDGE,"E2.10.5.0");var subQ1=sQuery(id+"F0.wireOp",EDGE,"E2.9.5.0");var subQ2=makeQuery(id+"F0.imprint","INTERSECT",VERTEX,{"disambiguationData":[OD(0.0)],"derivedFrom":[subQ1,subQ0]});Q224=makeQuery(id+"F0.imprint","IMPRINT",FACE,{"disambiguationData":[TD([[makeQuery(id+"F0.imprint","IMPRINT",EDGE,{"disambiguationData":[TD([[subQ2,1.0]])],"derivedFrom":subQ1}),1.0]])]});}
            var Q225;
            {var subQ0=sQuery(id+"F0.wireOp",EDGE,"E2.9.1.0");var subQ1=sQuery(id+"F0.wireOp",EDGE,"E2.8.1.0");var subQ2=makeQuery(id+"F0.imprint","INTERSECT",VERTEX,{"disambiguationData":[OD(0.0)],"derivedFrom":[subQ1,subQ0]});Q225=makeQuery(id+"F0.imprint","IMPRINT",FACE,{"disambiguationData":[TD([[makeQuery(id+"F0.imprint","IMPRINT",EDGE,{"disambiguationData":[TD([[subQ2,1.0]])],"derivedFrom":subQ1}),1.0]])]});}
            var Q226;
            {var subQ0=sQuery(id+"F0.wireOp",EDGE,"E2.9.3.0");var subQ1=sQuery(id+"F0.wireOp",EDGE,"E2.8.3.0");var subQ2=makeQuery(id+"F0.imprint","INTERSECT",VERTEX,{"disambiguationData":[OD(0.0)],"derivedFrom":[subQ1,subQ0]});Q226=makeQuery(id+"F0.imprint","IMPRINT",FACE,{"disambiguationData":[TD([[makeQuery(id+"F0.imprint","IMPRINT",EDGE,{"disambiguationData":[TD([[subQ2,1.0]])],"derivedFrom":subQ1}),1.0]])]});}
            var Q227;
            {var subQ0=sQuery(id+"F0.wireOp",EDGE,"E2.9.5.0");var subQ1=sQuery(id+"F0.wireOp",EDGE,"E2.8.5.0");var subQ2=makeQuery(id+"F0.imprint","INTERSECT",VERTEX,{"disambiguationData":[OD(0.0)],"derivedFrom":[subQ1,subQ0]});Q227=makeQuery(id+"F0.imprint","IMPRINT",FACE,{"disambiguationData":[TD([[makeQuery(id+"F0.imprint","IMPRINT",EDGE,{"disambiguationData":[TD([[subQ2,1.0]])],"derivedFrom":subQ1}),1.0]])]});}
            var Q228;
            {var subQ0=sQuery(id+"F0.wireOp",EDGE,"E2.10.1.0");var subQ1=sQuery(id+"F0.wireOp",EDGE,"E2.9.1.0");var subQ2=makeQuery(id+"F0.imprint","INTERSECT",VERTEX,{"disambiguationData":[OD(0.0)],"derivedFrom":[subQ1,subQ0]});Q228=makeQuery(id+"F0.imprint","IMPRINT",FACE,{"disambiguationData":[TD([[makeQuery(id+"F0.imprint","IMPRINT",EDGE,{"disambiguationData":[TD([[subQ2,1.0]])],"derivedFrom":subQ1}),1.0]])]});}
            var Q229;
            {var subQ0=sQuery(id+"F0.wireOp",EDGE,"E2.8.3.0");var subQ1=sQuery(id+"F0.wireOp",EDGE,"E2.7.3.0");var subQ2=makeQuery(id+"F0.imprint","INTERSECT",VERTEX,{"disambiguationData":[OD(0.0)],"derivedFrom":[subQ1,subQ0]});Q229=makeQuery(id+"F0.imprint","IMPRINT",FACE,{"disambiguationData":[TD([[makeQuery(id+"F0.imprint","IMPRINT",EDGE,{"disambiguationData":[TD([[subQ2,1.0]])],"derivedFrom":subQ1}),1.0]])]});}
            var Q230;
            {var subQ0=sQuery(id+"F0.wireOp",EDGE,"E2.8.5.0");var subQ1=sQuery(id+"F0.wireOp",EDGE,"E2.7.5.0");var subQ2=makeQuery(id+"F0.imprint","INTERSECT",VERTEX,{"disambiguationData":[OD(0.0)],"derivedFrom":[subQ1,subQ0]});Q230=makeQuery(id+"F0.imprint","IMPRINT",FACE,{"disambiguationData":[TD([[makeQuery(id+"F0.imprint","IMPRINT",EDGE,{"disambiguationData":[TD([[subQ2,1.0]])],"derivedFrom":subQ1}),1.0]])]});}
            var Q231;
            {var subQ0=sQuery(id+"F0.wireOp",EDGE,"E2.7.1.0");var subQ1=sQuery(id+"F0.wireOp",EDGE,"E2.6.1.0");var subQ2=makeQuery(id+"F0.imprint","INTERSECT",VERTEX,{"disambiguationData":[OD(0.0)],"derivedFrom":[subQ1,subQ0]});Q231=makeQuery(id+"F0.imprint","IMPRINT",FACE,{"disambiguationData":[TD([[makeQuery(id+"F0.imprint","IMPRINT",EDGE,{"disambiguationData":[TD([[subQ2,1.0]])],"derivedFrom":subQ1}),1.0]])]});}
            var Q232;
            {var subQ0=sQuery(id+"F0.wireOp",EDGE,"E2.7.3.0");var subQ1=sQuery(id+"F0.wireOp",EDGE,"E2.6.3.0");var subQ2=makeQuery(id+"F0.imprint","INTERSECT",VERTEX,{"disambiguationData":[OD(0.0)],"derivedFrom":[subQ1,subQ0]});Q232=makeQuery(id+"F0.imprint","IMPRINT",FACE,{"disambiguationData":[TD([[makeQuery(id+"F0.imprint","IMPRINT",EDGE,{"disambiguationData":[TD([[subQ2,1.0]])],"derivedFrom":subQ1}),1.0]])]});}
            var Q233;
            {var subQ0=sQuery(id+"F0.wireOp",EDGE,"E2.7.5.0");var subQ1=sQuery(id+"F0.wireOp",EDGE,"E2.6.5.0");var subQ2=makeQuery(id+"F0.imprint","INTERSECT",VERTEX,{"disambiguationData":[OD(0.0)],"derivedFrom":[subQ1,subQ0]});Q233=makeQuery(id+"F0.imprint","IMPRINT",FACE,{"disambiguationData":[TD([[makeQuery(id+"F0.imprint","IMPRINT",EDGE,{"disambiguationData":[TD([[subQ2,1.0]])],"derivedFrom":subQ1}),1.0]])]});}
            var Q234;
            {var subQ0=sQuery(id+"F0.wireOp",EDGE,"E2.8.1.0");var subQ1=sQuery(id+"F0.wireOp",EDGE,"E2.7.1.0");var subQ2=makeQuery(id+"F0.imprint","INTERSECT",VERTEX,{"disambiguationData":[OD(0.0)],"derivedFrom":[subQ1,subQ0]});Q234=makeQuery(id+"F0.imprint","IMPRINT",FACE,{"disambiguationData":[TD([[makeQuery(id+"F0.imprint","IMPRINT",EDGE,{"disambiguationData":[TD([[subQ2,1.0]])],"derivedFrom":subQ1}),1.0]])]});}
            var Q235;
            {var subQ0=sQuery(id+"F0.wireOp",EDGE,"E2.5.5.0");var subQ1=sQuery(id+"F0.wireOp",EDGE,"E2.4.5.0");var subQ2=makeQuery(id+"F0.imprint","INTERSECT",VERTEX,{"disambiguationData":[OD(0.0)],"derivedFrom":[subQ1,subQ0]});Q235=makeQuery(id+"F0.imprint","IMPRINT",FACE,{"disambiguationData":[TD([[makeQuery(id+"F0.imprint","IMPRINT",EDGE,{"disambiguationData":[TD([[subQ2,1.0]])],"derivedFrom":subQ1}),1.0]])]});}
            var Q236;
            {var subQ0=sQuery(id+"F0.wireOp",EDGE,"E2.4.3.0");var subQ1=sQuery(id+"F0.wireOp",EDGE,"E2.3.3.0");var subQ2=makeQuery(id+"F0.imprint","INTERSECT",VERTEX,{"disambiguationData":[OD(0.0)],"derivedFrom":[subQ1,subQ0]});Q236=makeQuery(id+"F0.imprint","IMPRINT",FACE,{"disambiguationData":[TD([[makeQuery(id+"F0.imprint","IMPRINT",EDGE,{"disambiguationData":[TD([[subQ2,1.0]])],"derivedFrom":subQ1}),1.0]])]});}
            var Q237;
            {var subQ0=sQuery(id+"F0.wireOp",EDGE,"E2.4.5.0");var subQ1=sQuery(id+"F0.wireOp",EDGE,"E2.3.5.0");var subQ2=makeQuery(id+"F0.imprint","INTERSECT",VERTEX,{"disambiguationData":[OD(0.0)],"derivedFrom":[subQ1,subQ0]});Q237=makeQuery(id+"F0.imprint","IMPRINT",FACE,{"disambiguationData":[TD([[makeQuery(id+"F0.imprint","IMPRINT",EDGE,{"disambiguationData":[TD([[subQ2,1.0]])],"derivedFrom":subQ1}),1.0]])]});}
            var Q238;
            {var subQ0=sQuery(id+"F0.wireOp",EDGE,"E2.5.1.0");var subQ1=sQuery(id+"F0.wireOp",EDGE,"E2.4.1.0");var subQ2=makeQuery(id+"F0.imprint","INTERSECT",VERTEX,{"disambiguationData":[OD(0.0)],"derivedFrom":[subQ1,subQ0]});Q238=makeQuery(id+"F0.imprint","IMPRINT",FACE,{"disambiguationData":[TD([[makeQuery(id+"F0.imprint","IMPRINT",EDGE,{"disambiguationData":[TD([[subQ2,1.0]])],"derivedFrom":subQ1}),1.0]])]});}
            var Q239;
            {var subQ0=sQuery(id+"F0.wireOp",EDGE,"E2.5.3.0");var subQ1=sQuery(id+"F0.wireOp",EDGE,"E2.4.3.0");var subQ2=makeQuery(id+"F0.imprint","INTERSECT",VERTEX,{"disambiguationData":[OD(0.0)],"derivedFrom":[subQ1,subQ0]});Q239=makeQuery(id+"F0.imprint","IMPRINT",FACE,{"disambiguationData":[TD([[makeQuery(id+"F0.imprint","IMPRINT",EDGE,{"disambiguationData":[TD([[subQ2,1.0]])],"derivedFrom":subQ1}),1.0]])]});}
            var Q240;
            {var subQ0=sQuery(id+"F0.wireOp",EDGE,"E2.3.1.0");var subQ1=sQuery(id+"F0.wireOp",EDGE,"E2.2.1.0");var subQ2=makeQuery(id+"F0.imprint","INTERSECT",VERTEX,{"disambiguationData":[OD(0.0)],"derivedFrom":[subQ1,subQ0]});Q240=makeQuery(id+"F0.imprint","IMPRINT",FACE,{"disambiguationData":[TD([[makeQuery(id+"F0.imprint","IMPRINT",EDGE,{"disambiguationData":[TD([[subQ2,1.0]])],"derivedFrom":subQ1}),1.0]])]});}
            var Q241;
            {var subQ0=sQuery(id+"F0.wireOp",EDGE,"E2.3.3.0");var subQ1=sQuery(id+"F0.wireOp",EDGE,"E2.2.3.0");var subQ2=makeQuery(id+"F0.imprint","INTERSECT",VERTEX,{"disambiguationData":[OD(0.0)],"derivedFrom":[subQ1,subQ0]});Q241=makeQuery(id+"F0.imprint","IMPRINT",FACE,{"disambiguationData":[TD([[makeQuery(id+"F0.imprint","IMPRINT",EDGE,{"disambiguationData":[TD([[subQ2,1.0]])],"derivedFrom":subQ1}),1.0]])]});}
            var Q242;
            {var subQ0=sQuery(id+"F0.wireOp",EDGE,"E2.3.5.0");var subQ1=sQuery(id+"F0.wireOp",EDGE,"E2.2.5.0");var subQ2=makeQuery(id+"F0.imprint","INTERSECT",VERTEX,{"disambiguationData":[OD(0.0)],"derivedFrom":[subQ1,subQ0]});Q242=makeQuery(id+"F0.imprint","IMPRINT",FACE,{"disambiguationData":[TD([[makeQuery(id+"F0.imprint","IMPRINT",EDGE,{"disambiguationData":[TD([[subQ2,1.0]])],"derivedFrom":subQ1}),1.0]])]});}
            var Q243;
            {var subQ0=sQuery(id+"F0.wireOp",EDGE,"E2.4.1.0");var subQ1=sQuery(id+"F0.wireOp",EDGE,"E2.3.1.0");var subQ2=makeQuery(id+"F0.imprint","INTERSECT",VERTEX,{"disambiguationData":[OD(0.0)],"derivedFrom":[subQ1,subQ0]});Q243=makeQuery(id+"F0.imprint","IMPRINT",FACE,{"disambiguationData":[TD([[makeQuery(id+"F0.imprint","IMPRINT",EDGE,{"disambiguationData":[TD([[subQ2,1.0]])],"derivedFrom":subQ1}),1.0]])]});}
            var Q244;
            {var subQ0=sQuery(id+"F0.wireOp",EDGE,"E2.1.4.1");var subQ1=sQuery(id+"F0.wireOp",EDGE,"E2.0.4.0");var subQ2=makeQuery(id+"F0.imprint","INTERSECT",VERTEX,{"derivedFrom":[subQ1,subQ0]});Q244=makeQuery(id+"F0.imprint","IMPRINT",FACE,{"disambiguationData":[TD([[makeQuery(id+"F0.imprint","IMPRINT",EDGE,{"disambiguationData":[TD([[subQ2,1.0]])],"derivedFrom":subQ1}),-1.0]])]});}
            var Q245;
            {var subQ0=sQuery(id+"F0.wireOp",EDGE,"E2.2.1.0");var subQ1=sQuery(id+"F0.wireOp",EDGE,"E2.1.1.0");var subQ2=makeQuery(id+"F0.imprint","INTERSECT",VERTEX,{"disambiguationData":[OD(0.0)],"derivedFrom":[subQ1,subQ0]});Q245=makeQuery(id+"F0.imprint","IMPRINT",FACE,{"disambiguationData":[TD([[makeQuery(id+"F0.imprint","IMPRINT",EDGE,{"disambiguationData":[TD([[subQ2,1.0]])],"derivedFrom":subQ1}),1.0]])]});}
            var Q246;
            {var subQ0=sQuery(id+"F0.wireOp",EDGE,"E2.2.3.0");var subQ1=sQuery(id+"F0.wireOp",EDGE,"E2.1.3.0");var subQ2=makeQuery(id+"F0.imprint","INTERSECT",VERTEX,{"disambiguationData":[OD(0.0)],"derivedFrom":[subQ1,subQ0]});Q246=makeQuery(id+"F0.imprint","IMPRINT",FACE,{"disambiguationData":[TD([[makeQuery(id+"F0.imprint","IMPRINT",EDGE,{"disambiguationData":[TD([[subQ2,1.0]])],"derivedFrom":subQ1}),1.0]])]});}
            var Q247;
            {var subQ0=sQuery(id+"F0.wireOp",EDGE,"E2.2.5.0");var subQ1=sQuery(id+"F0.wireOp",EDGE,"E2.1.5.0");var subQ2=makeQuery(id+"F0.imprint","INTERSECT",VERTEX,{"disambiguationData":[OD(0.0)],"derivedFrom":[subQ1,subQ0]});Q247=makeQuery(id+"F0.imprint","IMPRINT",FACE,{"disambiguationData":[TD([[makeQuery(id+"F0.imprint","IMPRINT",EDGE,{"disambiguationData":[TD([[subQ2,1.0]])],"derivedFrom":subQ1}),1.0]])]});}
            var Q248;
            {var subQ0=sQuery(id+"F0.wireOp",EDGE,"E2.1.0.0");var subQ1=sQuery(id+"F0.wireOp",EDGE,"E1.0");var subQ2=makeQuery(id+"F0.imprint","INTERSECT",VERTEX,{"disambiguationData":[OD(1.0)],"derivedFrom":[subQ1,subQ0]});Q248=makeQuery(id+"F0.imprint","IMPRINT",FACE,{"disambiguationData":[TD([[makeQuery(id+"F0.imprint","IMPRINT",EDGE,{"disambiguationData":[TD([[subQ2,1.0]])],"derivedFrom":subQ1}),1.0]])]});}
            var Q249;
            {var subQ0=sQuery(id+"F0.wireOp",EDGE,"E2.0.3.0");var subQ1=sQuery(id+"F0.wireOp",EDGE,"E2.0.2.0");var subQ2=makeQuery(id+"F0.imprint","INTERSECT",VERTEX,{"disambiguationData":[OD(1.0)],"derivedFrom":[subQ1,subQ0]});Q249=makeQuery(id+"F0.imprint","IMPRINT",FACE,{"disambiguationData":[TD([[makeQuery(id+"F0.imprint","IMPRINT",EDGE,{"disambiguationData":[TD([[subQ2,-1.0]])],"derivedFrom":subQ1}),1.0]])]});}
            var Q250;
            {var subQ0=sQuery(id+"F0.wireOp",EDGE,"E2.11.6.0");var subQ1=sQuery(id+"F0.wireOp",EDGE,"E2.11.5.0");var subQ2=makeQuery(id+"F0.imprint","INTERSECT",VERTEX,{"disambiguationData":[OD(0.0)],"derivedFrom":[subQ1,subQ0]});Q250=makeQuery(id+"F0.imprint","IMPRINT",FACE,{"disambiguationData":[TD([[makeQuery(id+"F0.imprint","IMPRINT",EDGE,{"disambiguationData":[TD([[subQ2,-1.0]])],"derivedFrom":subQ1}),1.0]])]});}
            var Q251;
            {var subQ0=sQuery(id+"F0.wireOp",EDGE,"E2.8.1.0");var subQ1=sQuery(id+"F0.wireOp",EDGE,"E2.8.0.0");var subQ2=makeQuery(id+"F0.imprint","INTERSECT",VERTEX,{"disambiguationData":[OD(0.0)],"derivedFrom":[subQ1,subQ0]});Q251=makeQuery(id+"F0.imprint","IMPRINT",FACE,{"disambiguationData":[TD([[makeQuery(id+"F0.imprint","IMPRINT",EDGE,{"disambiguationData":[TD([[subQ2,-1.0]])],"derivedFrom":subQ1}),-1.0]])]});}
            var Q252;
            {var subQ0=sQuery(id+"F0.wireOp",EDGE,"E2.9.1.0");var subQ1=sQuery(id+"F0.wireOp",EDGE,"E2.9.0.0");var subQ2=makeQuery(id+"F0.imprint","INTERSECT",VERTEX,{"disambiguationData":[OD(0.0)],"derivedFrom":[subQ1,subQ0]});Q252=makeQuery(id+"F0.imprint","IMPRINT",FACE,{"disambiguationData":[TD([[makeQuery(id+"F0.imprint","IMPRINT",EDGE,{"disambiguationData":[TD([[subQ2,-1.0]])],"derivedFrom":subQ1}),-1.0]])]});}
            var Q253;
            {var subQ0=sQuery(id+"F0.wireOp",EDGE,"E2.6.1.0");var subQ1=sQuery(id+"F0.wireOp",EDGE,"E2.6.0.0");var subQ2=makeQuery(id+"F0.imprint","INTERSECT",VERTEX,{"disambiguationData":[OD(0.0)],"derivedFrom":[subQ1,subQ0]});Q253=makeQuery(id+"F0.imprint","IMPRINT",FACE,{"disambiguationData":[TD([[makeQuery(id+"F0.imprint","IMPRINT",EDGE,{"disambiguationData":[TD([[subQ2,-1.0]])],"derivedFrom":subQ1}),-1.0]])]});}
            var Q254;
            {var subQ0=sQuery(id+"F0.wireOp",EDGE,"E2.7.1.0");var subQ1=sQuery(id+"F0.wireOp",EDGE,"E2.7.0.0");var subQ2=makeQuery(id+"F0.imprint","INTERSECT",VERTEX,{"disambiguationData":[OD(0.0)],"derivedFrom":[subQ1,subQ0]});Q254=makeQuery(id+"F0.imprint","IMPRINT",FACE,{"disambiguationData":[TD([[makeQuery(id+"F0.imprint","IMPRINT",EDGE,{"disambiguationData":[TD([[subQ2,-1.0]])],"derivedFrom":subQ1}),-1.0]])]});}
            var Q255;
            {var subQ0=sQuery(id+"F0.wireOp",EDGE,"E2.4.1.0");var subQ1=sQuery(id+"F0.wireOp",EDGE,"E2.4.0.0");var subQ2=makeQuery(id+"F0.imprint","INTERSECT",VERTEX,{"disambiguationData":[OD(0.0)],"derivedFrom":[subQ1,subQ0]});Q255=makeQuery(id+"F0.imprint","IMPRINT",FACE,{"disambiguationData":[TD([[makeQuery(id+"F0.imprint","IMPRINT",EDGE,{"disambiguationData":[TD([[subQ2,-1.0]])],"derivedFrom":subQ1}),-1.0]])]});}
            var Q256;
            {var subQ0=sQuery(id+"F0.wireOp",EDGE,"E2.2.1.0");var subQ1=sQuery(id+"F0.wireOp",EDGE,"E2.2.0.0");var subQ2=makeQuery(id+"F0.imprint","INTERSECT",VERTEX,{"disambiguationData":[OD(0.0)],"derivedFrom":[subQ1,subQ0]});Q256=makeQuery(id+"F0.imprint","IMPRINT",FACE,{"disambiguationData":[TD([[makeQuery(id+"F0.imprint","IMPRINT",EDGE,{"disambiguationData":[TD([[subQ2,-1.0]])],"derivedFrom":subQ1}),-1.0]])]});}
            var Q257;
            {var subQ0=sQuery(id+"F0.wireOp",EDGE,"E2.3.1.0");var subQ1=sQuery(id+"F0.wireOp",EDGE,"E2.3.0.0");var subQ2=makeQuery(id+"F0.imprint","INTERSECT",VERTEX,{"disambiguationData":[OD(0.0)],"derivedFrom":[subQ1,subQ0]});Q257=makeQuery(id+"F0.imprint","IMPRINT",FACE,{"disambiguationData":[TD([[makeQuery(id+"F0.imprint","IMPRINT",EDGE,{"disambiguationData":[TD([[subQ2,-1.0]])],"derivedFrom":subQ1}),-1.0]])]});}
            var Q258;
            {var subQ0=sQuery(id+"F0.wireOp",EDGE,"E2.0.5.0");var subQ1=sQuery(id+"F0.wireOp",EDGE,"E2.0.4.0");var subQ2=makeQuery(id+"F0.imprint","INTERSECT",VERTEX,{"disambiguationData":[OD(1.0)],"derivedFrom":[subQ1,subQ0]});Q258=makeQuery(id+"F0.imprint","IMPRINT",FACE,{"disambiguationData":[TD([[makeQuery(id+"F0.imprint","IMPRINT",EDGE,{"disambiguationData":[TD([[subQ2,-1.0]])],"derivedFrom":subQ1}),-1.0]])]});}
            var Q259;
            {var subQ0=sQuery(id+"F0.wireOp",EDGE,"E2.1.1.0");var subQ1=sQuery(id+"F0.wireOp",EDGE,"E2.1.0.0");var subQ2=makeQuery(id+"F0.imprint","INTERSECT",VERTEX,{"disambiguationData":[OD(0.0)],"derivedFrom":[subQ1,subQ0]});Q259=makeQuery(id+"F0.imprint","IMPRINT",FACE,{"disambiguationData":[TD([[makeQuery(id+"F0.imprint","IMPRINT",EDGE,{"disambiguationData":[TD([[subQ2,-1.0]])],"derivedFrom":subQ1}),-1.0]])]});}
            var Q260;
            {var subQ0=sQuery(id+"F0.wireOp",EDGE,"E2.0.1.0");var subQ1=sQuery(id+"F0.wireOp",EDGE,"E0");var subQ2=makeQuery(id+"F0.imprint","INTERSECT",VERTEX,{"derivedFrom":[subQ1,subQ0]});Q260=makeQuery(id+"F0.imprint","IMPRINT",FACE,{"disambiguationData":[TD([[makeQuery(id+"F0.imprint","IMPRINT",EDGE,{"disambiguationData":[TD([[subQ2,1.0]])],"derivedFrom":subQ1}),-1.0]])]});}
            var Q261;
            {var subQ0=sQuery(id+"F0.wireOp",EDGE,"E2.2.6.0");var subQ1=sQuery(id+"F0.wireOp",EDGE,"E2.1.6.0");var subQ2=makeQuery(id+"F0.imprint","INTERSECT",VERTEX,{"disambiguationData":[OD(0.0)],"derivedFrom":[subQ1,subQ0]});Q261=makeQuery(id+"F0.imprint","IMPRINT",FACE,{"disambiguationData":[TD([[makeQuery(id+"F0.imprint","IMPRINT",EDGE,{"disambiguationData":[TD([[subQ2,1.0]])],"derivedFrom":subQ1}),-1.0]])]});}
            var Q262;
            {var subQ0=sQuery(id+"F0.wireOp",EDGE,"E2.11.4.1");var subQ1=sQuery(id+"F0.wireOp",EDGE,"E2.10.4.0");var subQ2=makeQuery(id+"F0.imprint","INTERSECT",VERTEX,{"derivedFrom":[subQ1,subQ0]});Q262=makeQuery(id+"F0.imprint","IMPRINT",FACE,{"disambiguationData":[TD([[makeQuery(id+"F0.imprint","IMPRINT",EDGE,{"disambiguationData":[TD([[subQ2,1.0]])],"derivedFrom":subQ1}),-1.0]])]});}
            var Q263;
            {var subQ0=sQuery(id+"F0.wireOp",EDGE,"E2.11.5.0");var subQ1=sQuery(id+"F0.wireOp",EDGE,"E2.11.4.0");var subQ2=makeQuery(id+"F0.imprint","INTERSECT",VERTEX,{"disambiguationData":[OD(0.0)],"derivedFrom":[subQ1,subQ0]});Q263=makeQuery(id+"F0.imprint","IMPRINT",FACE,{"disambiguationData":[TD([[makeQuery(id+"F0.imprint","IMPRINT",EDGE,{"disambiguationData":[TD([[subQ2,-1.0]])],"derivedFrom":subQ1}),1.0]])]});}
            var Q264;
            {var subQ0=sQuery(id+"F0.wireOp",EDGE,"E2.10.2.1");var subQ1=sQuery(id+"F0.wireOp",EDGE,"E2.9.2.0");var subQ2=makeQuery(id+"F0.imprint","INTERSECT",VERTEX,{"derivedFrom":[subQ1,subQ0]});Q264=makeQuery(id+"F0.imprint","IMPRINT",FACE,{"disambiguationData":[TD([[makeQuery(id+"F0.imprint","IMPRINT",EDGE,{"disambiguationData":[TD([[subQ2,1.0]])],"derivedFrom":subQ1}),-1.0]])]});}
            var Q265;
            {var subQ0=sQuery(id+"F0.wireOp",EDGE,"E2.10.4.1");var subQ1=sQuery(id+"F0.wireOp",EDGE,"E2.9.4.0");var subQ2=makeQuery(id+"F0.imprint","INTERSECT",VERTEX,{"derivedFrom":[subQ1,subQ0]});Q265=makeQuery(id+"F0.imprint","IMPRINT",FACE,{"disambiguationData":[TD([[makeQuery(id+"F0.imprint","IMPRINT",EDGE,{"disambiguationData":[TD([[subQ2,1.0]])],"derivedFrom":subQ1}),-1.0]])]});}
            var Q266;
            {var subQ0=sQuery(id+"F0.wireOp",EDGE,"E2.10.1.0");var subQ1=sQuery(id+"F0.wireOp",EDGE,"E2.10.0.0");var subQ2=makeQuery(id+"F0.imprint","INTERSECT",VERTEX,{"disambiguationData":[OD(0.0)],"derivedFrom":[subQ1,subQ0]});Q266=makeQuery(id+"F0.imprint","IMPRINT",FACE,{"disambiguationData":[TD([[makeQuery(id+"F0.imprint","IMPRINT",EDGE,{"disambiguationData":[TD([[subQ2,-1.0]])],"derivedFrom":subQ1}),1.0]])]});}
            var Q267;
            {var subQ0=sQuery(id+"F0.wireOp",EDGE,"E2.11.2.1");var subQ1=sQuery(id+"F0.wireOp",EDGE,"E2.10.2.0");var subQ2=makeQuery(id+"F0.imprint","INTERSECT",VERTEX,{"derivedFrom":[subQ1,subQ0]});Q267=makeQuery(id+"F0.imprint","IMPRINT",FACE,{"disambiguationData":[TD([[makeQuery(id+"F0.imprint","IMPRINT",EDGE,{"disambiguationData":[TD([[subQ2,1.0]])],"derivedFrom":subQ1}),-1.0]])]});}
            var Q268;
            {var subQ0=sQuery(id+"F0.wireOp",EDGE,"E2.8.1.0");var subQ1=sQuery(id+"F0.wireOp",EDGE,"E2.8.0.0");var subQ2=makeQuery(id+"F0.imprint","INTERSECT",VERTEX,{"disambiguationData":[OD(0.0)],"derivedFrom":[subQ1,subQ0]});Q268=makeQuery(id+"F0.imprint","IMPRINT",FACE,{"disambiguationData":[TD([[makeQuery(id+"F0.imprint","IMPRINT",EDGE,{"disambiguationData":[TD([[subQ2,-1.0]])],"derivedFrom":subQ1}),1.0]])]});}
            var Q269;
            {var subQ0=sQuery(id+"F0.wireOp",EDGE,"E2.9.2.1");var subQ1=sQuery(id+"F0.wireOp",EDGE,"E2.8.2.0");var subQ2=makeQuery(id+"F0.imprint","INTERSECT",VERTEX,{"derivedFrom":[subQ1,subQ0]});Q269=makeQuery(id+"F0.imprint","IMPRINT",FACE,{"disambiguationData":[TD([[makeQuery(id+"F0.imprint","IMPRINT",EDGE,{"disambiguationData":[TD([[subQ2,1.0]])],"derivedFrom":subQ1}),-1.0]])]});}
            var Q270;
            {var subQ0=sQuery(id+"F0.wireOp",EDGE,"E2.9.4.1");var subQ1=sQuery(id+"F0.wireOp",EDGE,"E2.8.4.0");var subQ2=makeQuery(id+"F0.imprint","INTERSECT",VERTEX,{"derivedFrom":[subQ1,subQ0]});Q270=makeQuery(id+"F0.imprint","IMPRINT",FACE,{"disambiguationData":[TD([[makeQuery(id+"F0.imprint","IMPRINT",EDGE,{"disambiguationData":[TD([[subQ2,1.0]])],"derivedFrom":subQ1}),-1.0]])]});}
            var Q271;
            {var subQ0=sQuery(id+"F0.wireOp",EDGE,"E2.9.1.0");var subQ1=sQuery(id+"F0.wireOp",EDGE,"E2.9.0.0");var subQ2=makeQuery(id+"F0.imprint","INTERSECT",VERTEX,{"disambiguationData":[OD(0.0)],"derivedFrom":[subQ1,subQ0]});Q271=makeQuery(id+"F0.imprint","IMPRINT",FACE,{"disambiguationData":[TD([[makeQuery(id+"F0.imprint","IMPRINT",EDGE,{"disambiguationData":[TD([[subQ2,-1.0]])],"derivedFrom":subQ1}),1.0]])]});}
            var Q272;
            {var subQ0=sQuery(id+"F0.wireOp",EDGE,"E2.8.2.1");var subQ1=sQuery(id+"F0.wireOp",EDGE,"E2.7.2.0");var subQ2=makeQuery(id+"F0.imprint","INTERSECT",VERTEX,{"derivedFrom":[subQ1,subQ0]});Q272=makeQuery(id+"F0.imprint","IMPRINT",FACE,{"disambiguationData":[TD([[makeQuery(id+"F0.imprint","IMPRINT",EDGE,{"disambiguationData":[TD([[subQ2,1.0]])],"derivedFrom":subQ1}),-1.0]])]});}
            var Q273;
            {var subQ0=sQuery(id+"F0.wireOp",EDGE,"E2.8.4.1");var subQ1=sQuery(id+"F0.wireOp",EDGE,"E2.7.4.0");var subQ2=makeQuery(id+"F0.imprint","INTERSECT",VERTEX,{"derivedFrom":[subQ1,subQ0]});Q273=makeQuery(id+"F0.imprint","IMPRINT",FACE,{"disambiguationData":[TD([[makeQuery(id+"F0.imprint","IMPRINT",EDGE,{"disambiguationData":[TD([[subQ2,1.0]])],"derivedFrom":subQ1}),-1.0]])]});}
            var Q274;
            {var subQ0=sQuery(id+"F0.wireOp",EDGE,"E2.6.1.0");var subQ1=sQuery(id+"F0.wireOp",EDGE,"E2.6.0.0");var subQ2=makeQuery(id+"F0.imprint","INTERSECT",VERTEX,{"disambiguationData":[OD(0.0)],"derivedFrom":[subQ1,subQ0]});Q274=makeQuery(id+"F0.imprint","IMPRINT",FACE,{"disambiguationData":[TD([[makeQuery(id+"F0.imprint","IMPRINT",EDGE,{"disambiguationData":[TD([[subQ2,-1.0]])],"derivedFrom":subQ1}),1.0]])]});}
            var Q275;
            {var subQ0=sQuery(id+"F0.wireOp",EDGE,"E2.7.2.1");var subQ1=sQuery(id+"F0.wireOp",EDGE,"E2.6.2.0");var subQ2=makeQuery(id+"F0.imprint","INTERSECT",VERTEX,{"derivedFrom":[subQ1,subQ0]});Q275=makeQuery(id+"F0.imprint","IMPRINT",FACE,{"disambiguationData":[TD([[makeQuery(id+"F0.imprint","IMPRINT",EDGE,{"disambiguationData":[TD([[subQ2,1.0]])],"derivedFrom":subQ1}),-1.0]])]});}
            var Q276;
            {var subQ0=sQuery(id+"F0.wireOp",EDGE,"E2.7.1.0");var subQ1=sQuery(id+"F0.wireOp",EDGE,"E2.7.0.0");var subQ2=makeQuery(id+"F0.imprint","INTERSECT",VERTEX,{"disambiguationData":[OD(0.0)],"derivedFrom":[subQ1,subQ0]});Q276=makeQuery(id+"F0.imprint","IMPRINT",FACE,{"disambiguationData":[TD([[makeQuery(id+"F0.imprint","IMPRINT",EDGE,{"disambiguationData":[TD([[subQ2,-1.0]])],"derivedFrom":subQ1}),1.0]])]});}
            var Q277;
            {var subQ0=sQuery(id+"F0.wireOp",EDGE,"E2.5.4.1");var subQ1=sQuery(id+"F0.wireOp",EDGE,"E2.4.4.0");var subQ2=makeQuery(id+"F0.imprint","INTERSECT",VERTEX,{"derivedFrom":[subQ1,subQ0]});Q277=makeQuery(id+"F0.imprint","IMPRINT",FACE,{"disambiguationData":[TD([[makeQuery(id+"F0.imprint","IMPRINT",EDGE,{"disambiguationData":[TD([[subQ2,1.0]])],"derivedFrom":subQ1}),-1.0]])]});}
            var Q278;
            {var subQ0=sQuery(id+"F0.wireOp",EDGE,"E2.5.1.0");var subQ1=sQuery(id+"F0.wireOp",EDGE,"E2.5.0.0");var subQ2=makeQuery(id+"F0.imprint","INTERSECT",VERTEX,{"disambiguationData":[OD(0.0)],"derivedFrom":[subQ1,subQ0]});Q278=makeQuery(id+"F0.imprint","IMPRINT",FACE,{"disambiguationData":[TD([[makeQuery(id+"F0.imprint","IMPRINT",EDGE,{"disambiguationData":[TD([[subQ2,-1.0]])],"derivedFrom":subQ1}),1.0]])]});}
            var Q279;
            {var subQ0=sQuery(id+"F0.wireOp",EDGE,"E2.6.2.1");var subQ1=sQuery(id+"F0.wireOp",EDGE,"E2.5.2.0");var subQ2=makeQuery(id+"F0.imprint","INTERSECT",VERTEX,{"derivedFrom":[subQ1,subQ0]});Q279=makeQuery(id+"F0.imprint","IMPRINT",FACE,{"disambiguationData":[TD([[makeQuery(id+"F0.imprint","IMPRINT",EDGE,{"disambiguationData":[TD([[subQ2,1.0]])],"derivedFrom":subQ1}),-1.0]])]});}
            var Q280;
            {var subQ0=sQuery(id+"F0.wireOp",EDGE,"E2.6.4.1");var subQ1=sQuery(id+"F0.wireOp",EDGE,"E2.5.4.0");var subQ2=makeQuery(id+"F0.imprint","INTERSECT",VERTEX,{"derivedFrom":[subQ1,subQ0]});Q280=makeQuery(id+"F0.imprint","IMPRINT",FACE,{"disambiguationData":[TD([[makeQuery(id+"F0.imprint","IMPRINT",EDGE,{"disambiguationData":[TD([[subQ2,1.0]])],"derivedFrom":subQ1}),-1.0]])]});}
            var Q281;
            {var subQ0=sQuery(id+"F0.wireOp",EDGE,"E2.4.2.1");var subQ1=sQuery(id+"F0.wireOp",EDGE,"E2.3.2.0");var subQ2=makeQuery(id+"F0.imprint","INTERSECT",VERTEX,{"derivedFrom":[subQ1,subQ0]});Q281=makeQuery(id+"F0.imprint","IMPRINT",FACE,{"disambiguationData":[TD([[makeQuery(id+"F0.imprint","IMPRINT",EDGE,{"disambiguationData":[TD([[subQ2,1.0]])],"derivedFrom":subQ1}),-1.0]])]});}
            var Q282;
            {var subQ0=sQuery(id+"F0.wireOp",EDGE,"E2.4.4.1");var subQ1=sQuery(id+"F0.wireOp",EDGE,"E2.3.4.0");var subQ2=makeQuery(id+"F0.imprint","INTERSECT",VERTEX,{"derivedFrom":[subQ1,subQ0]});Q282=makeQuery(id+"F0.imprint","IMPRINT",FACE,{"disambiguationData":[TD([[makeQuery(id+"F0.imprint","IMPRINT",EDGE,{"disambiguationData":[TD([[subQ2,1.0]])],"derivedFrom":subQ1}),-1.0]])]});}
            var Q283;
            {var subQ0=sQuery(id+"F0.wireOp",EDGE,"E2.4.1.0");var subQ1=sQuery(id+"F0.wireOp",EDGE,"E2.4.0.0");var subQ2=makeQuery(id+"F0.imprint","INTERSECT",VERTEX,{"disambiguationData":[OD(0.0)],"derivedFrom":[subQ1,subQ0]});Q283=makeQuery(id+"F0.imprint","IMPRINT",FACE,{"disambiguationData":[TD([[makeQuery(id+"F0.imprint","IMPRINT",EDGE,{"disambiguationData":[TD([[subQ2,-1.0]])],"derivedFrom":subQ1}),1.0]])]});}
            var Q284;
            {var subQ0=sQuery(id+"F0.wireOp",EDGE,"E2.5.2.1");var subQ1=sQuery(id+"F0.wireOp",EDGE,"E2.4.2.0");var subQ2=makeQuery(id+"F0.imprint","INTERSECT",VERTEX,{"derivedFrom":[subQ1,subQ0]});Q284=makeQuery(id+"F0.imprint","IMPRINT",FACE,{"disambiguationData":[TD([[makeQuery(id+"F0.imprint","IMPRINT",EDGE,{"disambiguationData":[TD([[subQ2,1.0]])],"derivedFrom":subQ1}),-1.0]])]});}
            var Q285;
            {var subQ0=sQuery(id+"F0.wireOp",EDGE,"E2.2.1.0");var subQ1=sQuery(id+"F0.wireOp",EDGE,"E2.2.0.0");var subQ2=makeQuery(id+"F0.imprint","INTERSECT",VERTEX,{"disambiguationData":[OD(0.0)],"derivedFrom":[subQ1,subQ0]});Q285=makeQuery(id+"F0.imprint","IMPRINT",FACE,{"disambiguationData":[TD([[makeQuery(id+"F0.imprint","IMPRINT",EDGE,{"disambiguationData":[TD([[subQ2,-1.0]])],"derivedFrom":subQ1}),1.0]])]});}
            var Q286;
            {var subQ0=sQuery(id+"F0.wireOp",EDGE,"E2.3.2.1");var subQ1=sQuery(id+"F0.wireOp",EDGE,"E2.2.2.0");var subQ2=makeQuery(id+"F0.imprint","INTERSECT",VERTEX,{"derivedFrom":[subQ1,subQ0]});Q286=makeQuery(id+"F0.imprint","IMPRINT",FACE,{"disambiguationData":[TD([[makeQuery(id+"F0.imprint","IMPRINT",EDGE,{"disambiguationData":[TD([[subQ2,1.0]])],"derivedFrom":subQ1}),-1.0]])]});}
            var Q287;
            {var subQ0=sQuery(id+"F0.wireOp",EDGE,"E2.3.4.1");var subQ1=sQuery(id+"F0.wireOp",EDGE,"E2.2.4.0");var subQ2=makeQuery(id+"F0.imprint","INTERSECT",VERTEX,{"derivedFrom":[subQ1,subQ0]});Q287=makeQuery(id+"F0.imprint","IMPRINT",FACE,{"disambiguationData":[TD([[makeQuery(id+"F0.imprint","IMPRINT",EDGE,{"disambiguationData":[TD([[subQ2,1.0]])],"derivedFrom":subQ1}),-1.0]])]});}
            var Q288;
            {var subQ0=sQuery(id+"F0.wireOp",EDGE,"E2.3.1.0");var subQ1=sQuery(id+"F0.wireOp",EDGE,"E2.3.0.0");var subQ2=makeQuery(id+"F0.imprint","INTERSECT",VERTEX,{"disambiguationData":[OD(0.0)],"derivedFrom":[subQ1,subQ0]});Q288=makeQuery(id+"F0.imprint","IMPRINT",FACE,{"disambiguationData":[TD([[makeQuery(id+"F0.imprint","IMPRINT",EDGE,{"disambiguationData":[TD([[subQ2,-1.0]])],"derivedFrom":subQ1}),1.0]])]});}
            var Q289;
            {var subQ0=sQuery(id+"F0.wireOp",EDGE,"E2.0.5.0");var subQ1=sQuery(id+"F0.wireOp",EDGE,"E2.0.4.0");var subQ2=makeQuery(id+"F0.imprint","INTERSECT",VERTEX,{"disambiguationData":[OD(1.0)],"derivedFrom":[subQ1,subQ0]});Q289=makeQuery(id+"F0.imprint","IMPRINT",FACE,{"disambiguationData":[TD([[makeQuery(id+"F0.imprint","IMPRINT",EDGE,{"disambiguationData":[TD([[subQ2,-1.0]])],"derivedFrom":subQ1}),1.0]])]});}
            var Q290;
            {var subQ0=sQuery(id+"F0.wireOp",EDGE,"E2.1.1.0");var subQ1=sQuery(id+"F0.wireOp",EDGE,"E2.1.0.0");var subQ2=makeQuery(id+"F0.imprint","INTERSECT",VERTEX,{"disambiguationData":[OD(0.0)],"derivedFrom":[subQ1,subQ0]});Q290=makeQuery(id+"F0.imprint","IMPRINT",FACE,{"disambiguationData":[TD([[makeQuery(id+"F0.imprint","IMPRINT",EDGE,{"disambiguationData":[TD([[subQ2,-1.0]])],"derivedFrom":subQ1}),1.0]])]});}
            var Q291;
            {var subQ0=sQuery(id+"F0.wireOp",EDGE,"E2.2.2.1");var subQ1=sQuery(id+"F0.wireOp",EDGE,"E2.1.2.0");var subQ2=makeQuery(id+"F0.imprint","INTERSECT",VERTEX,{"derivedFrom":[subQ1,subQ0]});Q291=makeQuery(id+"F0.imprint","IMPRINT",FACE,{"disambiguationData":[TD([[makeQuery(id+"F0.imprint","IMPRINT",EDGE,{"disambiguationData":[TD([[subQ2,1.0]])],"derivedFrom":subQ1}),-1.0]])]});}
            var Q292;
            {var subQ0=sQuery(id+"F0.wireOp",EDGE,"E2.2.4.1");var subQ1=sQuery(id+"F0.wireOp",EDGE,"E2.1.4.0");var subQ2=makeQuery(id+"F0.imprint","INTERSECT",VERTEX,{"derivedFrom":[subQ1,subQ0]});Q292=makeQuery(id+"F0.imprint","IMPRINT",FACE,{"disambiguationData":[TD([[makeQuery(id+"F0.imprint","IMPRINT",EDGE,{"disambiguationData":[TD([[subQ2,1.0]])],"derivedFrom":subQ1}),-1.0]])]});}
            var Q293;
            {var subQ0=sQuery(id+"F0.wireOp",EDGE,"E2.1.2.0");var subQ1=sQuery(id+"F0.wireOp",EDGE,"E2.0.2.0");var subQ2=makeQuery(id+"F0.imprint","INTERSECT",VERTEX,{"disambiguationData":[OD(0.0)],"derivedFrom":[subQ1,subQ0]});Q293=makeQuery(id+"F0.imprint","IMPRINT",FACE,{"disambiguationData":[TD([[makeQuery(id+"F0.imprint","IMPRINT",EDGE,{"disambiguationData":[TD([[subQ2,-1.0]])],"derivedFrom":subQ1}),1.0]])]});}
            var Q294;
            {var subQ0=sQuery(id+"F0.wireOp",EDGE,"E2.10.5.0");var subQ1=sQuery(id+"F0.wireOp",EDGE,"E2.10.4.0");var subQ2=makeQuery(id+"F0.imprint","INTERSECT",VERTEX,{"disambiguationData":[OD(0.0)],"derivedFrom":[subQ1,subQ0]});Q294=makeQuery(id+"F0.imprint","IMPRINT",FACE,{"disambiguationData":[TD([[makeQuery(id+"F0.imprint","IMPRINT",EDGE,{"disambiguationData":[TD([[subQ2,-1.0]])],"derivedFrom":subQ1}),-1.0]])]});}
            var Q295;
            {var subQ0=sQuery(id+"F0.wireOp",EDGE,"E2.11.4.0");var subQ1=sQuery(id+"F0.wireOp",EDGE,"E2.11.3.0");var subQ2=makeQuery(id+"F0.imprint","INTERSECT",VERTEX,{"disambiguationData":[OD(0.0)],"derivedFrom":[subQ1,subQ0]});Q295=makeQuery(id+"F0.imprint","IMPRINT",FACE,{"disambiguationData":[TD([[makeQuery(id+"F0.imprint","IMPRINT",EDGE,{"disambiguationData":[TD([[subQ2,-1.0]])],"derivedFrom":subQ1}),1.0]])]});}
            var Q296;
            {var subQ0=sQuery(id+"F0.wireOp",EDGE,"E2.9.3.0");var subQ1=sQuery(id+"F0.wireOp",EDGE,"E2.9.2.0");var subQ2=makeQuery(id+"F0.imprint","INTERSECT",VERTEX,{"disambiguationData":[OD(0.0)],"derivedFrom":[subQ1,subQ0]});Q296=makeQuery(id+"F0.imprint","IMPRINT",FACE,{"disambiguationData":[TD([[makeQuery(id+"F0.imprint","IMPRINT",EDGE,{"disambiguationData":[TD([[subQ2,-1.0]])],"derivedFrom":subQ1}),-1.0]])]});}
            var Q297;
            {var subQ0=sQuery(id+"F0.wireOp",EDGE,"E2.10.3.0");var subQ1=sQuery(id+"F0.wireOp",EDGE,"E2.10.2.0");var subQ2=makeQuery(id+"F0.imprint","INTERSECT",VERTEX,{"disambiguationData":[OD(0.0)],"derivedFrom":[subQ1,subQ0]});Q297=makeQuery(id+"F0.imprint","IMPRINT",FACE,{"disambiguationData":[TD([[makeQuery(id+"F0.imprint","IMPRINT",EDGE,{"disambiguationData":[TD([[subQ2,-1.0]])],"derivedFrom":subQ1}),-1.0]])]});}
            var Q298;
            {var subQ0=sQuery(id+"F0.wireOp",EDGE,"E2.2.6.0");var subQ1=sQuery(id+"F0.wireOp",EDGE,"E2.2.5.0");var subQ2=makeQuery(id+"F0.imprint","INTERSECT",VERTEX,{"disambiguationData":[OD(0.0)],"derivedFrom":[subQ1,subQ0]});Q298=makeQuery(id+"F0.imprint","IMPRINT",FACE,{"disambiguationData":[TD([[makeQuery(id+"F0.imprint","IMPRINT",EDGE,{"disambiguationData":[TD([[subQ2,-1.0]])],"derivedFrom":subQ1}),1.0]])]});}
            var Q299;
            {var subQ0=sQuery(id+"F0.wireOp",EDGE,"E2.7.5.0");var subQ1=sQuery(id+"F0.wireOp",EDGE,"E2.7.4.0");var subQ2=makeQuery(id+"F0.imprint","INTERSECT",VERTEX,{"disambiguationData":[OD(0.0)],"derivedFrom":[subQ1,subQ0]});Q299=makeQuery(id+"F0.imprint","IMPRINT",FACE,{"disambiguationData":[TD([[makeQuery(id+"F0.imprint","IMPRINT",EDGE,{"disambiguationData":[TD([[subQ2,-1.0]])],"derivedFrom":subQ1}),-1.0]])]});}
            var Q300;
            {var subQ0=sQuery(id+"F0.wireOp",EDGE,"E2.6.3.0");var subQ1=sQuery(id+"F0.wireOp",EDGE,"E2.6.2.0");var subQ2=makeQuery(id+"F0.imprint","INTERSECT",VERTEX,{"disambiguationData":[OD(0.0)],"derivedFrom":[subQ1,subQ0]});Q300=makeQuery(id+"F0.imprint","IMPRINT",FACE,{"disambiguationData":[TD([[makeQuery(id+"F0.imprint","IMPRINT",EDGE,{"disambiguationData":[TD([[subQ2,-1.0]])],"derivedFrom":subQ1}),-1.0]])]});}
            var Q301;
            {var subQ0=sQuery(id+"F0.wireOp",EDGE,"E2.6.5.0");var subQ1=sQuery(id+"F0.wireOp",EDGE,"E2.6.4.0");var subQ2=makeQuery(id+"F0.imprint","INTERSECT",VERTEX,{"disambiguationData":[OD(0.0)],"derivedFrom":[subQ1,subQ0]});Q301=makeQuery(id+"F0.imprint","IMPRINT",FACE,{"disambiguationData":[TD([[makeQuery(id+"F0.imprint","IMPRINT",EDGE,{"disambiguationData":[TD([[subQ2,-1.0]])],"derivedFrom":subQ1}),-1.0]])]});}
            var Q302;
            {var subQ0=sQuery(id+"F0.wireOp",EDGE,"E2.5.3.0");var subQ1=sQuery(id+"F0.wireOp",EDGE,"E2.5.2.0");var subQ2=makeQuery(id+"F0.imprint","INTERSECT",VERTEX,{"disambiguationData":[OD(0.0)],"derivedFrom":[subQ1,subQ0]});Q302=makeQuery(id+"F0.imprint","IMPRINT",FACE,{"disambiguationData":[TD([[makeQuery(id+"F0.imprint","IMPRINT",EDGE,{"disambiguationData":[TD([[subQ2,-1.0]])],"derivedFrom":subQ1}),-1.0]])]});}
            var Q303;
            {var subQ0=sQuery(id+"F0.wireOp",EDGE,"E2.5.5.0");var subQ1=sQuery(id+"F0.wireOp",EDGE,"E2.5.4.0");var subQ2=makeQuery(id+"F0.imprint","INTERSECT",VERTEX,{"disambiguationData":[OD(0.0)],"derivedFrom":[subQ1,subQ0]});Q303=makeQuery(id+"F0.imprint","IMPRINT",FACE,{"disambiguationData":[TD([[makeQuery(id+"F0.imprint","IMPRINT",EDGE,{"disambiguationData":[TD([[subQ2,-1.0]])],"derivedFrom":subQ1}),-1.0]])]});}
            var Q304;
            {var subQ0=sQuery(id+"F0.wireOp",EDGE,"E2.3.3.0");var subQ1=sQuery(id+"F0.wireOp",EDGE,"E2.3.2.0");var subQ2=makeQuery(id+"F0.imprint","INTERSECT",VERTEX,{"disambiguationData":[OD(0.0)],"derivedFrom":[subQ1,subQ0]});Q304=makeQuery(id+"F0.imprint","IMPRINT",FACE,{"disambiguationData":[TD([[makeQuery(id+"F0.imprint","IMPRINT",EDGE,{"disambiguationData":[TD([[subQ2,-1.0]])],"derivedFrom":subQ1}),-1.0]])]});}
            var Q305;
            {var subQ0=sQuery(id+"F0.wireOp",EDGE,"E2.3.5.0");var subQ1=sQuery(id+"F0.wireOp",EDGE,"E2.3.4.0");var subQ2=makeQuery(id+"F0.imprint","INTERSECT",VERTEX,{"disambiguationData":[OD(0.0)],"derivedFrom":[subQ1,subQ0]});Q305=makeQuery(id+"F0.imprint","IMPRINT",FACE,{"disambiguationData":[TD([[makeQuery(id+"F0.imprint","IMPRINT",EDGE,{"disambiguationData":[TD([[subQ2,-1.0]])],"derivedFrom":subQ1}),-1.0]])]});}
            var Q306;
            {var subQ0=sQuery(id+"F0.wireOp",EDGE,"E2.2.5.0");var subQ1=sQuery(id+"F0.wireOp",EDGE,"E2.2.4.0");var subQ2=makeQuery(id+"F0.imprint","INTERSECT",VERTEX,{"disambiguationData":[OD(0.0)],"derivedFrom":[subQ1,subQ0]});Q306=makeQuery(id+"F0.imprint","IMPRINT",FACE,{"disambiguationData":[TD([[makeQuery(id+"F0.imprint","IMPRINT",EDGE,{"disambiguationData":[TD([[subQ2,-1.0]])],"derivedFrom":subQ1}),-1.0]])]});}
            var Q307;
            {var subQ0=sQuery(id+"F0.wireOp",EDGE,"E2.1.3.0");var subQ1=sQuery(id+"F0.wireOp",EDGE,"E2.1.2.0");var subQ2=makeQuery(id+"F0.imprint","INTERSECT",VERTEX,{"disambiguationData":[OD(0.0)],"derivedFrom":[subQ1,subQ0]});Q307=makeQuery(id+"F0.imprint","IMPRINT",FACE,{"disambiguationData":[TD([[makeQuery(id+"F0.imprint","IMPRINT",EDGE,{"disambiguationData":[TD([[subQ2,-1.0]])],"derivedFrom":subQ1}),-1.0]])]});}
            var Q308;
            {var subQ0=sQuery(id+"F0.wireOp",EDGE,"E2.1.5.0");var subQ1=sQuery(id+"F0.wireOp",EDGE,"E2.1.4.0");var subQ2=makeQuery(id+"F0.imprint","INTERSECT",VERTEX,{"disambiguationData":[OD(0.0)],"derivedFrom":[subQ1,subQ0]});Q308=makeQuery(id+"F0.imprint","IMPRINT",FACE,{"disambiguationData":[TD([[makeQuery(id+"F0.imprint","IMPRINT",EDGE,{"disambiguationData":[TD([[subQ2,-1.0]])],"derivedFrom":subQ1}),-1.0]])]});}
            var Q309;
            {var subQ0=sQuery(id+"F0.wireOp",EDGE,"E2.1.2.0");var subQ1=sQuery(id+"F0.wireOp",EDGE,"E2.0.2.0");var subQ2=makeQuery(id+"F0.imprint","INTERSECT",VERTEX,{"disambiguationData":[OD(0.0)],"derivedFrom":[subQ1,subQ0]});Q309=makeQuery(id+"F0.imprint","IMPRINT",FACE,{"disambiguationData":[TD([[makeQuery(id+"F0.imprint","IMPRINT",EDGE,{"disambiguationData":[TD([[subQ2,1.0]])],"derivedFrom":subQ1}),-1.0]])]});}
            var Q310;
            {var subQ0=sQuery(id+"F0.wireOp",EDGE,"E2.2.0.0");var subQ1=sQuery(id+"F0.wireOp",EDGE,"E2.1.0.0");var subQ2=makeQuery(id+"F0.imprint","INTERSECT",VERTEX,{"disambiguationData":[OD(0.0)],"derivedFrom":[subQ1,subQ0]});Q310=makeQuery(id+"F0.imprint","IMPRINT",FACE,{"disambiguationData":[TD([[makeQuery(id+"F0.imprint","IMPRINT",EDGE,{"disambiguationData":[TD([[subQ2,-1.0]])],"derivedFrom":subQ1}),-1.0]])]});}
            var Q311;
            {var subQ0=sQuery(id+"F0.wireOp",EDGE,"E2.9.3.0");var subQ1=sQuery(id+"F0.wireOp",EDGE,"E2.9.2.0");var subQ2=makeQuery(id+"F0.imprint","INTERSECT",VERTEX,{"disambiguationData":[OD(0.0)],"derivedFrom":[subQ1,subQ0]});Q311=makeQuery(id+"F0.imprint","IMPRINT",FACE,{"disambiguationData":[TD([[makeQuery(id+"F0.imprint","IMPRINT",EDGE,{"disambiguationData":[TD([[subQ2,-1.0]])],"derivedFrom":subQ1}),1.0]])]});}
            var Q312;
            {var subQ0=sQuery(id+"F0.wireOp",EDGE,"E2.9.5.0");var subQ1=sQuery(id+"F0.wireOp",EDGE,"E2.9.4.0");var subQ2=makeQuery(id+"F0.imprint","INTERSECT",VERTEX,{"disambiguationData":[OD(0.0)],"derivedFrom":[subQ1,subQ0]});Q312=makeQuery(id+"F0.imprint","IMPRINT",FACE,{"disambiguationData":[TD([[makeQuery(id+"F0.imprint","IMPRINT",EDGE,{"disambiguationData":[TD([[subQ2,-1.0]])],"derivedFrom":subQ1}),1.0]])]});}
            var Q313;
            {var subQ0=sQuery(id+"F0.wireOp",EDGE,"E2.11.0.0");var subQ1=sQuery(id+"F0.wireOp",EDGE,"E2.10.0.0");var subQ2=makeQuery(id+"F0.imprint","INTERSECT",VERTEX,{"disambiguationData":[OD(1.0)],"derivedFrom":[subQ1,subQ0]});Q313=makeQuery(id+"F0.imprint","IMPRINT",FACE,{"disambiguationData":[TD([[makeQuery(id+"F0.imprint","IMPRINT",EDGE,{"disambiguationData":[TD([[subQ2,-1.0]])],"derivedFrom":subQ1}),1.0]])]});}
            var Q314;
            {var subQ0=sQuery(id+"F0.wireOp",EDGE,"E2.10.3.0");var subQ1=sQuery(id+"F0.wireOp",EDGE,"E2.10.2.0");var subQ2=makeQuery(id+"F0.imprint","INTERSECT",VERTEX,{"disambiguationData":[OD(0.0)],"derivedFrom":[subQ1,subQ0]});Q314=makeQuery(id+"F0.imprint","IMPRINT",FACE,{"disambiguationData":[TD([[makeQuery(id+"F0.imprint","IMPRINT",EDGE,{"disambiguationData":[TD([[subQ2,-1.0]])],"derivedFrom":subQ1}),1.0]])]});}
            var Q315;
            {var subQ0=sQuery(id+"F0.wireOp",EDGE,"E2.9.0.0");var subQ1=sQuery(id+"F0.wireOp",EDGE,"E2.8.0.0");var subQ2=makeQuery(id+"F0.imprint","INTERSECT",VERTEX,{"disambiguationData":[OD(1.0)],"derivedFrom":[subQ1,subQ0]});Q315=makeQuery(id+"F0.imprint","IMPRINT",FACE,{"disambiguationData":[TD([[makeQuery(id+"F0.imprint","IMPRINT",EDGE,{"disambiguationData":[TD([[subQ2,-1.0]])],"derivedFrom":subQ1}),1.0]])]});}
            var Q316;
            {var subQ0=sQuery(id+"F0.wireOp",EDGE,"E2.8.3.0");var subQ1=sQuery(id+"F0.wireOp",EDGE,"E2.8.2.0");var subQ2=makeQuery(id+"F0.imprint","INTERSECT",VERTEX,{"disambiguationData":[OD(0.0)],"derivedFrom":[subQ1,subQ0]});Q316=makeQuery(id+"F0.imprint","IMPRINT",FACE,{"disambiguationData":[TD([[makeQuery(id+"F0.imprint","IMPRINT",EDGE,{"disambiguationData":[TD([[subQ2,-1.0]])],"derivedFrom":subQ1}),1.0]])]});}
            var Q317;
            {var subQ0=sQuery(id+"F0.wireOp",EDGE,"E2.8.5.0");var subQ1=sQuery(id+"F0.wireOp",EDGE,"E2.8.4.0");var subQ2=makeQuery(id+"F0.imprint","INTERSECT",VERTEX,{"disambiguationData":[OD(0.0)],"derivedFrom":[subQ1,subQ0]});Q317=makeQuery(id+"F0.imprint","IMPRINT",FACE,{"disambiguationData":[TD([[makeQuery(id+"F0.imprint","IMPRINT",EDGE,{"disambiguationData":[TD([[subQ2,-1.0]])],"derivedFrom":subQ1}),1.0]])]});}
            var Q318;
            {var subQ0=sQuery(id+"F0.wireOp",EDGE,"E2.10.0.0");var subQ1=sQuery(id+"F0.wireOp",EDGE,"E2.9.0.0");var subQ2=makeQuery(id+"F0.imprint","INTERSECT",VERTEX,{"disambiguationData":[OD(1.0)],"derivedFrom":[subQ1,subQ0]});Q318=makeQuery(id+"F0.imprint","IMPRINT",FACE,{"disambiguationData":[TD([[makeQuery(id+"F0.imprint","IMPRINT",EDGE,{"disambiguationData":[TD([[subQ2,-1.0]])],"derivedFrom":subQ1}),1.0]])]});}
            var Q319;
            {var subQ0=sQuery(id+"F0.wireOp",EDGE,"E2.7.3.0");var subQ1=sQuery(id+"F0.wireOp",EDGE,"E2.7.2.0");var subQ2=makeQuery(id+"F0.imprint","INTERSECT",VERTEX,{"disambiguationData":[OD(0.0)],"derivedFrom":[subQ1,subQ0]});Q319=makeQuery(id+"F0.imprint","IMPRINT",FACE,{"disambiguationData":[TD([[makeQuery(id+"F0.imprint","IMPRINT",EDGE,{"disambiguationData":[TD([[subQ2,-1.0]])],"derivedFrom":subQ1}),1.0]])]});}
            var Q320;
            {var subQ0=sQuery(id+"F0.wireOp",EDGE,"E2.7.5.0");var subQ1=sQuery(id+"F0.wireOp",EDGE,"E2.7.4.0");var subQ2=makeQuery(id+"F0.imprint","INTERSECT",VERTEX,{"disambiguationData":[OD(0.0)],"derivedFrom":[subQ1,subQ0]});Q320=makeQuery(id+"F0.imprint","IMPRINT",FACE,{"disambiguationData":[TD([[makeQuery(id+"F0.imprint","IMPRINT",EDGE,{"disambiguationData":[TD([[subQ2,-1.0]])],"derivedFrom":subQ1}),1.0]])]});}
            var Q321;
            {var subQ0=sQuery(id+"F0.wireOp",EDGE,"E2.6.3.0");var subQ1=sQuery(id+"F0.wireOp",EDGE,"E2.6.2.0");var subQ2=makeQuery(id+"F0.imprint","INTERSECT",VERTEX,{"disambiguationData":[OD(0.0)],"derivedFrom":[subQ1,subQ0]});Q321=makeQuery(id+"F0.imprint","IMPRINT",FACE,{"disambiguationData":[TD([[makeQuery(id+"F0.imprint","IMPRINT",EDGE,{"disambiguationData":[TD([[subQ2,-1.0]])],"derivedFrom":subQ1}),1.0]])]});}
            var Q322;
            {var subQ0=sQuery(id+"F0.wireOp",EDGE,"E2.6.5.0");var subQ1=sQuery(id+"F0.wireOp",EDGE,"E2.6.4.0");var subQ2=makeQuery(id+"F0.imprint","INTERSECT",VERTEX,{"disambiguationData":[OD(0.0)],"derivedFrom":[subQ1,subQ0]});Q322=makeQuery(id+"F0.imprint","IMPRINT",FACE,{"disambiguationData":[TD([[makeQuery(id+"F0.imprint","IMPRINT",EDGE,{"disambiguationData":[TD([[subQ2,-1.0]])],"derivedFrom":subQ1}),1.0]])]});}
            var Q323;
            {var subQ0=sQuery(id+"F0.wireOp",EDGE,"E2.8.0.0");var subQ1=sQuery(id+"F0.wireOp",EDGE,"E2.7.0.0");var subQ2=makeQuery(id+"F0.imprint","INTERSECT",VERTEX,{"disambiguationData":[OD(1.0)],"derivedFrom":[subQ1,subQ0]});Q323=makeQuery(id+"F0.imprint","IMPRINT",FACE,{"disambiguationData":[TD([[makeQuery(id+"F0.imprint","IMPRINT",EDGE,{"disambiguationData":[TD([[subQ2,-1.0]])],"derivedFrom":subQ1}),1.0]])]});}
            var Q324;
            {var subQ0=sQuery(id+"F0.wireOp",EDGE,"E2.4.5.0");var subQ1=sQuery(id+"F0.wireOp",EDGE,"E2.4.4.0");var subQ2=makeQuery(id+"F0.imprint","INTERSECT",VERTEX,{"disambiguationData":[OD(0.0)],"derivedFrom":[subQ1,subQ0]});Q324=makeQuery(id+"F0.imprint","IMPRINT",FACE,{"disambiguationData":[TD([[makeQuery(id+"F0.imprint","IMPRINT",EDGE,{"disambiguationData":[TD([[subQ2,-1.0]])],"derivedFrom":subQ1}),1.0]])]});}
            var Q325;
            {var subQ0=sQuery(id+"F0.wireOp",EDGE,"E2.6.0.0");var subQ1=sQuery(id+"F0.wireOp",EDGE,"E2.5.0.0");var subQ2=makeQuery(id+"F0.imprint","INTERSECT",VERTEX,{"disambiguationData":[OD(1.0)],"derivedFrom":[subQ1,subQ0]});Q325=makeQuery(id+"F0.imprint","IMPRINT",FACE,{"disambiguationData":[TD([[makeQuery(id+"F0.imprint","IMPRINT",EDGE,{"disambiguationData":[TD([[subQ2,-1.0]])],"derivedFrom":subQ1}),1.0]])]});}
            var Q326;
            {var subQ0=sQuery(id+"F0.wireOp",EDGE,"E2.5.3.0");var subQ1=sQuery(id+"F0.wireOp",EDGE,"E2.5.2.0");var subQ2=makeQuery(id+"F0.imprint","INTERSECT",VERTEX,{"disambiguationData":[OD(0.0)],"derivedFrom":[subQ1,subQ0]});Q326=makeQuery(id+"F0.imprint","IMPRINT",FACE,{"disambiguationData":[TD([[makeQuery(id+"F0.imprint","IMPRINT",EDGE,{"disambiguationData":[TD([[subQ2,-1.0]])],"derivedFrom":subQ1}),1.0]])]});}
            var Q327;
            {var subQ0=sQuery(id+"F0.wireOp",EDGE,"E2.5.5.0");var subQ1=sQuery(id+"F0.wireOp",EDGE,"E2.5.4.0");var subQ2=makeQuery(id+"F0.imprint","INTERSECT",VERTEX,{"disambiguationData":[OD(0.0)],"derivedFrom":[subQ1,subQ0]});Q327=makeQuery(id+"F0.imprint","IMPRINT",FACE,{"disambiguationData":[TD([[makeQuery(id+"F0.imprint","IMPRINT",EDGE,{"disambiguationData":[TD([[subQ2,-1.0]])],"derivedFrom":subQ1}),1.0]])]});}
            var Q328;
            {var subQ0=sQuery(id+"F0.wireOp",EDGE,"E2.3.3.0");var subQ1=sQuery(id+"F0.wireOp",EDGE,"E2.3.2.0");var subQ2=makeQuery(id+"F0.imprint","INTERSECT",VERTEX,{"disambiguationData":[OD(0.0)],"derivedFrom":[subQ1,subQ0]});Q328=makeQuery(id+"F0.imprint","IMPRINT",FACE,{"disambiguationData":[TD([[makeQuery(id+"F0.imprint","IMPRINT",EDGE,{"disambiguationData":[TD([[subQ2,-1.0]])],"derivedFrom":subQ1}),1.0]])]});}
            var Q329;
            {var subQ0=sQuery(id+"F0.wireOp",EDGE,"E2.3.5.0");var subQ1=sQuery(id+"F0.wireOp",EDGE,"E2.3.4.0");var subQ2=makeQuery(id+"F0.imprint","INTERSECT",VERTEX,{"disambiguationData":[OD(0.0)],"derivedFrom":[subQ1,subQ0]});Q329=makeQuery(id+"F0.imprint","IMPRINT",FACE,{"disambiguationData":[TD([[makeQuery(id+"F0.imprint","IMPRINT",EDGE,{"disambiguationData":[TD([[subQ2,-1.0]])],"derivedFrom":subQ1}),1.0]])]});}
            var Q330;
            {var subQ0=sQuery(id+"F0.wireOp",EDGE,"E2.5.0.0");var subQ1=sQuery(id+"F0.wireOp",EDGE,"E2.4.0.0");var subQ2=makeQuery(id+"F0.imprint","INTERSECT",VERTEX,{"disambiguationData":[OD(1.0)],"derivedFrom":[subQ1,subQ0]});Q330=makeQuery(id+"F0.imprint","IMPRINT",FACE,{"disambiguationData":[TD([[makeQuery(id+"F0.imprint","IMPRINT",EDGE,{"disambiguationData":[TD([[subQ2,-1.0]])],"derivedFrom":subQ1}),1.0]])]});}
            var Q331;
            {var subQ0=sQuery(id+"F0.wireOp",EDGE,"E2.4.3.0");var subQ1=sQuery(id+"F0.wireOp",EDGE,"E2.4.2.0");var subQ2=makeQuery(id+"F0.imprint","INTERSECT",VERTEX,{"disambiguationData":[OD(0.0)],"derivedFrom":[subQ1,subQ0]});Q331=makeQuery(id+"F0.imprint","IMPRINT",FACE,{"disambiguationData":[TD([[makeQuery(id+"F0.imprint","IMPRINT",EDGE,{"disambiguationData":[TD([[subQ2,-1.0]])],"derivedFrom":subQ1}),1.0]])]});}
            var Q332;
            {var subQ0=sQuery(id+"F0.wireOp",EDGE,"E2.2.3.0");var subQ1=sQuery(id+"F0.wireOp",EDGE,"E2.2.2.0");var subQ2=makeQuery(id+"F0.imprint","INTERSECT",VERTEX,{"disambiguationData":[OD(0.0)],"derivedFrom":[subQ1,subQ0]});Q332=makeQuery(id+"F0.imprint","IMPRINT",FACE,{"disambiguationData":[TD([[makeQuery(id+"F0.imprint","IMPRINT",EDGE,{"disambiguationData":[TD([[subQ2,-1.0]])],"derivedFrom":subQ1}),1.0]])]});}
            var Q333;
            {var subQ0=sQuery(id+"F0.wireOp",EDGE,"E2.4.0.0");var subQ1=sQuery(id+"F0.wireOp",EDGE,"E2.3.0.0");var subQ2=makeQuery(id+"F0.imprint","INTERSECT",VERTEX,{"disambiguationData":[OD(1.0)],"derivedFrom":[subQ1,subQ0]});Q333=makeQuery(id+"F0.imprint","IMPRINT",FACE,{"disambiguationData":[TD([[makeQuery(id+"F0.imprint","IMPRINT",EDGE,{"disambiguationData":[TD([[subQ2,-1.0]])],"derivedFrom":subQ1}),1.0]])]});}
            var Q334;
            {var subQ0=sQuery(id+"F0.wireOp",EDGE,"E2.10.5.0");var subQ1=sQuery(id+"F0.wireOp",EDGE,"E2.10.4.0");var subQ2=makeQuery(id+"F0.imprint","INTERSECT",VERTEX,{"disambiguationData":[OD(0.0)],"derivedFrom":[subQ1,subQ0]});Q334=makeQuery(id+"F0.imprint","IMPRINT",FACE,{"disambiguationData":[TD([[makeQuery(id+"F0.imprint","IMPRINT",EDGE,{"disambiguationData":[TD([[subQ2,-1.0]])],"derivedFrom":subQ1}),1.0]])]});}
            var Q335;
            {var subQ0=sQuery(id+"F0.wireOp",EDGE,"E2.11.3.0");var subQ1=sQuery(id+"F0.wireOp",EDGE,"E2.11.2.0");var subQ2=makeQuery(id+"F0.imprint","INTERSECT",VERTEX,{"disambiguationData":[OD(0.0)],"derivedFrom":[subQ1,subQ0]});Q335=makeQuery(id+"F0.imprint","IMPRINT",FACE,{"disambiguationData":[TD([[makeQuery(id+"F0.imprint","IMPRINT",EDGE,{"disambiguationData":[TD([[subQ2,-1.0]])],"derivedFrom":subQ1}),1.0]])]});}
            var Q336;
            {var subQ0=sQuery(id+"F0.wireOp",EDGE,"E2.1.4.0");var subQ1=sQuery(id+"F0.wireOp",EDGE,"E2.0.4.0");var subQ2=makeQuery(id+"F0.imprint","INTERSECT",VERTEX,{"disambiguationData":[OD(0.0)],"derivedFrom":[subQ1,subQ0]});Q336=makeQuery(id+"F0.imprint","IMPRINT",FACE,{"disambiguationData":[TD([[makeQuery(id+"F0.imprint","IMPRINT",EDGE,{"disambiguationData":[TD([[subQ2,-1.0]])],"derivedFrom":subQ1}),1.0]])]});}
            var Q337;
            {var subQ0=sQuery(id+"F0.wireOp",EDGE,"E2.2.0.0");var subQ1=sQuery(id+"F0.wireOp",EDGE,"E2.1.0.0");var subQ2=makeQuery(id+"F0.imprint","INTERSECT",VERTEX,{"disambiguationData":[OD(1.0)],"derivedFrom":[subQ1,subQ0]});Q337=makeQuery(id+"F0.imprint","IMPRINT",FACE,{"disambiguationData":[TD([[makeQuery(id+"F0.imprint","IMPRINT",EDGE,{"disambiguationData":[TD([[subQ2,-1.0]])],"derivedFrom":subQ1}),1.0]])]});}
            var Q338;
            {var subQ0=sQuery(id+"F0.wireOp",EDGE,"E2.1.3.0");var subQ1=sQuery(id+"F0.wireOp",EDGE,"E2.1.2.0");var subQ2=makeQuery(id+"F0.imprint","INTERSECT",VERTEX,{"disambiguationData":[OD(0.0)],"derivedFrom":[subQ1,subQ0]});Q338=makeQuery(id+"F0.imprint","IMPRINT",FACE,{"disambiguationData":[TD([[makeQuery(id+"F0.imprint","IMPRINT",EDGE,{"disambiguationData":[TD([[subQ2,-1.0]])],"derivedFrom":subQ1}),1.0]])]});}
            var Q339;
            {var subQ0=sQuery(id+"F0.wireOp",EDGE,"E2.1.5.0");var subQ1=sQuery(id+"F0.wireOp",EDGE,"E2.1.4.0");var subQ2=makeQuery(id+"F0.imprint","INTERSECT",VERTEX,{"disambiguationData":[OD(0.0)],"derivedFrom":[subQ1,subQ0]});Q339=makeQuery(id+"F0.imprint","IMPRINT",FACE,{"disambiguationData":[TD([[makeQuery(id+"F0.imprint","IMPRINT",EDGE,{"disambiguationData":[TD([[subQ2,-1.0]])],"derivedFrom":subQ1}),1.0]])]});}
            var Q340;
            {var subQ0=sQuery(id+"F0.wireOp",EDGE,"E2.7.0.0");var subQ1=sQuery(id+"F0.wireOp",EDGE,"E2.6.0.0");var subQ2=makeQuery(id+"F0.imprint","INTERSECT",VERTEX,{"disambiguationData":[OD(1.0)],"derivedFrom":[subQ1,subQ0]});Q340=makeQuery(id+"F0.imprint","IMPRINT",FACE,{"disambiguationData":[TD([[makeQuery(id+"F0.imprint","IMPRINT",EDGE,{"disambiguationData":[TD([[subQ2,1.0]])],"derivedFrom":subQ1}),-1.0]])]});}
            var Q341;
            {var subQ0=sQuery(id+"F0.wireOp",EDGE,"E2.8.0.0");var subQ1=sQuery(id+"F0.wireOp",EDGE,"E2.7.0.0");var subQ2=makeQuery(id+"F0.imprint","INTERSECT",VERTEX,{"disambiguationData":[OD(1.0)],"derivedFrom":[subQ1,subQ0]});Q341=makeQuery(id+"F0.imprint","IMPRINT",FACE,{"disambiguationData":[TD([[makeQuery(id+"F0.imprint","IMPRINT",EDGE,{"disambiguationData":[TD([[subQ2,1.0]])],"derivedFrom":subQ1}),-1.0]])]});}
            var Q342;
            {var subQ0=sQuery(id+"F0.wireOp",EDGE,"E2.6.0.0");var subQ1=sQuery(id+"F0.wireOp",EDGE,"E2.5.0.0");var subQ2=makeQuery(id+"F0.imprint","INTERSECT",VERTEX,{"disambiguationData":[OD(1.0)],"derivedFrom":[subQ1,subQ0]});Q342=makeQuery(id+"F0.imprint","IMPRINT",FACE,{"disambiguationData":[TD([[makeQuery(id+"F0.imprint","IMPRINT",EDGE,{"disambiguationData":[TD([[subQ2,1.0]])],"derivedFrom":subQ1}),-1.0]])]});}
            var Q343;
            {var subQ0=sQuery(id+"F0.wireOp",EDGE,"E2.3.0.0");var subQ1=sQuery(id+"F0.wireOp",EDGE,"E2.2.0.0");var subQ2=makeQuery(id+"F0.imprint","INTERSECT",VERTEX,{"disambiguationData":[OD(1.0)],"derivedFrom":[subQ1,subQ0]});Q343=makeQuery(id+"F0.imprint","IMPRINT",FACE,{"disambiguationData":[TD([[makeQuery(id+"F0.imprint","IMPRINT",EDGE,{"disambiguationData":[TD([[subQ2,1.0]])],"derivedFrom":subQ1}),-1.0]])]});}
            var Q344;
            {var subQ0=sQuery(id+"F0.wireOp",EDGE,"E2.4.0.0");var subQ1=sQuery(id+"F0.wireOp",EDGE,"E2.3.0.0");var subQ2=makeQuery(id+"F0.imprint","INTERSECT",VERTEX,{"disambiguationData":[OD(1.0)],"derivedFrom":[subQ1,subQ0]});Q344=makeQuery(id+"F0.imprint","IMPRINT",FACE,{"disambiguationData":[TD([[makeQuery(id+"F0.imprint","IMPRINT",EDGE,{"disambiguationData":[TD([[subQ2,1.0]])],"derivedFrom":subQ1}),-1.0]])]});}
            var Q345;
            {var subQ0=sQuery(id+"F0.wireOp",EDGE,"E2.1.4.0");var subQ1=sQuery(id+"F0.wireOp",EDGE,"E2.0.4.0");var subQ2=makeQuery(id+"F0.imprint","INTERSECT",VERTEX,{"disambiguationData":[OD(0.0)],"derivedFrom":[subQ1,subQ0]});Q345=makeQuery(id+"F0.imprint","IMPRINT",FACE,{"disambiguationData":[TD([[makeQuery(id+"F0.imprint","IMPRINT",EDGE,{"disambiguationData":[TD([[subQ2,1.0]])],"derivedFrom":subQ1}),-1.0]])]});}
            var Q346;
            {var subQ0=sQuery(id+"F0.wireOp",EDGE,"E2.2.0.0");var subQ1=sQuery(id+"F0.wireOp",EDGE,"E2.1.0.0");var subQ2=makeQuery(id+"F0.imprint","INTERSECT",VERTEX,{"disambiguationData":[OD(1.0)],"derivedFrom":[subQ1,subQ0]});Q346=makeQuery(id+"F0.imprint","IMPRINT",FACE,{"disambiguationData":[TD([[makeQuery(id+"F0.imprint","IMPRINT",EDGE,{"disambiguationData":[TD([[subQ2,1.0]])],"derivedFrom":subQ1}),-1.0]])]});}
            var Q347;
            {var subQ0=sQuery(id+"F0.wireOp",EDGE,"E2.11.2.0");var subQ1=sQuery(id+"F0.wireOp",EDGE,"E2.11.1.0");var subQ2=makeQuery(id+"F0.imprint","INTERSECT",VERTEX,{"disambiguationData":[OD(0.0)],"derivedFrom":[subQ1,subQ0]});Q347=makeQuery(id+"F0.imprint","IMPRINT",FACE,{"disambiguationData":[TD([[makeQuery(id+"F0.imprint","IMPRINT",EDGE,{"disambiguationData":[TD([[subQ2,-1.0]])],"derivedFrom":subQ1}),1.0]])]});}
            var Q348;
            {var subQ0=sQuery(id+"F0.wireOp",EDGE,"E2.11.0.0");var subQ1=sQuery(id+"F0.wireOp",EDGE,"E2.10.0.0");var subQ2=makeQuery(id+"F0.imprint","INTERSECT",VERTEX,{"disambiguationData":[OD(1.0)],"derivedFrom":[subQ1,subQ0]});Q348=makeQuery(id+"F0.imprint","IMPRINT",FACE,{"disambiguationData":[TD([[makeQuery(id+"F0.imprint","IMPRINT",EDGE,{"disambiguationData":[TD([[subQ2,1.0]])],"derivedFrom":subQ1}),-1.0]])]});}
            var Q349;
            {var subQ0=sQuery(id+"F0.wireOp",EDGE,"E2.9.6.0");var subQ1=sQuery(id+"F0.wireOp",EDGE,"E2.8.6.0");var subQ2=makeQuery(id+"F0.imprint","INTERSECT",VERTEX,{"disambiguationData":[OD(0.0)],"derivedFrom":[subQ1,subQ0]});Q349=makeQuery(id+"F0.imprint","IMPRINT",FACE,{"disambiguationData":[TD([[makeQuery(id+"F0.imprint","IMPRINT",EDGE,{"disambiguationData":[TD([[subQ2,1.0]])],"derivedFrom":subQ1}),-1.0]])]});}
            var Q350;
            {var subQ0=sQuery(id+"F0.wireOp",EDGE,"E2.1.1.1");var subQ1=sQuery(id+"F0.wireOp",EDGE,"E2.0.1.0");var subQ2=makeQuery(id+"F0.imprint","INTERSECT",VERTEX,{"derivedFrom":[subQ1,subQ0]});Q350=makeQuery(id+"F0.imprint","IMPRINT",FACE,{"disambiguationData":[TD([[makeQuery(id+"F0.imprint","IMPRINT",EDGE,{"disambiguationData":[TD([[subQ2,1.0]])],"derivedFrom":subQ1}),-1.0]])]});}
            var Q351;
            {var subQ0=sQuery(id+"F0.wireOp",EDGE,"E2.11.4.0");var subQ1=sQuery(id+"F0.wireOp",EDGE,"E2.10.4.0");var subQ2=makeQuery(id+"F0.imprint","INTERSECT",VERTEX,{"disambiguationData":[OD(0.0)],"derivedFrom":[subQ1,subQ0]});Q351=makeQuery(id+"F0.imprint","IMPRINT",FACE,{"disambiguationData":[TD([[makeQuery(id+"F0.imprint","IMPRINT",EDGE,{"disambiguationData":[TD([[subQ2,1.0]])],"derivedFrom":subQ1}),-1.0]])]});}
            var Q352;
            {var subQ0=sQuery(id+"F0.wireOp",EDGE,"E2.11.6.1");var subQ1=sQuery(id+"F0.wireOp",EDGE,"E2.10.6.0");var subQ2=makeQuery(id+"F0.imprint","INTERSECT",VERTEX,{"derivedFrom":[subQ1,subQ0]});Q352=makeQuery(id+"F0.imprint","IMPRINT",FACE,{"disambiguationData":[TD([[makeQuery(id+"F0.imprint","IMPRINT",EDGE,{"disambiguationData":[TD([[subQ2,1.0]])],"derivedFrom":subQ1}),-1.0]])]});}
            var Q353;
            {var subQ0=sQuery(id+"F0.wireOp",EDGE,"E2.10.2.0");var subQ1=sQuery(id+"F0.wireOp",EDGE,"E2.9.2.0");var subQ2=makeQuery(id+"F0.imprint","INTERSECT",VERTEX,{"disambiguationData":[OD(0.0)],"derivedFrom":[subQ1,subQ0]});Q353=makeQuery(id+"F0.imprint","IMPRINT",FACE,{"disambiguationData":[TD([[makeQuery(id+"F0.imprint","IMPRINT",EDGE,{"disambiguationData":[TD([[subQ2,1.0]])],"derivedFrom":subQ1}),-1.0]])]});}
            var Q354;
            {var subQ0=sQuery(id+"F0.wireOp",EDGE,"E2.10.4.0");var subQ1=sQuery(id+"F0.wireOp",EDGE,"E2.9.4.0");var subQ2=makeQuery(id+"F0.imprint","INTERSECT",VERTEX,{"disambiguationData":[OD(0.0)],"derivedFrom":[subQ1,subQ0]});Q354=makeQuery(id+"F0.imprint","IMPRINT",FACE,{"disambiguationData":[TD([[makeQuery(id+"F0.imprint","IMPRINT",EDGE,{"disambiguationData":[TD([[subQ2,1.0]])],"derivedFrom":subQ1}),-1.0]])]});}
            var Q355;
            {var subQ0=sQuery(id+"F0.wireOp",EDGE,"E2.10.6.1");var subQ1=sQuery(id+"F0.wireOp",EDGE,"E2.9.6.0");var subQ2=makeQuery(id+"F0.imprint","INTERSECT",VERTEX,{"derivedFrom":[subQ1,subQ0]});Q355=makeQuery(id+"F0.imprint","IMPRINT",FACE,{"disambiguationData":[TD([[makeQuery(id+"F0.imprint","IMPRINT",EDGE,{"disambiguationData":[TD([[subQ2,1.0]])],"derivedFrom":subQ1}),-1.0]])]});}
            var Q356;
            {var subQ0=sQuery(id+"F0.wireOp",EDGE,"E2.11.2.0");var subQ1=sQuery(id+"F0.wireOp",EDGE,"E2.10.2.0");var subQ2=makeQuery(id+"F0.imprint","INTERSECT",VERTEX,{"disambiguationData":[OD(0.0)],"derivedFrom":[subQ1,subQ0]});Q356=makeQuery(id+"F0.imprint","IMPRINT",FACE,{"disambiguationData":[TD([[makeQuery(id+"F0.imprint","IMPRINT",EDGE,{"disambiguationData":[TD([[subQ2,1.0]])],"derivedFrom":subQ1}),-1.0]])]});}
            var Q357;
            {var subQ0=sQuery(id+"F0.wireOp",EDGE,"E2.8.6.1");var subQ1=sQuery(id+"F0.wireOp",EDGE,"E2.7.6.0");var subQ2=makeQuery(id+"F0.imprint","INTERSECT",VERTEX,{"derivedFrom":[subQ1,subQ0]});Q357=makeQuery(id+"F0.imprint","IMPRINT",FACE,{"disambiguationData":[TD([[makeQuery(id+"F0.imprint","IMPRINT",EDGE,{"disambiguationData":[TD([[subQ2,1.0]])],"derivedFrom":subQ1}),-1.0]])]});}
            var Q358;
            {var subQ0=sQuery(id+"F0.wireOp",EDGE,"E2.9.2.0");var subQ1=sQuery(id+"F0.wireOp",EDGE,"E2.8.2.0");var subQ2=makeQuery(id+"F0.imprint","INTERSECT",VERTEX,{"disambiguationData":[OD(0.0)],"derivedFrom":[subQ1,subQ0]});Q358=makeQuery(id+"F0.imprint","IMPRINT",FACE,{"disambiguationData":[TD([[makeQuery(id+"F0.imprint","IMPRINT",EDGE,{"disambiguationData":[TD([[subQ2,1.0]])],"derivedFrom":subQ1}),-1.0]])]});}
            var Q359;
            {var subQ0=sQuery(id+"F0.wireOp",EDGE,"E2.9.4.0");var subQ1=sQuery(id+"F0.wireOp",EDGE,"E2.8.4.0");var subQ2=makeQuery(id+"F0.imprint","INTERSECT",VERTEX,{"disambiguationData":[OD(0.0)],"derivedFrom":[subQ1,subQ0]});Q359=makeQuery(id+"F0.imprint","IMPRINT",FACE,{"disambiguationData":[TD([[makeQuery(id+"F0.imprint","IMPRINT",EDGE,{"disambiguationData":[TD([[subQ2,1.0]])],"derivedFrom":subQ1}),-1.0]])]});}
            var Q360;
            {var subQ0=sQuery(id+"F0.wireOp",EDGE,"E2.9.6.1");var subQ1=sQuery(id+"F0.wireOp",EDGE,"E2.8.6.0");var subQ2=makeQuery(id+"F0.imprint","INTERSECT",VERTEX,{"derivedFrom":[subQ1,subQ0]});Q360=makeQuery(id+"F0.imprint","IMPRINT",FACE,{"disambiguationData":[TD([[makeQuery(id+"F0.imprint","IMPRINT",EDGE,{"disambiguationData":[TD([[subQ2,1.0]])],"derivedFrom":subQ1}),-1.0]])]});}
            var Q361;
            {var subQ0=sQuery(id+"F0.wireOp",EDGE,"E2.8.4.0");var subQ1=sQuery(id+"F0.wireOp",EDGE,"E2.7.4.0");var subQ2=makeQuery(id+"F0.imprint","INTERSECT",VERTEX,{"disambiguationData":[OD(0.0)],"derivedFrom":[subQ1,subQ0]});Q361=makeQuery(id+"F0.imprint","IMPRINT",FACE,{"disambiguationData":[TD([[makeQuery(id+"F0.imprint","IMPRINT",EDGE,{"disambiguationData":[TD([[subQ2,1.0]])],"derivedFrom":subQ1}),-1.0]])]});}
            var Q362;
            {var subQ0=sQuery(id+"F0.wireOp",EDGE,"E2.8.2.0");var subQ1=sQuery(id+"F0.wireOp",EDGE,"E2.7.2.0");var subQ2=makeQuery(id+"F0.imprint","INTERSECT",VERTEX,{"disambiguationData":[OD(0.0)],"derivedFrom":[subQ1,subQ0]});Q362=makeQuery(id+"F0.imprint","IMPRINT",FACE,{"disambiguationData":[TD([[makeQuery(id+"F0.imprint","IMPRINT",EDGE,{"disambiguationData":[TD([[subQ2,1.0]])],"derivedFrom":subQ1}),-1.0]])]});}
            var Q363;
            {var subQ0=sQuery(id+"F0.wireOp",EDGE,"E2.6.6.1");var subQ1=sQuery(id+"F0.wireOp",EDGE,"E2.5.6.0");var subQ2=makeQuery(id+"F0.imprint","INTERSECT",VERTEX,{"derivedFrom":[subQ1,subQ0]});Q363=makeQuery(id+"F0.imprint","IMPRINT",FACE,{"disambiguationData":[TD([[makeQuery(id+"F0.imprint","IMPRINT",EDGE,{"disambiguationData":[TD([[subQ2,1.0]])],"derivedFrom":subQ1}),-1.0]])]});}
            var Q364;
            {var subQ0=sQuery(id+"F0.wireOp",EDGE,"E2.7.2.0");var subQ1=sQuery(id+"F0.wireOp",EDGE,"E2.6.2.0");var subQ2=makeQuery(id+"F0.imprint","INTERSECT",VERTEX,{"disambiguationData":[OD(0.0)],"derivedFrom":[subQ1,subQ0]});Q364=makeQuery(id+"F0.imprint","IMPRINT",FACE,{"disambiguationData":[TD([[makeQuery(id+"F0.imprint","IMPRINT",EDGE,{"disambiguationData":[TD([[subQ2,1.0]])],"derivedFrom":subQ1}),-1.0]])]});}
            var Q365;
            {var subQ0=sQuery(id+"F0.wireOp",EDGE,"E2.7.6.1");var subQ1=sQuery(id+"F0.wireOp",EDGE,"E2.6.6.0");var subQ2=makeQuery(id+"F0.imprint","INTERSECT",VERTEX,{"derivedFrom":[subQ1,subQ0]});Q365=makeQuery(id+"F0.imprint","IMPRINT",FACE,{"disambiguationData":[TD([[makeQuery(id+"F0.imprint","IMPRINT",EDGE,{"disambiguationData":[TD([[subQ2,1.0]])],"derivedFrom":subQ1}),-1.0]])]});}
            var Q366;
            {var subQ0=sQuery(id+"F0.wireOp",EDGE,"E2.5.4.0");var subQ1=sQuery(id+"F0.wireOp",EDGE,"E2.4.4.0");var subQ2=makeQuery(id+"F0.imprint","INTERSECT",VERTEX,{"disambiguationData":[OD(0.0)],"derivedFrom":[subQ1,subQ0]});Q366=makeQuery(id+"F0.imprint","IMPRINT",FACE,{"disambiguationData":[TD([[makeQuery(id+"F0.imprint","IMPRINT",EDGE,{"disambiguationData":[TD([[subQ2,1.0]])],"derivedFrom":subQ1}),-1.0]])]});}
            var Q367;
            {var subQ0=sQuery(id+"F0.wireOp",EDGE,"E2.5.6.1");var subQ1=sQuery(id+"F0.wireOp",EDGE,"E2.4.6.0");var subQ2=makeQuery(id+"F0.imprint","INTERSECT",VERTEX,{"derivedFrom":[subQ1,subQ0]});Q367=makeQuery(id+"F0.imprint","IMPRINT",FACE,{"disambiguationData":[TD([[makeQuery(id+"F0.imprint","IMPRINT",EDGE,{"disambiguationData":[TD([[subQ2,1.0]])],"derivedFrom":subQ1}),-1.0]])]});}
            var Q368;
            {var subQ0=sQuery(id+"F0.wireOp",EDGE,"E2.6.2.0");var subQ1=sQuery(id+"F0.wireOp",EDGE,"E2.5.2.0");var subQ2=makeQuery(id+"F0.imprint","INTERSECT",VERTEX,{"disambiguationData":[OD(0.0)],"derivedFrom":[subQ1,subQ0]});Q368=makeQuery(id+"F0.imprint","IMPRINT",FACE,{"disambiguationData":[TD([[makeQuery(id+"F0.imprint","IMPRINT",EDGE,{"disambiguationData":[TD([[subQ2,1.0]])],"derivedFrom":subQ1}),-1.0]])]});}
            var Q369;
            {var subQ0=sQuery(id+"F0.wireOp",EDGE,"E2.6.4.0");var subQ1=sQuery(id+"F0.wireOp",EDGE,"E2.5.4.0");var subQ2=makeQuery(id+"F0.imprint","INTERSECT",VERTEX,{"disambiguationData":[OD(0.0)],"derivedFrom":[subQ1,subQ0]});Q369=makeQuery(id+"F0.imprint","IMPRINT",FACE,{"disambiguationData":[TD([[makeQuery(id+"F0.imprint","IMPRINT",EDGE,{"disambiguationData":[TD([[subQ2,1.0]])],"derivedFrom":subQ1}),-1.0]])]});}
            var Q370;
            {var subQ0=sQuery(id+"F0.wireOp",EDGE,"E2.4.2.0");var subQ1=sQuery(id+"F0.wireOp",EDGE,"E2.3.2.0");var subQ2=makeQuery(id+"F0.imprint","INTERSECT",VERTEX,{"disambiguationData":[OD(0.0)],"derivedFrom":[subQ1,subQ0]});Q370=makeQuery(id+"F0.imprint","IMPRINT",FACE,{"disambiguationData":[TD([[makeQuery(id+"F0.imprint","IMPRINT",EDGE,{"disambiguationData":[TD([[subQ2,1.0]])],"derivedFrom":subQ1}),-1.0]])]});}
            var Q371;
            {var subQ0=sQuery(id+"F0.wireOp",EDGE,"E2.4.4.0");var subQ1=sQuery(id+"F0.wireOp",EDGE,"E2.3.4.0");var subQ2=makeQuery(id+"F0.imprint","INTERSECT",VERTEX,{"disambiguationData":[OD(0.0)],"derivedFrom":[subQ1,subQ0]});Q371=makeQuery(id+"F0.imprint","IMPRINT",FACE,{"disambiguationData":[TD([[makeQuery(id+"F0.imprint","IMPRINT",EDGE,{"disambiguationData":[TD([[subQ2,1.0]])],"derivedFrom":subQ1}),-1.0]])]});}
            var Q372;
            {var subQ0=sQuery(id+"F0.wireOp",EDGE,"E2.4.6.1");var subQ1=sQuery(id+"F0.wireOp",EDGE,"E2.3.6.0");var subQ2=makeQuery(id+"F0.imprint","INTERSECT",VERTEX,{"derivedFrom":[subQ1,subQ0]});Q372=makeQuery(id+"F0.imprint","IMPRINT",FACE,{"disambiguationData":[TD([[makeQuery(id+"F0.imprint","IMPRINT",EDGE,{"disambiguationData":[TD([[subQ2,1.0]])],"derivedFrom":subQ1}),-1.0]])]});}
            var Q373;
            {var subQ0=sQuery(id+"F0.wireOp",EDGE,"E2.5.2.0");var subQ1=sQuery(id+"F0.wireOp",EDGE,"E2.4.2.0");var subQ2=makeQuery(id+"F0.imprint","INTERSECT",VERTEX,{"disambiguationData":[OD(0.0)],"derivedFrom":[subQ1,subQ0]});Q373=makeQuery(id+"F0.imprint","IMPRINT",FACE,{"disambiguationData":[TD([[makeQuery(id+"F0.imprint","IMPRINT",EDGE,{"disambiguationData":[TD([[subQ2,1.0]])],"derivedFrom":subQ1}),-1.0]])]});}
            var Q374;
            {var subQ0=sQuery(id+"F0.wireOp",EDGE,"E2.2.6.1");var subQ1=sQuery(id+"F0.wireOp",EDGE,"E2.1.6.0");var subQ2=makeQuery(id+"F0.imprint","INTERSECT",VERTEX,{"derivedFrom":[subQ1,subQ0]});Q374=makeQuery(id+"F0.imprint","IMPRINT",FACE,{"disambiguationData":[TD([[makeQuery(id+"F0.imprint","IMPRINT",EDGE,{"disambiguationData":[TD([[subQ2,1.0]])],"derivedFrom":subQ1}),-1.0]])]});}
            var Q375;
            {var subQ0=sQuery(id+"F0.wireOp",EDGE,"E2.3.2.0");var subQ1=sQuery(id+"F0.wireOp",EDGE,"E2.2.2.0");var subQ2=makeQuery(id+"F0.imprint","INTERSECT",VERTEX,{"disambiguationData":[OD(0.0)],"derivedFrom":[subQ1,subQ0]});Q375=makeQuery(id+"F0.imprint","IMPRINT",FACE,{"disambiguationData":[TD([[makeQuery(id+"F0.imprint","IMPRINT",EDGE,{"disambiguationData":[TD([[subQ2,1.0]])],"derivedFrom":subQ1}),-1.0]])]});}
            var Q376;
            {var subQ0=sQuery(id+"F0.wireOp",EDGE,"E2.3.4.0");var subQ1=sQuery(id+"F0.wireOp",EDGE,"E2.2.4.0");var subQ2=makeQuery(id+"F0.imprint","INTERSECT",VERTEX,{"disambiguationData":[OD(0.0)],"derivedFrom":[subQ1,subQ0]});Q376=makeQuery(id+"F0.imprint","IMPRINT",FACE,{"disambiguationData":[TD([[makeQuery(id+"F0.imprint","IMPRINT",EDGE,{"disambiguationData":[TD([[subQ2,1.0]])],"derivedFrom":subQ1}),-1.0]])]});}
            var Q377;
            {var subQ0=sQuery(id+"F0.wireOp",EDGE,"E2.3.6.1");var subQ1=sQuery(id+"F0.wireOp",EDGE,"E2.2.6.0");var subQ2=makeQuery(id+"F0.imprint","INTERSECT",VERTEX,{"derivedFrom":[subQ1,subQ0]});Q377=makeQuery(id+"F0.imprint","IMPRINT",FACE,{"disambiguationData":[TD([[makeQuery(id+"F0.imprint","IMPRINT",EDGE,{"disambiguationData":[TD([[subQ2,1.0]])],"derivedFrom":subQ1}),-1.0]])]});}
            var Q378;
            {var subQ0=sQuery(id+"F0.wireOp",EDGE,"E2.1.3.1");var subQ1=sQuery(id+"F0.wireOp",EDGE,"E2.0.3.0");var subQ2=makeQuery(id+"F0.imprint","INTERSECT",VERTEX,{"derivedFrom":[subQ1,subQ0]});Q378=makeQuery(id+"F0.imprint","IMPRINT",FACE,{"disambiguationData":[TD([[makeQuery(id+"F0.imprint","IMPRINT",EDGE,{"disambiguationData":[TD([[subQ2,1.0]])],"derivedFrom":subQ1}),-1.0]])]});}
            var Q379;
            {var subQ0=sQuery(id+"F0.wireOp",EDGE,"E2.1.6.1");var subQ1=sQuery(id+"F0.wireOp",EDGE,"E2.0.6.0");var subQ2=makeQuery(id+"F0.imprint","INTERSECT",VERTEX,{"derivedFrom":[subQ1,subQ0]});Q379=makeQuery(id+"F0.imprint","IMPRINT",FACE,{"disambiguationData":[TD([[makeQuery(id+"F0.imprint","IMPRINT",EDGE,{"disambiguationData":[TD([[subQ2,1.0]])],"derivedFrom":subQ1}),-1.0]])]});}
            var Q380;
            {var subQ0=sQuery(id+"F0.wireOp",EDGE,"E2.2.2.0");var subQ1=sQuery(id+"F0.wireOp",EDGE,"E2.1.2.0");var subQ2=makeQuery(id+"F0.imprint","INTERSECT",VERTEX,{"disambiguationData":[OD(0.0)],"derivedFrom":[subQ1,subQ0]});Q380=makeQuery(id+"F0.imprint","IMPRINT",FACE,{"disambiguationData":[TD([[makeQuery(id+"F0.imprint","IMPRINT",EDGE,{"disambiguationData":[TD([[subQ2,1.0]])],"derivedFrom":subQ1}),-1.0]])]});}
            var Q381;
            {var subQ0=sQuery(id+"F0.wireOp",EDGE,"E2.2.4.0");var subQ1=sQuery(id+"F0.wireOp",EDGE,"E2.1.4.0");var subQ2=makeQuery(id+"F0.imprint","INTERSECT",VERTEX,{"disambiguationData":[OD(0.0)],"derivedFrom":[subQ1,subQ0]});Q381=makeQuery(id+"F0.imprint","IMPRINT",FACE,{"disambiguationData":[TD([[makeQuery(id+"F0.imprint","IMPRINT",EDGE,{"disambiguationData":[TD([[subQ2,1.0]])],"derivedFrom":subQ1}),-1.0]])]});}
            var Q382;
            {var subQ0=sQuery(id+"F0.wireOp",EDGE,"E2.9.0.0");var subQ1=sQuery(id+"F0.wireOp",EDGE,"E2.8.0.0");var subQ2=makeQuery(id+"F0.imprint","INTERSECT",VERTEX,{"disambiguationData":[OD(0.0)],"derivedFrom":[subQ1,subQ0]});Q382=makeQuery(id+"F0.imprint","IMPRINT",FACE,{"disambiguationData":[TD([[makeQuery(id+"F0.imprint","IMPRINT",EDGE,{"disambiguationData":[TD([[subQ2,-1.0]])],"derivedFrom":subQ1}),-1.0]])]});}
            var Q383;
            {var subQ0=sQuery(id+"F0.wireOp",EDGE,"E2.0.2.0");var subQ1=sQuery(id+"F0.wireOp",EDGE,"E2.0.1.0");var subQ2=makeQuery(id+"F0.imprint","INTERSECT",VERTEX,{"disambiguationData":[OD(1.0)],"derivedFrom":[subQ1,subQ0]});Q383=makeQuery(id+"F0.imprint","IMPRINT",FACE,{"disambiguationData":[TD([[makeQuery(id+"F0.imprint","IMPRINT",EDGE,{"disambiguationData":[TD([[subQ2,-1.0]])],"derivedFrom":subQ1}),1.0]])]});}
            var Q384;
            {var subQ0=sQuery(id+"F0.wireOp",EDGE,"E2.10.2.0");var subQ1=sQuery(id+"F0.wireOp",EDGE,"E2.9.2.0");var subQ2=makeQuery(id+"F0.imprint","INTERSECT",VERTEX,{"disambiguationData":[OD(0.0)],"derivedFrom":[subQ1,subQ0]});Q384=makeQuery(id+"F0.imprint","IMPRINT",FACE,{"disambiguationData":[TD([[makeQuery(id+"F0.imprint","IMPRINT",EDGE,{"disambiguationData":[TD([[subQ2,1.0]])],"derivedFrom":subQ1}),1.0]])]});}
            var Q385;
            {var subQ0=sQuery(id+"F0.wireOp",EDGE,"E2.10.4.0");var subQ1=sQuery(id+"F0.wireOp",EDGE,"E2.9.4.0");var subQ2=makeQuery(id+"F0.imprint","INTERSECT",VERTEX,{"disambiguationData":[OD(0.0)],"derivedFrom":[subQ1,subQ0]});Q385=makeQuery(id+"F0.imprint","IMPRINT",FACE,{"disambiguationData":[TD([[makeQuery(id+"F0.imprint","IMPRINT",EDGE,{"disambiguationData":[TD([[subQ2,1.0]])],"derivedFrom":subQ1}),1.0]])]});}
            var Q386;
            {var subQ0=sQuery(id+"F0.wireOp",EDGE,"E2.10.6.0");var subQ1=sQuery(id+"F0.wireOp",EDGE,"E2.9.6.0");var subQ2=makeQuery(id+"F0.imprint","INTERSECT",VERTEX,{"disambiguationData":[OD(0.0)],"derivedFrom":[subQ1,subQ0]});Q386=makeQuery(id+"F0.imprint","IMPRINT",FACE,{"disambiguationData":[TD([[makeQuery(id+"F0.imprint","IMPRINT",EDGE,{"disambiguationData":[TD([[subQ2,1.0]])],"derivedFrom":subQ1}),1.0]])]});}
            var Q387;
            {var subQ0=sQuery(id+"F0.wireOp",EDGE,"E2.8.6.0");var subQ1=sQuery(id+"F0.wireOp",EDGE,"E2.7.6.0");var subQ2=makeQuery(id+"F0.imprint","INTERSECT",VERTEX,{"disambiguationData":[OD(0.0)],"derivedFrom":[subQ1,subQ0]});Q387=makeQuery(id+"F0.imprint","IMPRINT",FACE,{"disambiguationData":[TD([[makeQuery(id+"F0.imprint","IMPRINT",EDGE,{"disambiguationData":[TD([[subQ2,1.0]])],"derivedFrom":subQ1}),1.0]])]});}
            var Q388;
            {var subQ0=sQuery(id+"F0.wireOp",EDGE,"E2.9.2.0");var subQ1=sQuery(id+"F0.wireOp",EDGE,"E2.8.2.0");var subQ2=makeQuery(id+"F0.imprint","INTERSECT",VERTEX,{"disambiguationData":[OD(0.0)],"derivedFrom":[subQ1,subQ0]});Q388=makeQuery(id+"F0.imprint","IMPRINT",FACE,{"disambiguationData":[TD([[makeQuery(id+"F0.imprint","IMPRINT",EDGE,{"disambiguationData":[TD([[subQ2,1.0]])],"derivedFrom":subQ1}),1.0]])]});}
            var Q389;
            {var subQ0=sQuery(id+"F0.wireOp",EDGE,"E2.9.4.0");var subQ1=sQuery(id+"F0.wireOp",EDGE,"E2.8.4.0");var subQ2=makeQuery(id+"F0.imprint","INTERSECT",VERTEX,{"disambiguationData":[OD(0.0)],"derivedFrom":[subQ1,subQ0]});Q389=makeQuery(id+"F0.imprint","IMPRINT",FACE,{"disambiguationData":[TD([[makeQuery(id+"F0.imprint","IMPRINT",EDGE,{"disambiguationData":[TD([[subQ2,1.0]])],"derivedFrom":subQ1}),1.0]])]});}
            var Q390;
            {var subQ0=sQuery(id+"F0.wireOp",EDGE,"E2.9.6.0");var subQ1=sQuery(id+"F0.wireOp",EDGE,"E2.8.6.0");var subQ2=makeQuery(id+"F0.imprint","INTERSECT",VERTEX,{"disambiguationData":[OD(0.0)],"derivedFrom":[subQ1,subQ0]});Q390=makeQuery(id+"F0.imprint","IMPRINT",FACE,{"disambiguationData":[TD([[makeQuery(id+"F0.imprint","IMPRINT",EDGE,{"disambiguationData":[TD([[subQ2,1.0]])],"derivedFrom":subQ1}),1.0]])]});}
            var Q391;
            {var subQ0=sQuery(id+"F0.wireOp",EDGE,"E2.8.4.0");var subQ1=sQuery(id+"F0.wireOp",EDGE,"E2.7.4.0");var subQ2=makeQuery(id+"F0.imprint","INTERSECT",VERTEX,{"disambiguationData":[OD(0.0)],"derivedFrom":[subQ1,subQ0]});Q391=makeQuery(id+"F0.imprint","IMPRINT",FACE,{"disambiguationData":[TD([[makeQuery(id+"F0.imprint","IMPRINT",EDGE,{"disambiguationData":[TD([[subQ2,1.0]])],"derivedFrom":subQ1}),1.0]])]});}
            var Q392;
            {var subQ0=sQuery(id+"F0.wireOp",EDGE,"E2.8.2.0");var subQ1=sQuery(id+"F0.wireOp",EDGE,"E2.7.2.0");var subQ2=makeQuery(id+"F0.imprint","INTERSECT",VERTEX,{"disambiguationData":[OD(0.0)],"derivedFrom":[subQ1,subQ0]});Q392=makeQuery(id+"F0.imprint","IMPRINT",FACE,{"disambiguationData":[TD([[makeQuery(id+"F0.imprint","IMPRINT",EDGE,{"disambiguationData":[TD([[subQ2,1.0]])],"derivedFrom":subQ1}),1.0]])]});}
            var Q393;
            {var subQ0=sQuery(id+"F0.wireOp",EDGE,"E2.7.2.0");var subQ1=sQuery(id+"F0.wireOp",EDGE,"E2.6.2.0");var subQ2=makeQuery(id+"F0.imprint","INTERSECT",VERTEX,{"disambiguationData":[OD(0.0)],"derivedFrom":[subQ1,subQ0]});Q393=makeQuery(id+"F0.imprint","IMPRINT",FACE,{"disambiguationData":[TD([[makeQuery(id+"F0.imprint","IMPRINT",EDGE,{"disambiguationData":[TD([[subQ2,1.0]])],"derivedFrom":subQ1}),1.0]])]});}
            var Q394;
            {var subQ0=sQuery(id+"F0.wireOp",EDGE,"E2.7.4.0");var subQ1=sQuery(id+"F0.wireOp",EDGE,"E2.6.4.0");var subQ2=makeQuery(id+"F0.imprint","INTERSECT",VERTEX,{"disambiguationData":[OD(0.0)],"derivedFrom":[subQ1,subQ0]});Q394=makeQuery(id+"F0.imprint","IMPRINT",FACE,{"disambiguationData":[TD([[makeQuery(id+"F0.imprint","IMPRINT",EDGE,{"disambiguationData":[TD([[subQ2,1.0]])],"derivedFrom":subQ1}),1.0]])]});}
            var Q395;
            {var subQ0=sQuery(id+"F0.wireOp",EDGE,"E2.7.6.0");var subQ1=sQuery(id+"F0.wireOp",EDGE,"E2.6.6.0");var subQ2=makeQuery(id+"F0.imprint","INTERSECT",VERTEX,{"disambiguationData":[OD(0.0)],"derivedFrom":[subQ1,subQ0]});Q395=makeQuery(id+"F0.imprint","IMPRINT",FACE,{"disambiguationData":[TD([[makeQuery(id+"F0.imprint","IMPRINT",EDGE,{"disambiguationData":[TD([[subQ2,1.0]])],"derivedFrom":subQ1}),1.0]])]});}
            var Q396;
            {var subQ0=sQuery(id+"F0.wireOp",EDGE,"E2.5.4.0");var subQ1=sQuery(id+"F0.wireOp",EDGE,"E2.4.4.0");var subQ2=makeQuery(id+"F0.imprint","INTERSECT",VERTEX,{"disambiguationData":[OD(0.0)],"derivedFrom":[subQ1,subQ0]});Q396=makeQuery(id+"F0.imprint","IMPRINT",FACE,{"disambiguationData":[TD([[makeQuery(id+"F0.imprint","IMPRINT",EDGE,{"disambiguationData":[TD([[subQ2,1.0]])],"derivedFrom":subQ1}),1.0]])]});}
            var Q397;
            {var subQ0=sQuery(id+"F0.wireOp",EDGE,"E2.5.6.0");var subQ1=sQuery(id+"F0.wireOp",EDGE,"E2.4.6.0");var subQ2=makeQuery(id+"F0.imprint","INTERSECT",VERTEX,{"disambiguationData":[OD(0.0)],"derivedFrom":[subQ1,subQ0]});Q397=makeQuery(id+"F0.imprint","IMPRINT",FACE,{"disambiguationData":[TD([[makeQuery(id+"F0.imprint","IMPRINT",EDGE,{"disambiguationData":[TD([[subQ2,1.0]])],"derivedFrom":subQ1}),1.0]])]});}
            var Q398;
            {var subQ0=sQuery(id+"F0.wireOp",EDGE,"E2.4.2.0");var subQ1=sQuery(id+"F0.wireOp",EDGE,"E2.3.2.0");var subQ2=makeQuery(id+"F0.imprint","INTERSECT",VERTEX,{"disambiguationData":[OD(0.0)],"derivedFrom":[subQ1,subQ0]});Q398=makeQuery(id+"F0.imprint","IMPRINT",FACE,{"disambiguationData":[TD([[makeQuery(id+"F0.imprint","IMPRINT",EDGE,{"disambiguationData":[TD([[subQ2,1.0]])],"derivedFrom":subQ1}),1.0]])]});}
            var Q399;
            {var subQ0=sQuery(id+"F0.wireOp",EDGE,"E2.4.4.0");var subQ1=sQuery(id+"F0.wireOp",EDGE,"E2.3.4.0");var subQ2=makeQuery(id+"F0.imprint","INTERSECT",VERTEX,{"disambiguationData":[OD(0.0)],"derivedFrom":[subQ1,subQ0]});Q399=makeQuery(id+"F0.imprint","IMPRINT",FACE,{"disambiguationData":[TD([[makeQuery(id+"F0.imprint","IMPRINT",EDGE,{"disambiguationData":[TD([[subQ2,1.0]])],"derivedFrom":subQ1}),1.0]])]});}
            var Q400;
            {var subQ0=sQuery(id+"F0.wireOp",EDGE,"E2.4.6.0");var subQ1=sQuery(id+"F0.wireOp",EDGE,"E2.3.6.0");var subQ2=makeQuery(id+"F0.imprint","INTERSECT",VERTEX,{"disambiguationData":[OD(0.0)],"derivedFrom":[subQ1,subQ0]});Q400=makeQuery(id+"F0.imprint","IMPRINT",FACE,{"disambiguationData":[TD([[makeQuery(id+"F0.imprint","IMPRINT",EDGE,{"disambiguationData":[TD([[subQ2,1.0]])],"derivedFrom":subQ1}),1.0]])]});}
            var Q401;
            {var subQ0=sQuery(id+"F0.wireOp",EDGE,"E2.5.2.0");var subQ1=sQuery(id+"F0.wireOp",EDGE,"E2.4.2.0");var subQ2=makeQuery(id+"F0.imprint","INTERSECT",VERTEX,{"disambiguationData":[OD(0.0)],"derivedFrom":[subQ1,subQ0]});Q401=makeQuery(id+"F0.imprint","IMPRINT",FACE,{"disambiguationData":[TD([[makeQuery(id+"F0.imprint","IMPRINT",EDGE,{"disambiguationData":[TD([[subQ2,1.0]])],"derivedFrom":subQ1}),1.0]])]});}
            var Q402;
            {var subQ0=sQuery(id+"F0.wireOp",EDGE,"E2.2.6.0");var subQ1=sQuery(id+"F0.wireOp",EDGE,"E2.1.6.0");var subQ2=makeQuery(id+"F0.imprint","INTERSECT",VERTEX,{"disambiguationData":[OD(0.0)],"derivedFrom":[subQ1,subQ0]});Q402=makeQuery(id+"F0.imprint","IMPRINT",FACE,{"disambiguationData":[TD([[makeQuery(id+"F0.imprint","IMPRINT",EDGE,{"disambiguationData":[TD([[subQ2,1.0]])],"derivedFrom":subQ1}),1.0]])]});}
            var Q403;
            {var subQ0=sQuery(id+"F0.wireOp",EDGE,"E2.3.2.0");var subQ1=sQuery(id+"F0.wireOp",EDGE,"E2.2.2.0");var subQ2=makeQuery(id+"F0.imprint","INTERSECT",VERTEX,{"disambiguationData":[OD(0.0)],"derivedFrom":[subQ1,subQ0]});Q403=makeQuery(id+"F0.imprint","IMPRINT",FACE,{"disambiguationData":[TD([[makeQuery(id+"F0.imprint","IMPRINT",EDGE,{"disambiguationData":[TD([[subQ2,1.0]])],"derivedFrom":subQ1}),1.0]])]});}
            var Q404;
            {var subQ0=sQuery(id+"F0.wireOp",EDGE,"E2.3.4.0");var subQ1=sQuery(id+"F0.wireOp",EDGE,"E2.2.4.0");var subQ2=makeQuery(id+"F0.imprint","INTERSECT",VERTEX,{"disambiguationData":[OD(0.0)],"derivedFrom":[subQ1,subQ0]});Q404=makeQuery(id+"F0.imprint","IMPRINT",FACE,{"disambiguationData":[TD([[makeQuery(id+"F0.imprint","IMPRINT",EDGE,{"disambiguationData":[TD([[subQ2,1.0]])],"derivedFrom":subQ1}),1.0]])]});}
            var Q405;
            {var subQ0=sQuery(id+"F0.wireOp",EDGE,"E2.3.6.0");var subQ1=sQuery(id+"F0.wireOp",EDGE,"E2.2.6.0");var subQ2=makeQuery(id+"F0.imprint","INTERSECT",VERTEX,{"disambiguationData":[OD(0.0)],"derivedFrom":[subQ1,subQ0]});Q405=makeQuery(id+"F0.imprint","IMPRINT",FACE,{"disambiguationData":[TD([[makeQuery(id+"F0.imprint","IMPRINT",EDGE,{"disambiguationData":[TD([[subQ2,1.0]])],"derivedFrom":subQ1}),1.0]])]});}
            var Q406;
            {var subQ0=sQuery(id+"F0.wireOp",EDGE,"E2.0.4.0");var subQ1=sQuery(id+"F0.wireOp",EDGE,"E2.0.3.0");var subQ2=makeQuery(id+"F0.imprint","INTERSECT",VERTEX,{"disambiguationData":[OD(1.0)],"derivedFrom":[subQ1,subQ0]});Q406=makeQuery(id+"F0.imprint","IMPRINT",FACE,{"disambiguationData":[TD([[makeQuery(id+"F0.imprint","IMPRINT",EDGE,{"disambiguationData":[TD([[subQ2,-1.0]])],"derivedFrom":subQ1}),-1.0]])]});}
            var Q407;
            {var subQ0=sQuery(id+"F0.wireOp",EDGE,"E2.2.2.0");var subQ1=sQuery(id+"F0.wireOp",EDGE,"E2.1.2.0");var subQ2=makeQuery(id+"F0.imprint","INTERSECT",VERTEX,{"disambiguationData":[OD(0.0)],"derivedFrom":[subQ1,subQ0]});Q407=makeQuery(id+"F0.imprint","IMPRINT",FACE,{"disambiguationData":[TD([[makeQuery(id+"F0.imprint","IMPRINT",EDGE,{"disambiguationData":[TD([[subQ2,1.0]])],"derivedFrom":subQ1}),1.0]])]});}
            var Q408;
            {var subQ0=sQuery(id+"F0.wireOp",EDGE,"E2.2.4.0");var subQ1=sQuery(id+"F0.wireOp",EDGE,"E2.1.4.0");var subQ2=makeQuery(id+"F0.imprint","INTERSECT",VERTEX,{"disambiguationData":[OD(0.0)],"derivedFrom":[subQ1,subQ0]});Q408=makeQuery(id+"F0.imprint","IMPRINT",FACE,{"disambiguationData":[TD([[makeQuery(id+"F0.imprint","IMPRINT",EDGE,{"disambiguationData":[TD([[subQ2,1.0]])],"derivedFrom":subQ1}),1.0]])]});}
            var Q409;
            {var subQ0=sQuery(id+"F0.wireOp",EDGE,"E2.11.3.0");var subQ1=sQuery(id+"F0.wireOp",EDGE,"E2.11.2.0");var subQ2=makeQuery(id+"F0.imprint","INTERSECT",VERTEX,{"disambiguationData":[OD(0.0)],"derivedFrom":[subQ1,subQ0]});Q409=makeQuery(id+"F0.imprint","IMPRINT",FACE,{"disambiguationData":[TD([[makeQuery(id+"F0.imprint","IMPRINT",EDGE,{"disambiguationData":[TD([[subQ2,-1.0]])],"derivedFrom":subQ1}),-1.0]])]});}
            var Q410;
            {var subQ0=sQuery(id+"F0.wireOp",EDGE,"E2.3.2.0");var subQ1=sQuery(id+"F0.wireOp",EDGE,"E2.2.2.0");var subQ2=makeQuery(id+"F0.imprint","INTERSECT",VERTEX,{"disambiguationData":[OD(0.0)],"derivedFrom":[subQ1,subQ0]});Q410=makeQuery(id+"F0.imprint","IMPRINT",FACE,{"disambiguationData":[TD([[makeQuery(id+"F0.imprint","IMPRINT",EDGE,{"disambiguationData":[TD([[subQ2,-1.0]])],"derivedFrom":subQ1}),1.0]])]});}
            var Q411;
            {var subQ0=sQuery(id+"F0.wireOp",EDGE,"E2.3.4.0");var subQ1=sQuery(id+"F0.wireOp",EDGE,"E2.2.4.0");var subQ2=makeQuery(id+"F0.imprint","INTERSECT",VERTEX,{"disambiguationData":[OD(0.0)],"derivedFrom":[subQ1,subQ0]});Q411=makeQuery(id+"F0.imprint","IMPRINT",FACE,{"disambiguationData":[TD([[makeQuery(id+"F0.imprint","IMPRINT",EDGE,{"disambiguationData":[TD([[subQ2,-1.0]])],"derivedFrom":subQ1}),1.0]])]});}
            var Q412;
            {var subQ0=sQuery(id+"F0.wireOp",EDGE,"E2.4.0.0");var subQ1=sQuery(id+"F0.wireOp",EDGE,"E2.3.0.0");var subQ2=makeQuery(id+"F0.imprint","INTERSECT",VERTEX,{"disambiguationData":[OD(1.0)],"derivedFrom":[subQ1,subQ0]});Q412=makeQuery(id+"F0.imprint","IMPRINT",FACE,{"disambiguationData":[TD([[makeQuery(id+"F0.imprint","IMPRINT",EDGE,{"disambiguationData":[TD([[subQ2,1.0]])],"derivedFrom":subQ1}),1.0]])]});}
            var Q413;
            {var subQ0=sQuery(id+"F0.wireOp",EDGE,"E2.4.2.0");var subQ1=sQuery(id+"F0.wireOp",EDGE,"E2.3.2.0");var subQ2=makeQuery(id+"F0.imprint","INTERSECT",VERTEX,{"disambiguationData":[OD(0.0)],"derivedFrom":[subQ1,subQ0]});Q413=makeQuery(id+"F0.imprint","IMPRINT",FACE,{"disambiguationData":[TD([[makeQuery(id+"F0.imprint","IMPRINT",EDGE,{"disambiguationData":[TD([[subQ2,-1.0]])],"derivedFrom":subQ1}),1.0]])]});}
            var Q414;
            {var subQ0=sQuery(id+"F0.wireOp",EDGE,"E2.2.0.0");var subQ1=sQuery(id+"F0.wireOp",EDGE,"E2.1.0.0");var subQ2=makeQuery(id+"F0.imprint","INTERSECT",VERTEX,{"disambiguationData":[OD(1.0)],"derivedFrom":[subQ1,subQ0]});Q414=makeQuery(id+"F0.imprint","IMPRINT",FACE,{"disambiguationData":[TD([[makeQuery(id+"F0.imprint","IMPRINT",EDGE,{"disambiguationData":[TD([[subQ2,1.0]])],"derivedFrom":subQ1}),1.0]])]});}
            var Q415;
            {var subQ0=sQuery(id+"F0.wireOp",EDGE,"E2.2.2.0");var subQ1=sQuery(id+"F0.wireOp",EDGE,"E2.1.2.0");var subQ2=makeQuery(id+"F0.imprint","INTERSECT",VERTEX,{"disambiguationData":[OD(0.0)],"derivedFrom":[subQ1,subQ0]});Q415=makeQuery(id+"F0.imprint","IMPRINT",FACE,{"disambiguationData":[TD([[makeQuery(id+"F0.imprint","IMPRINT",EDGE,{"disambiguationData":[TD([[subQ2,-1.0]])],"derivedFrom":subQ1}),1.0]])]});}
            var Q416;
            {var subQ0=sQuery(id+"F0.wireOp",EDGE,"E2.2.4.0");var subQ1=sQuery(id+"F0.wireOp",EDGE,"E2.1.4.0");var subQ2=makeQuery(id+"F0.imprint","INTERSECT",VERTEX,{"disambiguationData":[OD(0.0)],"derivedFrom":[subQ1,subQ0]});Q416=makeQuery(id+"F0.imprint","IMPRINT",FACE,{"disambiguationData":[TD([[makeQuery(id+"F0.imprint","IMPRINT",EDGE,{"disambiguationData":[TD([[subQ2,-1.0]])],"derivedFrom":subQ1}),1.0]])]});}
            var Q417;
            {var subQ0=sQuery(id+"F0.wireOp",EDGE,"E2.3.0.0");var subQ1=sQuery(id+"F0.wireOp",EDGE,"E2.2.0.0");var subQ2=makeQuery(id+"F0.imprint","INTERSECT",VERTEX,{"disambiguationData":[OD(1.0)],"derivedFrom":[subQ1,subQ0]});Q417=makeQuery(id+"F0.imprint","IMPRINT",FACE,{"disambiguationData":[TD([[makeQuery(id+"F0.imprint","IMPRINT",EDGE,{"disambiguationData":[TD([[subQ2,1.0]])],"derivedFrom":subQ1}),1.0]])]});}
            var Q418;
            {var subQ0=sQuery(id+"F0.wireOp",EDGE,"E2.11.4.0");var subQ1=sQuery(id+"F0.wireOp",EDGE,"E2.11.3.0");var subQ2=makeQuery(id+"F0.imprint","INTERSECT",VERTEX,{"disambiguationData":[OD(0.0)],"derivedFrom":[subQ1,subQ0]});Q418=makeQuery(id+"F0.imprint","IMPRINT",FACE,{"disambiguationData":[TD([[makeQuery(id+"F0.imprint","IMPRINT",EDGE,{"disambiguationData":[TD([[subQ2,-1.0]])],"derivedFrom":subQ1}),-1.0]])]});}
            var Q419;
            {var subQ0=sQuery(id+"F0.wireOp",EDGE,"E2.0.2.0");var subQ1=sQuery(id+"F0.wireOp",EDGE,"E2.0.1.0");var subQ2=makeQuery(id+"F0.imprint","INTERSECT",VERTEX,{"disambiguationData":[OD(1.0)],"derivedFrom":[subQ1,subQ0]});Q419=makeQuery(id+"F0.imprint","IMPRINT",FACE,{"disambiguationData":[TD([[makeQuery(id+"F0.imprint","IMPRINT",EDGE,{"disambiguationData":[TD([[subQ2,-1.0]])],"derivedFrom":subQ1}),-1.0]])]});}
            var Q420;
            {var subQ0=sQuery(id+"F0.wireOp",EDGE,"E2.11.1.0");var subQ1=sQuery(id+"F0.wireOp",EDGE,"E2.11.0.0");var subQ2=makeQuery(id+"F0.imprint","INTERSECT",VERTEX,{"disambiguationData":[OD(0.0)],"derivedFrom":[subQ1,subQ0]});Q420=makeQuery(id+"F0.imprint","IMPRINT",FACE,{"disambiguationData":[TD([[makeQuery(id+"F0.imprint","IMPRINT",EDGE,{"disambiguationData":[TD([[subQ2,-1.0]])],"derivedFrom":subQ1}),1.0]])]});}
            var Q421;
            {var subQ0=sQuery(id+"F0.wireOp",EDGE,"E2.11.2.0");var subQ1=sQuery(id+"F0.wireOp",EDGE,"E2.10.2.0");var subQ2=makeQuery(id+"F0.imprint","INTERSECT",VERTEX,{"disambiguationData":[OD(0.0)],"derivedFrom":[subQ1,subQ0]});Q421=makeQuery(id+"F0.imprint","IMPRINT",FACE,{"disambiguationData":[TD([[makeQuery(id+"F0.imprint","IMPRINT",EDGE,{"disambiguationData":[TD([[subQ2,-1.0]])],"derivedFrom":subQ1}),1.0]])]});}
            var Q422;
            {var subQ0=sQuery(id+"F0.wireOp",EDGE,"E2.11.4.0");var subQ1=sQuery(id+"F0.wireOp",EDGE,"E2.10.4.0");var subQ2=makeQuery(id+"F0.imprint","INTERSECT",VERTEX,{"disambiguationData":[OD(0.0)],"derivedFrom":[subQ1,subQ0]});Q422=makeQuery(id+"F0.imprint","IMPRINT",FACE,{"disambiguationData":[TD([[makeQuery(id+"F0.imprint","IMPRINT",EDGE,{"disambiguationData":[TD([[subQ2,-1.0]])],"derivedFrom":subQ1}),1.0]])]});}
            var Q423;
            {var subQ0=sQuery(id+"F0.wireOp",EDGE,"E2.9.2.0");var subQ1=sQuery(id+"F0.wireOp",EDGE,"E2.8.2.0");var subQ2=makeQuery(id+"F0.imprint","INTERSECT",VERTEX,{"disambiguationData":[OD(0.0)],"derivedFrom":[subQ1,subQ0]});Q423=makeQuery(id+"F0.imprint","IMPRINT",FACE,{"disambiguationData":[TD([[makeQuery(id+"F0.imprint","IMPRINT",EDGE,{"disambiguationData":[TD([[subQ2,-1.0]])],"derivedFrom":subQ1}),1.0]])]});}
            var Q424;
            {var subQ0=sQuery(id+"F0.wireOp",EDGE,"E2.9.4.0");var subQ1=sQuery(id+"F0.wireOp",EDGE,"E2.8.4.0");var subQ2=makeQuery(id+"F0.imprint","INTERSECT",VERTEX,{"disambiguationData":[OD(0.0)],"derivedFrom":[subQ1,subQ0]});Q424=makeQuery(id+"F0.imprint","IMPRINT",FACE,{"disambiguationData":[TD([[makeQuery(id+"F0.imprint","IMPRINT",EDGE,{"disambiguationData":[TD([[subQ2,-1.0]])],"derivedFrom":subQ1}),1.0]])]});}
            var Q425;
            {var subQ0=sQuery(id+"F0.wireOp",EDGE,"E2.10.0.0");var subQ1=sQuery(id+"F0.wireOp",EDGE,"E2.9.0.0");var subQ2=makeQuery(id+"F0.imprint","INTERSECT",VERTEX,{"disambiguationData":[OD(1.0)],"derivedFrom":[subQ1,subQ0]});Q425=makeQuery(id+"F0.imprint","IMPRINT",FACE,{"disambiguationData":[TD([[makeQuery(id+"F0.imprint","IMPRINT",EDGE,{"disambiguationData":[TD([[subQ2,1.0]])],"derivedFrom":subQ1}),1.0]])]});}
            var Q426;
            {var subQ0=sQuery(id+"F0.wireOp",EDGE,"E2.10.2.0");var subQ1=sQuery(id+"F0.wireOp",EDGE,"E2.9.2.0");var subQ2=makeQuery(id+"F0.imprint","INTERSECT",VERTEX,{"disambiguationData":[OD(0.0)],"derivedFrom":[subQ1,subQ0]});Q426=makeQuery(id+"F0.imprint","IMPRINT",FACE,{"disambiguationData":[TD([[makeQuery(id+"F0.imprint","IMPRINT",EDGE,{"disambiguationData":[TD([[subQ2,-1.0]])],"derivedFrom":subQ1}),1.0]])]});}
            var Q427;
            {var subQ0=sQuery(id+"F0.wireOp",EDGE,"E2.8.4.0");var subQ1=sQuery(id+"F0.wireOp",EDGE,"E2.7.4.0");var subQ2=makeQuery(id+"F0.imprint","INTERSECT",VERTEX,{"disambiguationData":[OD(0.0)],"derivedFrom":[subQ1,subQ0]});Q427=makeQuery(id+"F0.imprint","IMPRINT",FACE,{"disambiguationData":[TD([[makeQuery(id+"F0.imprint","IMPRINT",EDGE,{"disambiguationData":[TD([[subQ2,-1.0]])],"derivedFrom":subQ1}),1.0]])]});}
            var Q428;
            {var subQ0=sQuery(id+"F0.wireOp",EDGE,"E2.9.0.0");var subQ1=sQuery(id+"F0.wireOp",EDGE,"E2.8.0.0");var subQ2=makeQuery(id+"F0.imprint","INTERSECT",VERTEX,{"disambiguationData":[OD(1.0)],"derivedFrom":[subQ1,subQ0]});Q428=makeQuery(id+"F0.imprint","IMPRINT",FACE,{"disambiguationData":[TD([[makeQuery(id+"F0.imprint","IMPRINT",EDGE,{"disambiguationData":[TD([[subQ2,1.0]])],"derivedFrom":subQ1}),1.0]])]});}
            var Q429;
            {var subQ0=sQuery(id+"F0.wireOp",EDGE,"E2.7.2.0");var subQ1=sQuery(id+"F0.wireOp",EDGE,"E2.6.2.0");var subQ2=makeQuery(id+"F0.imprint","INTERSECT",VERTEX,{"disambiguationData":[OD(0.0)],"derivedFrom":[subQ1,subQ0]});Q429=makeQuery(id+"F0.imprint","IMPRINT",FACE,{"disambiguationData":[TD([[makeQuery(id+"F0.imprint","IMPRINT",EDGE,{"disambiguationData":[TD([[subQ2,-1.0]])],"derivedFrom":subQ1}),1.0]])]});}
            var Q430;
            {var subQ0=sQuery(id+"F0.wireOp",EDGE,"E2.7.4.0");var subQ1=sQuery(id+"F0.wireOp",EDGE,"E2.6.4.0");var subQ2=makeQuery(id+"F0.imprint","INTERSECT",VERTEX,{"disambiguationData":[OD(0.0)],"derivedFrom":[subQ1,subQ0]});Q430=makeQuery(id+"F0.imprint","IMPRINT",FACE,{"disambiguationData":[TD([[makeQuery(id+"F0.imprint","IMPRINT",EDGE,{"disambiguationData":[TD([[subQ2,-1.0]])],"derivedFrom":subQ1}),1.0]])]});}
            var Q431;
            {var subQ0=sQuery(id+"F0.wireOp",EDGE,"E2.8.0.0");var subQ1=sQuery(id+"F0.wireOp",EDGE,"E2.7.0.0");var subQ2=makeQuery(id+"F0.imprint","INTERSECT",VERTEX,{"disambiguationData":[OD(1.0)],"derivedFrom":[subQ1,subQ0]});Q431=makeQuery(id+"F0.imprint","IMPRINT",FACE,{"disambiguationData":[TD([[makeQuery(id+"F0.imprint","IMPRINT",EDGE,{"disambiguationData":[TD([[subQ2,1.0]])],"derivedFrom":subQ1}),1.0]])]});}
            var Q432;
            {var subQ0=sQuery(id+"F0.wireOp",EDGE,"E2.8.2.0");var subQ1=sQuery(id+"F0.wireOp",EDGE,"E2.7.2.0");var subQ2=makeQuery(id+"F0.imprint","INTERSECT",VERTEX,{"disambiguationData":[OD(0.0)],"derivedFrom":[subQ1,subQ0]});Q432=makeQuery(id+"F0.imprint","IMPRINT",FACE,{"disambiguationData":[TD([[makeQuery(id+"F0.imprint","IMPRINT",EDGE,{"disambiguationData":[TD([[subQ2,-1.0]])],"derivedFrom":subQ1}),1.0]])]});}
            var Q433;
            {var subQ0=sQuery(id+"F0.wireOp",EDGE,"E2.6.2.0");var subQ1=sQuery(id+"F0.wireOp",EDGE,"E2.5.2.0");var subQ2=makeQuery(id+"F0.imprint","INTERSECT",VERTEX,{"disambiguationData":[OD(0.0)],"derivedFrom":[subQ1,subQ0]});Q433=makeQuery(id+"F0.imprint","IMPRINT",FACE,{"disambiguationData":[TD([[makeQuery(id+"F0.imprint","IMPRINT",EDGE,{"disambiguationData":[TD([[subQ2,-1.0]])],"derivedFrom":subQ1}),1.0]])]});}
            var Q434;
            {var subQ0=sQuery(id+"F0.wireOp",EDGE,"E2.6.4.0");var subQ1=sQuery(id+"F0.wireOp",EDGE,"E2.5.4.0");var subQ2=makeQuery(id+"F0.imprint","INTERSECT",VERTEX,{"disambiguationData":[OD(0.0)],"derivedFrom":[subQ1,subQ0]});Q434=makeQuery(id+"F0.imprint","IMPRINT",FACE,{"disambiguationData":[TD([[makeQuery(id+"F0.imprint","IMPRINT",EDGE,{"disambiguationData":[TD([[subQ2,-1.0]])],"derivedFrom":subQ1}),1.0]])]});}
            var Q435;
            {var subQ0=sQuery(id+"F0.wireOp",EDGE,"E2.7.0.0");var subQ1=sQuery(id+"F0.wireOp",EDGE,"E2.6.0.0");var subQ2=makeQuery(id+"F0.imprint","INTERSECT",VERTEX,{"disambiguationData":[OD(1.0)],"derivedFrom":[subQ1,subQ0]});Q435=makeQuery(id+"F0.imprint","IMPRINT",FACE,{"disambiguationData":[TD([[makeQuery(id+"F0.imprint","IMPRINT",EDGE,{"disambiguationData":[TD([[subQ2,1.0]])],"derivedFrom":subQ1}),1.0]])]});}
            var Q436;
            {var subQ0=sQuery(id+"F0.wireOp",EDGE,"E2.4.4.0");var subQ1=sQuery(id+"F0.wireOp",EDGE,"E2.3.4.0");var subQ2=makeQuery(id+"F0.imprint","INTERSECT",VERTEX,{"disambiguationData":[OD(0.0)],"derivedFrom":[subQ1,subQ0]});Q436=makeQuery(id+"F0.imprint","IMPRINT",FACE,{"disambiguationData":[TD([[makeQuery(id+"F0.imprint","IMPRINT",EDGE,{"disambiguationData":[TD([[subQ2,-1.0]])],"derivedFrom":subQ1}),1.0]])]});}
            var Q437;
            {var subQ0=sQuery(id+"F0.wireOp",EDGE,"E2.5.0.0");var subQ1=sQuery(id+"F0.wireOp",EDGE,"E2.4.0.0");var subQ2=makeQuery(id+"F0.imprint","INTERSECT",VERTEX,{"disambiguationData":[OD(1.0)],"derivedFrom":[subQ1,subQ0]});Q437=makeQuery(id+"F0.imprint","IMPRINT",FACE,{"disambiguationData":[TD([[makeQuery(id+"F0.imprint","IMPRINT",EDGE,{"disambiguationData":[TD([[subQ2,1.0]])],"derivedFrom":subQ1}),1.0]])]});}
            var Q438;
            {var subQ0=sQuery(id+"F0.wireOp",EDGE,"E2.5.2.0");var subQ1=sQuery(id+"F0.wireOp",EDGE,"E2.4.2.0");var subQ2=makeQuery(id+"F0.imprint","INTERSECT",VERTEX,{"disambiguationData":[OD(0.0)],"derivedFrom":[subQ1,subQ0]});Q438=makeQuery(id+"F0.imprint","IMPRINT",FACE,{"disambiguationData":[TD([[makeQuery(id+"F0.imprint","IMPRINT",EDGE,{"disambiguationData":[TD([[subQ2,-1.0]])],"derivedFrom":subQ1}),1.0]])]});}
            var Q439;
            {var subQ0=sQuery(id+"F0.wireOp",EDGE,"E2.5.4.0");var subQ1=sQuery(id+"F0.wireOp",EDGE,"E2.4.4.0");var subQ2=makeQuery(id+"F0.imprint","INTERSECT",VERTEX,{"disambiguationData":[OD(0.0)],"derivedFrom":[subQ1,subQ0]});Q439=makeQuery(id+"F0.imprint","IMPRINT",FACE,{"disambiguationData":[TD([[makeQuery(id+"F0.imprint","IMPRINT",EDGE,{"disambiguationData":[TD([[subQ2,-1.0]])],"derivedFrom":subQ1}),1.0]])]});}
            var Q440;
            {var subQ0=sQuery(id+"F0.wireOp",EDGE,"E2.3.4.0");var subQ1=sQuery(id+"F0.wireOp",EDGE,"E2.3.3.0");var subQ2=makeQuery(id+"F0.imprint","INTERSECT",VERTEX,{"disambiguationData":[OD(0.0)],"derivedFrom":[subQ1,subQ0]});Q440=makeQuery(id+"F0.imprint","IMPRINT",FACE,{"disambiguationData":[TD([[makeQuery(id+"F0.imprint","IMPRINT",EDGE,{"disambiguationData":[TD([[subQ2,-1.0]])],"derivedFrom":subQ1}),1.0]])]});}
            var Q441;
            {var subQ0=sQuery(id+"F0.wireOp",EDGE,"E2.0.4.0");var subQ1=sQuery(id+"F0.wireOp",EDGE,"E2.0.3.0");var subQ2=makeQuery(id+"F0.imprint","INTERSECT",VERTEX,{"disambiguationData":[OD(1.0)],"derivedFrom":[subQ1,subQ0]});Q441=makeQuery(id+"F0.imprint","IMPRINT",FACE,{"disambiguationData":[TD([[makeQuery(id+"F0.imprint","IMPRINT",EDGE,{"disambiguationData":[TD([[subQ2,-1.0]])],"derivedFrom":subQ1}),1.0]])]});}
            var Q442;
            {var subQ0=sQuery(id+"F0.wireOp",EDGE,"E2.1.5.1");var subQ1=sQuery(id+"F0.wireOp",EDGE,"E2.0.5.0");var subQ2=makeQuery(id+"F0.imprint","INTERSECT",VERTEX,{"derivedFrom":[subQ1,subQ0]});Q442=makeQuery(id+"F0.imprint","IMPRINT",FACE,{"disambiguationData":[TD([[makeQuery(id+"F0.imprint","IMPRINT",EDGE,{"disambiguationData":[TD([[subQ2,1.0]])],"derivedFrom":subQ1}),-1.0]])]});}
            var Q443;
            {var subQ0=sQuery(id+"F0.wireOp",EDGE,"E2.8.6.0");var subQ1=sQuery(id+"F0.wireOp",EDGE,"E2.7.6.0");var subQ2=makeQuery(id+"F0.imprint","INTERSECT",VERTEX,{"disambiguationData":[OD(0.0)],"derivedFrom":[subQ1,subQ0]});Q443=makeQuery(id+"F0.imprint","IMPRINT",FACE,{"disambiguationData":[TD([[makeQuery(id+"F0.imprint","IMPRINT",EDGE,{"disambiguationData":[TD([[subQ2,1.0]])],"derivedFrom":subQ1}),-1.0]])]});}
            var Q444;
            {var subQ0=sQuery(id+"F0.wireOp",EDGE,"E2.6.3.1");var subQ1=sQuery(id+"F0.wireOp",EDGE,"E2.5.3.0");var subQ2=makeQuery(id+"F0.imprint","INTERSECT",VERTEX,{"derivedFrom":[subQ1,subQ0]});Q444=makeQuery(id+"F0.imprint","IMPRINT",FACE,{"disambiguationData":[TD([[makeQuery(id+"F0.imprint","IMPRINT",EDGE,{"disambiguationData":[TD([[subQ2,1.0]])],"derivedFrom":subQ1}),-1.0]])]});}
            var Q445;
            {var subQ0=sQuery(id+"F0.wireOp",EDGE,"E2.6.5.1");var subQ1=sQuery(id+"F0.wireOp",EDGE,"E2.5.5.0");var subQ2=makeQuery(id+"F0.imprint","INTERSECT",VERTEX,{"derivedFrom":[subQ1,subQ0]});Q445=makeQuery(id+"F0.imprint","IMPRINT",FACE,{"disambiguationData":[TD([[makeQuery(id+"F0.imprint","IMPRINT",EDGE,{"disambiguationData":[TD([[subQ2,1.0]])],"derivedFrom":subQ1}),-1.0]])]});}
            var Q446;
            {var subQ0=sQuery(id+"F0.wireOp",EDGE,"E2.7.1.1");var subQ1=sQuery(id+"F0.wireOp",EDGE,"E2.6.1.0");var subQ2=makeQuery(id+"F0.imprint","INTERSECT",VERTEX,{"derivedFrom":[subQ1,subQ0]});Q446=makeQuery(id+"F0.imprint","IMPRINT",FACE,{"disambiguationData":[TD([[makeQuery(id+"F0.imprint","IMPRINT",EDGE,{"disambiguationData":[TD([[subQ2,1.0]])],"derivedFrom":subQ1}),-1.0]])]});}
            var Q447;
            {var subQ0=sQuery(id+"F0.wireOp",EDGE,"E2.5.1.1");var subQ1=sQuery(id+"F0.wireOp",EDGE,"E2.4.1.0");var subQ2=makeQuery(id+"F0.imprint","INTERSECT",VERTEX,{"derivedFrom":[subQ1,subQ0]});Q447=makeQuery(id+"F0.imprint","IMPRINT",FACE,{"disambiguationData":[TD([[makeQuery(id+"F0.imprint","IMPRINT",EDGE,{"disambiguationData":[TD([[subQ2,1.0]])],"derivedFrom":subQ1}),-1.0]])]});}
            var Q448;
            {var subQ0=sQuery(id+"F0.wireOp",EDGE,"E2.5.3.1");var subQ1=sQuery(id+"F0.wireOp",EDGE,"E2.4.3.0");var subQ2=makeQuery(id+"F0.imprint","INTERSECT",VERTEX,{"derivedFrom":[subQ1,subQ0]});Q448=makeQuery(id+"F0.imprint","IMPRINT",FACE,{"disambiguationData":[TD([[makeQuery(id+"F0.imprint","IMPRINT",EDGE,{"disambiguationData":[TD([[subQ2,1.0]])],"derivedFrom":subQ1}),-1.0]])]});}
            var Q449;
            {var subQ0=sQuery(id+"F0.wireOp",EDGE,"E2.5.5.1");var subQ1=sQuery(id+"F0.wireOp",EDGE,"E2.4.5.0");var subQ2=makeQuery(id+"F0.imprint","INTERSECT",VERTEX,{"derivedFrom":[subQ1,subQ0]});Q449=makeQuery(id+"F0.imprint","IMPRINT",FACE,{"disambiguationData":[TD([[makeQuery(id+"F0.imprint","IMPRINT",EDGE,{"disambiguationData":[TD([[subQ2,1.0]])],"derivedFrom":subQ1}),-1.0]])]});}
            var Q450;
            {var subQ0=sQuery(id+"F0.wireOp",EDGE,"E2.4.1.1");var subQ1=sQuery(id+"F0.wireOp",EDGE,"E2.3.1.0");var subQ2=makeQuery(id+"F0.imprint","INTERSECT",VERTEX,{"derivedFrom":[subQ1,subQ0]});Q450=makeQuery(id+"F0.imprint","IMPRINT",FACE,{"disambiguationData":[TD([[makeQuery(id+"F0.imprint","IMPRINT",EDGE,{"disambiguationData":[TD([[subQ2,1.0]])],"derivedFrom":subQ1}),-1.0]])]});}
            var Q451;
            {var subQ0=sQuery(id+"F0.wireOp",EDGE,"E2.4.5.1");var subQ1=sQuery(id+"F0.wireOp",EDGE,"E2.3.5.0");var subQ2=makeQuery(id+"F0.imprint","INTERSECT",VERTEX,{"derivedFrom":[subQ1,subQ0]});Q451=makeQuery(id+"F0.imprint","IMPRINT",FACE,{"disambiguationData":[TD([[makeQuery(id+"F0.imprint","IMPRINT",EDGE,{"disambiguationData":[TD([[subQ2,1.0]])],"derivedFrom":subQ1}),-1.0]])]});}
            var Q452;
            {var subQ0=sQuery(id+"F0.wireOp",EDGE,"E2.2.3.1");var subQ1=sQuery(id+"F0.wireOp",EDGE,"E2.1.3.0");var subQ2=makeQuery(id+"F0.imprint","INTERSECT",VERTEX,{"derivedFrom":[subQ1,subQ0]});Q452=makeQuery(id+"F0.imprint","IMPRINT",FACE,{"disambiguationData":[TD([[makeQuery(id+"F0.imprint","IMPRINT",EDGE,{"disambiguationData":[TD([[subQ2,1.0]])],"derivedFrom":subQ1}),-1.0]])]});}
            var Q453;
            {var subQ0=sQuery(id+"F0.wireOp",EDGE,"E2.2.5.1");var subQ1=sQuery(id+"F0.wireOp",EDGE,"E2.1.5.0");var subQ2=makeQuery(id+"F0.imprint","INTERSECT",VERTEX,{"derivedFrom":[subQ1,subQ0]});Q453=makeQuery(id+"F0.imprint","IMPRINT",FACE,{"disambiguationData":[TD([[makeQuery(id+"F0.imprint","IMPRINT",EDGE,{"disambiguationData":[TD([[subQ2,1.0]])],"derivedFrom":subQ1}),-1.0]])]});}
            var Q454;
            {var subQ0=sQuery(id+"F0.wireOp",EDGE,"E2.3.1.1");var subQ1=sQuery(id+"F0.wireOp",EDGE,"E2.2.1.0");var subQ2=makeQuery(id+"F0.imprint","INTERSECT",VERTEX,{"derivedFrom":[subQ1,subQ0]});Q454=makeQuery(id+"F0.imprint","IMPRINT",FACE,{"disambiguationData":[TD([[makeQuery(id+"F0.imprint","IMPRINT",EDGE,{"disambiguationData":[TD([[subQ2,1.0]])],"derivedFrom":subQ1}),-1.0]])]});}
            var Q455;
            {var subQ0=sQuery(id+"F0.wireOp",EDGE,"E2.1.1.0");var subQ1=sQuery(id+"F0.wireOp",EDGE,"E2.0.1.0");var subQ2=makeQuery(id+"F0.imprint","INTERSECT",VERTEX,{"disambiguationData":[OD(0.0)],"derivedFrom":[subQ1,subQ0]});Q455=makeQuery(id+"F0.imprint","IMPRINT",FACE,{"disambiguationData":[TD([[makeQuery(id+"F0.imprint","IMPRINT",EDGE,{"disambiguationData":[TD([[subQ2,1.0]])],"derivedFrom":subQ1}),-1.0]])]});}
            var Q456;
            {var subQ0=sQuery(id+"F0.wireOp",EDGE,"E2.0.6.0");var subQ1=sQuery(id+"F0.wireOp",EDGE,"E2.0.5.0");var subQ2=makeQuery(id+"F0.imprint","INTERSECT",VERTEX,{"disambiguationData":[OD(1.0)],"derivedFrom":[subQ1,subQ0]});Q456=makeQuery(id+"F0.imprint","IMPRINT",FACE,{"disambiguationData":[TD([[makeQuery(id+"F0.imprint","IMPRINT",EDGE,{"disambiguationData":[TD([[subQ2,-1.0]])],"derivedFrom":subQ1}),-1.0]])]});}
            var Q457;
            {var subQ0=sQuery(id+"F0.wireOp",EDGE,"E2.2.1.1");var subQ1=sQuery(id+"F0.wireOp",EDGE,"E2.1.1.0");var subQ2=makeQuery(id+"F0.imprint","INTERSECT",VERTEX,{"derivedFrom":[subQ1,subQ0]});Q457=makeQuery(id+"F0.imprint","IMPRINT",FACE,{"disambiguationData":[TD([[makeQuery(id+"F0.imprint","IMPRINT",EDGE,{"disambiguationData":[TD([[subQ2,1.0]])],"derivedFrom":subQ1}),-1.0]])]});}
            var Q458;
            {var subQ0=sQuery(id+"F0.wireOp",EDGE,"E2.11.3.1");var subQ1=sQuery(id+"F0.wireOp",EDGE,"E2.10.3.0");var subQ2=makeQuery(id+"F0.imprint","INTERSECT",VERTEX,{"derivedFrom":[subQ1,subQ0]});Q458=makeQuery(id+"F0.imprint","IMPRINT",FACE,{"disambiguationData":[TD([[makeQuery(id+"F0.imprint","IMPRINT",EDGE,{"disambiguationData":[TD([[subQ2,1.0]])],"derivedFrom":subQ1}),-1.0]])]});}
            var Q459;
            {var subQ0=sQuery(id+"F0.wireOp",EDGE,"E2.11.5.1");var subQ1=sQuery(id+"F0.wireOp",EDGE,"E2.10.5.0");var subQ2=makeQuery(id+"F0.imprint","INTERSECT",VERTEX,{"derivedFrom":[subQ1,subQ0]});Q459=makeQuery(id+"F0.imprint","IMPRINT",FACE,{"disambiguationData":[TD([[makeQuery(id+"F0.imprint","IMPRINT",EDGE,{"disambiguationData":[TD([[subQ2,1.0]])],"derivedFrom":subQ1}),-1.0]])]});}
            var Q460;
            {var subQ0=sQuery(id+"F0.wireOp",EDGE,"E2.9.5.1");var subQ1=sQuery(id+"F0.wireOp",EDGE,"E2.8.5.0");var subQ2=makeQuery(id+"F0.imprint","INTERSECT",VERTEX,{"derivedFrom":[subQ1,subQ0]});Q460=makeQuery(id+"F0.imprint","IMPRINT",FACE,{"disambiguationData":[TD([[makeQuery(id+"F0.imprint","IMPRINT",EDGE,{"disambiguationData":[TD([[subQ2,1.0]])],"derivedFrom":subQ1}),-1.0]])]});}
            var Q461;
            {var subQ0=sQuery(id+"F0.wireOp",EDGE,"E2.10.1.1");var subQ1=sQuery(id+"F0.wireOp",EDGE,"E2.9.1.0");var subQ2=makeQuery(id+"F0.imprint","INTERSECT",VERTEX,{"derivedFrom":[subQ1,subQ0]});Q461=makeQuery(id+"F0.imprint","IMPRINT",FACE,{"disambiguationData":[TD([[makeQuery(id+"F0.imprint","IMPRINT",EDGE,{"disambiguationData":[TD([[subQ2,1.0]])],"derivedFrom":subQ1}),-1.0]])]});}
            var Q462;
            {var subQ0=sQuery(id+"F0.wireOp",EDGE,"E2.10.3.1");var subQ1=sQuery(id+"F0.wireOp",EDGE,"E2.9.3.0");var subQ2=makeQuery(id+"F0.imprint","INTERSECT",VERTEX,{"derivedFrom":[subQ1,subQ0]});Q462=makeQuery(id+"F0.imprint","IMPRINT",FACE,{"disambiguationData":[TD([[makeQuery(id+"F0.imprint","IMPRINT",EDGE,{"disambiguationData":[TD([[subQ2,1.0]])],"derivedFrom":subQ1}),-1.0]])]});}
            var Q463;
            {var subQ0=sQuery(id+"F0.wireOp",EDGE,"E2.10.5.1");var subQ1=sQuery(id+"F0.wireOp",EDGE,"E2.9.5.0");var subQ2=makeQuery(id+"F0.imprint","INTERSECT",VERTEX,{"derivedFrom":[subQ1,subQ0]});Q463=makeQuery(id+"F0.imprint","IMPRINT",FACE,{"disambiguationData":[TD([[makeQuery(id+"F0.imprint","IMPRINT",EDGE,{"disambiguationData":[TD([[subQ2,1.0]])],"derivedFrom":subQ1}),-1.0]])]});}
            var Q464;
            {var subQ0=sQuery(id+"F0.wireOp",EDGE,"E2.8.3.1");var subQ1=sQuery(id+"F0.wireOp",EDGE,"E2.7.3.0");var subQ2=makeQuery(id+"F0.imprint","INTERSECT",VERTEX,{"derivedFrom":[subQ1,subQ0]});Q464=makeQuery(id+"F0.imprint","IMPRINT",FACE,{"disambiguationData":[TD([[makeQuery(id+"F0.imprint","IMPRINT",EDGE,{"disambiguationData":[TD([[subQ2,1.0]])],"derivedFrom":subQ1}),-1.0]])]});}
            var Q465;
            {var subQ0=sQuery(id+"F0.wireOp",EDGE,"E2.9.1.1");var subQ1=sQuery(id+"F0.wireOp",EDGE,"E2.8.1.0");var subQ2=makeQuery(id+"F0.imprint","INTERSECT",VERTEX,{"derivedFrom":[subQ1,subQ0]});Q465=makeQuery(id+"F0.imprint","IMPRINT",FACE,{"disambiguationData":[TD([[makeQuery(id+"F0.imprint","IMPRINT",EDGE,{"disambiguationData":[TD([[subQ2,1.0]])],"derivedFrom":subQ1}),-1.0]])]});}
            var Q466;
            {var subQ0=sQuery(id+"F0.wireOp",EDGE,"E2.8.1.1");var subQ1=sQuery(id+"F0.wireOp",EDGE,"E2.7.1.0");var subQ2=makeQuery(id+"F0.imprint","INTERSECT",VERTEX,{"derivedFrom":[subQ1,subQ0]});Q466=makeQuery(id+"F0.imprint","IMPRINT",FACE,{"disambiguationData":[TD([[makeQuery(id+"F0.imprint","IMPRINT",EDGE,{"disambiguationData":[TD([[subQ2,1.0]])],"derivedFrom":subQ1}),-1.0]])]});}
            var Q467;
            {var subQ0=sQuery(id+"F0.wireOp",EDGE,"E2.4.2.0");var subQ1=sQuery(id+"F0.wireOp",EDGE,"E2.4.1.0");var subQ2=makeQuery(id+"F0.imprint","INTERSECT",VERTEX,{"disambiguationData":[OD(0.0)],"derivedFrom":[subQ1,subQ0]});Q467=makeQuery(id+"F0.imprint","IMPRINT",FACE,{"disambiguationData":[TD([[makeQuery(id+"F0.imprint","IMPRINT",EDGE,{"disambiguationData":[TD([[subQ2,-1.0]])],"derivedFrom":subQ1}),-1.0]])]});}
            var Q468;
            {var subQ0=sQuery(id+"F0.wireOp",EDGE,"E2.4.6.0");var subQ1=sQuery(id+"F0.wireOp",EDGE,"E2.4.5.0");var subQ2=makeQuery(id+"F0.imprint","INTERSECT",VERTEX,{"disambiguationData":[OD(0.0)],"derivedFrom":[subQ1,subQ0]});Q468=makeQuery(id+"F0.imprint","IMPRINT",FACE,{"disambiguationData":[TD([[makeQuery(id+"F0.imprint","IMPRINT",EDGE,{"disambiguationData":[TD([[subQ2,-1.0]])],"derivedFrom":subQ1}),-1.0]])]});}
            var Q469;
            {var subQ0=sQuery(id+"F0.wireOp",EDGE,"E2.5.2.0");var subQ1=sQuery(id+"F0.wireOp",EDGE,"E2.5.1.0");var subQ2=makeQuery(id+"F0.imprint","INTERSECT",VERTEX,{"disambiguationData":[OD(0.0)],"derivedFrom":[subQ1,subQ0]});Q469=makeQuery(id+"F0.imprint","IMPRINT",FACE,{"disambiguationData":[TD([[makeQuery(id+"F0.imprint","IMPRINT",EDGE,{"disambiguationData":[TD([[subQ2,-1.0]])],"derivedFrom":subQ1}),-1.0]])]});}
            var Q470;
            {var subQ0=sQuery(id+"F0.wireOp",EDGE,"E2.2.6.0");var subQ1=sQuery(id+"F0.wireOp",EDGE,"E2.2.5.0");var subQ2=makeQuery(id+"F0.imprint","INTERSECT",VERTEX,{"disambiguationData":[OD(0.0)],"derivedFrom":[subQ1,subQ0]});Q470=makeQuery(id+"F0.imprint","IMPRINT",FACE,{"disambiguationData":[TD([[makeQuery(id+"F0.imprint","IMPRINT",EDGE,{"disambiguationData":[TD([[subQ2,-1.0]])],"derivedFrom":subQ1}),-1.0]])]});}
            var Q471;
            {var subQ0=sQuery(id+"F0.wireOp",EDGE,"E2.3.2.0");var subQ1=sQuery(id+"F0.wireOp",EDGE,"E2.3.1.0");var subQ2=makeQuery(id+"F0.imprint","INTERSECT",VERTEX,{"disambiguationData":[OD(0.0)],"derivedFrom":[subQ1,subQ0]});Q471=makeQuery(id+"F0.imprint","IMPRINT",FACE,{"disambiguationData":[TD([[makeQuery(id+"F0.imprint","IMPRINT",EDGE,{"disambiguationData":[TD([[subQ2,-1.0]])],"derivedFrom":subQ1}),-1.0]])]});}
            var Q472;
            {var subQ0=sQuery(id+"F0.wireOp",EDGE,"E2.3.4.0");var subQ1=sQuery(id+"F0.wireOp",EDGE,"E2.3.3.0");var subQ2=makeQuery(id+"F0.imprint","INTERSECT",VERTEX,{"disambiguationData":[OD(0.0)],"derivedFrom":[subQ1,subQ0]});Q472=makeQuery(id+"F0.imprint","IMPRINT",FACE,{"disambiguationData":[TD([[makeQuery(id+"F0.imprint","IMPRINT",EDGE,{"disambiguationData":[TD([[subQ2,-1.0]])],"derivedFrom":subQ1}),-1.0]])]});}
            var Q473;
            {var subQ0=sQuery(id+"F0.wireOp",EDGE,"E2.3.6.0");var subQ1=sQuery(id+"F0.wireOp",EDGE,"E2.3.5.0");var subQ2=makeQuery(id+"F0.imprint","INTERSECT",VERTEX,{"disambiguationData":[OD(0.0)],"derivedFrom":[subQ1,subQ0]});Q473=makeQuery(id+"F0.imprint","IMPRINT",FACE,{"disambiguationData":[TD([[makeQuery(id+"F0.imprint","IMPRINT",EDGE,{"disambiguationData":[TD([[subQ2,-1.0]])],"derivedFrom":subQ1}),-1.0]])]});}
            var Q474;
            {var subQ0=sQuery(id+"F0.wireOp",EDGE,"E2.1.4.0");var subQ1=sQuery(id+"F0.wireOp",EDGE,"E2.1.3.0");var subQ2=makeQuery(id+"F0.imprint","INTERSECT",VERTEX,{"disambiguationData":[OD(0.0)],"derivedFrom":[subQ1,subQ0]});Q474=makeQuery(id+"F0.imprint","IMPRINT",FACE,{"disambiguationData":[TD([[makeQuery(id+"F0.imprint","IMPRINT",EDGE,{"disambiguationData":[TD([[subQ2,-1.0]])],"derivedFrom":subQ1}),-1.0]])]});}
            var Q475;
            {var subQ0=sQuery(id+"F0.wireOp",EDGE,"E2.1.6.0");var subQ1=sQuery(id+"F0.wireOp",EDGE,"E2.1.5.0");var subQ2=makeQuery(id+"F0.imprint","INTERSECT",VERTEX,{"disambiguationData":[OD(0.0)],"derivedFrom":[subQ1,subQ0]});Q475=makeQuery(id+"F0.imprint","IMPRINT",FACE,{"disambiguationData":[TD([[makeQuery(id+"F0.imprint","IMPRINT",EDGE,{"disambiguationData":[TD([[subQ2,-1.0]])],"derivedFrom":subQ1}),-1.0]])]});}
            var Q476;
            {var subQ0=sQuery(id+"F0.wireOp",EDGE,"E2.2.2.0");var subQ1=sQuery(id+"F0.wireOp",EDGE,"E2.2.1.0");var subQ2=makeQuery(id+"F0.imprint","INTERSECT",VERTEX,{"disambiguationData":[OD(0.0)],"derivedFrom":[subQ1,subQ0]});Q476=makeQuery(id+"F0.imprint","IMPRINT",FACE,{"disambiguationData":[TD([[makeQuery(id+"F0.imprint","IMPRINT",EDGE,{"disambiguationData":[TD([[subQ2,-1.0]])],"derivedFrom":subQ1}),-1.0]])]});}
            var Q477;
            {var subQ0=sQuery(id+"F0.wireOp",EDGE,"E2.2.4.0");var subQ1=sQuery(id+"F0.wireOp",EDGE,"E2.2.3.0");var subQ2=makeQuery(id+"F0.imprint","INTERSECT",VERTEX,{"disambiguationData":[OD(0.0)],"derivedFrom":[subQ1,subQ0]});Q477=makeQuery(id+"F0.imprint","IMPRINT",FACE,{"disambiguationData":[TD([[makeQuery(id+"F0.imprint","IMPRINT",EDGE,{"disambiguationData":[TD([[subQ2,-1.0]])],"derivedFrom":subQ1}),-1.0]])]});}
            var Q478;
            {var subQ0=sQuery(id+"F0.wireOp",EDGE,"E2.1.3.0");var subQ1=sQuery(id+"F0.wireOp",EDGE,"E2.0.3.0");var subQ2=makeQuery(id+"F0.imprint","INTERSECT",VERTEX,{"disambiguationData":[OD(0.0)],"derivedFrom":[subQ1,subQ0]});Q478=makeQuery(id+"F0.imprint","IMPRINT",FACE,{"disambiguationData":[TD([[makeQuery(id+"F0.imprint","IMPRINT",EDGE,{"disambiguationData":[TD([[subQ2,-1.0]])],"derivedFrom":subQ1}),1.0]])]});}
            var Q479;
            {var subQ0=sQuery(id+"F0.wireOp",EDGE,"E2.0.6.0");var subQ1=sQuery(id+"F0.wireOp",EDGE,"E2.0.5.0");var subQ2=makeQuery(id+"F0.imprint","INTERSECT",VERTEX,{"disambiguationData":[OD(1.0)],"derivedFrom":[subQ1,subQ0]});Q479=makeQuery(id+"F0.imprint","IMPRINT",FACE,{"disambiguationData":[TD([[makeQuery(id+"F0.imprint","IMPRINT",EDGE,{"disambiguationData":[TD([[subQ2,-1.0]])],"derivedFrom":subQ1}),1.0]])]});}
            var Q480;
            {var subQ0=sQuery(id+"F0.wireOp",EDGE,"E2.1.2.0");var subQ1=sQuery(id+"F0.wireOp",EDGE,"E2.1.1.0");var subQ2=makeQuery(id+"F0.imprint","INTERSECT",VERTEX,{"disambiguationData":[OD(0.0)],"derivedFrom":[subQ1,subQ0]});Q480=makeQuery(id+"F0.imprint","IMPRINT",FACE,{"disambiguationData":[TD([[makeQuery(id+"F0.imprint","IMPRINT",EDGE,{"disambiguationData":[TD([[subQ2,-1.0]])],"derivedFrom":subQ1}),-1.0]])]});}
            var Q481;
            {var subQ0=sQuery(id+"F0.wireOp",EDGE,"E2.4.0.0");var subQ1=sQuery(id+"F0.wireOp",EDGE,"E2.3.0.0");var subQ2=makeQuery(id+"F0.imprint","INTERSECT",VERTEX,{"disambiguationData":[OD(0.0)],"derivedFrom":[subQ1,subQ0]});Q481=makeQuery(id+"F0.imprint","IMPRINT",FACE,{"disambiguationData":[TD([[makeQuery(id+"F0.imprint","IMPRINT",EDGE,{"disambiguationData":[TD([[subQ2,-1.0]])],"derivedFrom":subQ1}),-1.0]])]});}
            var Q482;
            {var subQ0=sQuery(id+"F0.wireOp",EDGE,"E2.8.0.0");var subQ1=sQuery(id+"F0.wireOp",EDGE,"E2.7.0.0");var subQ2=makeQuery(id+"F0.imprint","INTERSECT",VERTEX,{"disambiguationData":[OD(0.0)],"derivedFrom":[subQ1,subQ0]});Q482=makeQuery(id+"F0.imprint","IMPRINT",FACE,{"disambiguationData":[TD([[makeQuery(id+"F0.imprint","IMPRINT",EDGE,{"disambiguationData":[TD([[subQ2,-1.0]])],"derivedFrom":subQ1}),-1.0]])]});}
            var Q483;
            {var subQ0=sQuery(id+"F0.wireOp",EDGE,"E2.10.2.0");var subQ1=sQuery(id+"F0.wireOp",EDGE,"E2.10.1.0");var subQ2=makeQuery(id+"F0.imprint","INTERSECT",VERTEX,{"disambiguationData":[OD(0.0)],"derivedFrom":[subQ1,subQ0]});Q483=makeQuery(id+"F0.imprint","IMPRINT",FACE,{"disambiguationData":[TD([[makeQuery(id+"F0.imprint","IMPRINT",EDGE,{"disambiguationData":[TD([[subQ2,-1.0]])],"derivedFrom":subQ1}),-1.0]])]});}
            var Q484;
            {var subQ0=sQuery(id+"F0.wireOp",EDGE,"E2.10.4.0");var subQ1=sQuery(id+"F0.wireOp",EDGE,"E2.10.3.0");var subQ2=makeQuery(id+"F0.imprint","INTERSECT",VERTEX,{"disambiguationData":[OD(0.0)],"derivedFrom":[subQ1,subQ0]});Q484=makeQuery(id+"F0.imprint","IMPRINT",FACE,{"disambiguationData":[TD([[makeQuery(id+"F0.imprint","IMPRINT",EDGE,{"disambiguationData":[TD([[subQ2,-1.0]])],"derivedFrom":subQ1}),-1.0]])]});}
            var Q485;
            {var subQ0=sQuery(id+"F0.wireOp",EDGE,"E2.10.6.0");var subQ1=sQuery(id+"F0.wireOp",EDGE,"E2.10.5.0");var subQ2=makeQuery(id+"F0.imprint","INTERSECT",VERTEX,{"disambiguationData":[OD(0.0)],"derivedFrom":[subQ1,subQ0]});Q485=makeQuery(id+"F0.imprint","IMPRINT",FACE,{"disambiguationData":[TD([[makeQuery(id+"F0.imprint","IMPRINT",EDGE,{"disambiguationData":[TD([[subQ2,-1.0]])],"derivedFrom":subQ1}),-1.0]])]});}
            var Q486;
            {var subQ0=sQuery(id+"F0.wireOp",EDGE,"E2.8.6.0");var subQ1=sQuery(id+"F0.wireOp",EDGE,"E2.8.5.0");var subQ2=makeQuery(id+"F0.imprint","INTERSECT",VERTEX,{"disambiguationData":[OD(0.0)],"derivedFrom":[subQ1,subQ0]});Q486=makeQuery(id+"F0.imprint","IMPRINT",FACE,{"disambiguationData":[TD([[makeQuery(id+"F0.imprint","IMPRINT",EDGE,{"disambiguationData":[TD([[subQ2,-1.0]])],"derivedFrom":subQ1}),-1.0]])]});}
            var Q487;
            {var subQ0=sQuery(id+"F0.wireOp",EDGE,"E2.9.2.0");var subQ1=sQuery(id+"F0.wireOp",EDGE,"E2.9.1.0");var subQ2=makeQuery(id+"F0.imprint","INTERSECT",VERTEX,{"disambiguationData":[OD(0.0)],"derivedFrom":[subQ1,subQ0]});Q487=makeQuery(id+"F0.imprint","IMPRINT",FACE,{"disambiguationData":[TD([[makeQuery(id+"F0.imprint","IMPRINT",EDGE,{"disambiguationData":[TD([[subQ2,-1.0]])],"derivedFrom":subQ1}),-1.0]])]});}
            var Q488;
            {var subQ0=sQuery(id+"F0.wireOp",EDGE,"E2.9.6.0");var subQ1=sQuery(id+"F0.wireOp",EDGE,"E2.9.5.0");var subQ2=makeQuery(id+"F0.imprint","INTERSECT",VERTEX,{"disambiguationData":[OD(0.0)],"derivedFrom":[subQ1,subQ0]});Q488=makeQuery(id+"F0.imprint","IMPRINT",FACE,{"disambiguationData":[TD([[makeQuery(id+"F0.imprint","IMPRINT",EDGE,{"disambiguationData":[TD([[subQ2,-1.0]])],"derivedFrom":subQ1}),-1.0]])]});}
            var Q489;
            {var subQ0=sQuery(id+"F0.wireOp",EDGE,"E2.7.4.0");var subQ1=sQuery(id+"F0.wireOp",EDGE,"E2.7.3.0");var subQ2=makeQuery(id+"F0.imprint","INTERSECT",VERTEX,{"disambiguationData":[OD(0.0)],"derivedFrom":[subQ1,subQ0]});Q489=makeQuery(id+"F0.imprint","IMPRINT",FACE,{"disambiguationData":[TD([[makeQuery(id+"F0.imprint","IMPRINT",EDGE,{"disambiguationData":[TD([[subQ2,-1.0]])],"derivedFrom":subQ1}),-1.0]])]});}
            var Q490;
            {var subQ0=sQuery(id+"F0.wireOp",EDGE,"E2.7.6.0");var subQ1=sQuery(id+"F0.wireOp",EDGE,"E2.7.5.0");var subQ2=makeQuery(id+"F0.imprint","INTERSECT",VERTEX,{"disambiguationData":[OD(0.0)],"derivedFrom":[subQ1,subQ0]});Q490=makeQuery(id+"F0.imprint","IMPRINT",FACE,{"disambiguationData":[TD([[makeQuery(id+"F0.imprint","IMPRINT",EDGE,{"disambiguationData":[TD([[subQ2,-1.0]])],"derivedFrom":subQ1}),-1.0]])]});}
            var Q491;
            {var subQ0=sQuery(id+"F0.wireOp",EDGE,"E2.8.2.0");var subQ1=sQuery(id+"F0.wireOp",EDGE,"E2.8.1.0");var subQ2=makeQuery(id+"F0.imprint","INTERSECT",VERTEX,{"disambiguationData":[OD(0.0)],"derivedFrom":[subQ1,subQ0]});Q491=makeQuery(id+"F0.imprint","IMPRINT",FACE,{"disambiguationData":[TD([[makeQuery(id+"F0.imprint","IMPRINT",EDGE,{"disambiguationData":[TD([[subQ2,-1.0]])],"derivedFrom":subQ1}),-1.0]])]});}
            var Q492;
            {var subQ0=sQuery(id+"F0.wireOp",EDGE,"E2.8.4.0");var subQ1=sQuery(id+"F0.wireOp",EDGE,"E2.8.3.0");var subQ2=makeQuery(id+"F0.imprint","INTERSECT",VERTEX,{"disambiguationData":[OD(0.0)],"derivedFrom":[subQ1,subQ0]});Q492=makeQuery(id+"F0.imprint","IMPRINT",FACE,{"disambiguationData":[TD([[makeQuery(id+"F0.imprint","IMPRINT",EDGE,{"disambiguationData":[TD([[subQ2,-1.0]])],"derivedFrom":subQ1}),-1.0]])]});}
            var Q493;
            {var subQ0=sQuery(id+"F0.wireOp",EDGE,"E2.6.4.0");var subQ1=sQuery(id+"F0.wireOp",EDGE,"E2.6.3.0");var subQ2=makeQuery(id+"F0.imprint","INTERSECT",VERTEX,{"disambiguationData":[OD(0.0)],"derivedFrom":[subQ1,subQ0]});Q493=makeQuery(id+"F0.imprint","IMPRINT",FACE,{"disambiguationData":[TD([[makeQuery(id+"F0.imprint","IMPRINT",EDGE,{"disambiguationData":[TD([[subQ2,-1.0]])],"derivedFrom":subQ1}),-1.0]])]});}
            var Q494;
            {var subQ0=sQuery(id+"F0.wireOp",EDGE,"E2.6.2.0");var subQ1=sQuery(id+"F0.wireOp",EDGE,"E2.6.1.0");var subQ2=makeQuery(id+"F0.imprint","INTERSECT",VERTEX,{"disambiguationData":[OD(0.0)],"derivedFrom":[subQ1,subQ0]});Q494=makeQuery(id+"F0.imprint","IMPRINT",FACE,{"disambiguationData":[TD([[makeQuery(id+"F0.imprint","IMPRINT",EDGE,{"disambiguationData":[TD([[subQ2,-1.0]])],"derivedFrom":subQ1}),-1.0]])]});}
            var Q495;
            {var subQ0=sQuery(id+"F0.wireOp",EDGE,"E2.5.6.0");var subQ1=sQuery(id+"F0.wireOp",EDGE,"E2.5.5.0");var subQ2=makeQuery(id+"F0.imprint","INTERSECT",VERTEX,{"disambiguationData":[OD(0.0)],"derivedFrom":[subQ1,subQ0]});Q495=makeQuery(id+"F0.imprint","IMPRINT",FACE,{"disambiguationData":[TD([[makeQuery(id+"F0.imprint","IMPRINT",EDGE,{"disambiguationData":[TD([[subQ2,-1.0]])],"derivedFrom":subQ1}),-1.0]])]});}
            var Q496;
            {var subQ0=sQuery(id+"F0.wireOp",EDGE,"E2.5.4.0");var subQ1=sQuery(id+"F0.wireOp",EDGE,"E2.5.3.0");var subQ2=makeQuery(id+"F0.imprint","INTERSECT",VERTEX,{"disambiguationData":[OD(0.0)],"derivedFrom":[subQ1,subQ0]});Q496=makeQuery(id+"F0.imprint","IMPRINT",FACE,{"disambiguationData":[TD([[makeQuery(id+"F0.imprint","IMPRINT",EDGE,{"disambiguationData":[TD([[subQ2,-1.0]])],"derivedFrom":subQ1}),-1.0]])]});}
            var Q497;
            {var subQ0=sQuery(id+"F0.wireOp",EDGE,"E2.7.2.0");var subQ1=sQuery(id+"F0.wireOp",EDGE,"E2.7.1.0");var subQ2=makeQuery(id+"F0.imprint","INTERSECT",VERTEX,{"disambiguationData":[OD(0.0)],"derivedFrom":[subQ1,subQ0]});Q497=makeQuery(id+"F0.imprint","IMPRINT",FACE,{"disambiguationData":[TD([[makeQuery(id+"F0.imprint","IMPRINT",EDGE,{"disambiguationData":[TD([[subQ2,-1.0]])],"derivedFrom":subQ1}),-1.0]])]});}
            var Q498;
            {var subQ0=sQuery(id+"F0.wireOp",EDGE,"E2.6.6.0");var subQ1=sQuery(id+"F0.wireOp",EDGE,"E2.6.5.0");var subQ2=makeQuery(id+"F0.imprint","INTERSECT",VERTEX,{"disambiguationData":[OD(0.0)],"derivedFrom":[subQ1,subQ0]});Q498=makeQuery(id+"F0.imprint","IMPRINT",FACE,{"disambiguationData":[TD([[makeQuery(id+"F0.imprint","IMPRINT",EDGE,{"disambiguationData":[TD([[subQ2,-1.0]])],"derivedFrom":subQ1}),-1.0]])]});}
            var Q499;
            {var subQ0=sQuery(id+"F0.wireOp",EDGE,"E2.10.6.0");var subQ1=sQuery(id+"F0.wireOp",EDGE,"E2.10.5.0");var subQ2=makeQuery(id+"F0.imprint","INTERSECT",VERTEX,{"disambiguationData":[OD(0.0)],"derivedFrom":[subQ1,subQ0]});Q499=makeQuery(id+"F0.imprint","IMPRINT",FACE,{"disambiguationData":[TD([[makeQuery(id+"F0.imprint","IMPRINT",EDGE,{"disambiguationData":[TD([[subQ2,-1.0]])],"derivedFrom":subQ1}),1.0]])]});}
            var Q500;
            {var subQ0=sQuery(id+"F0.wireOp",EDGE,"E2.2.2.0");var subQ1=sQuery(id+"F0.wireOp",EDGE,"E2.2.1.0");var subQ2=makeQuery(id+"F0.imprint","INTERSECT",VERTEX,{"disambiguationData":[OD(0.0)],"derivedFrom":[subQ1,subQ0]});Q500=makeQuery(id+"F0.imprint","IMPRINT",FACE,{"disambiguationData":[TD([[makeQuery(id+"F0.imprint","IMPRINT",EDGE,{"disambiguationData":[TD([[subQ2,-1.0]])],"derivedFrom":subQ1}),1.0]])]});}
            var Q501;
            {var subQ0=sQuery(id+"F0.wireOp",EDGE,"E2.1.2.0");var subQ1=sQuery(id+"F0.wireOp",EDGE,"E2.1.1.0");var subQ2=makeQuery(id+"F0.imprint","INTERSECT",VERTEX,{"disambiguationData":[OD(0.0)],"derivedFrom":[subQ1,subQ0]});Q501=makeQuery(id+"F0.imprint","IMPRINT",FACE,{"disambiguationData":[TD([[makeQuery(id+"F0.imprint","IMPRINT",EDGE,{"disambiguationData":[TD([[subQ2,-1.0]])],"derivedFrom":subQ1}),1.0]])]});}
            var Q502;
            {var subQ0=sQuery(id+"F0.wireOp",EDGE,"E2.9.2.0");var subQ1=sQuery(id+"F0.wireOp",EDGE,"E2.9.1.0");var subQ2=makeQuery(id+"F0.imprint","INTERSECT",VERTEX,{"disambiguationData":[OD(0.0)],"derivedFrom":[subQ1,subQ0]});Q502=makeQuery(id+"F0.imprint","IMPRINT",FACE,{"disambiguationData":[TD([[makeQuery(id+"F0.imprint","IMPRINT",EDGE,{"disambiguationData":[TD([[subQ2,-1.0]])],"derivedFrom":subQ1}),1.0]])]});}
            var Q503;
            {var subQ0=sQuery(id+"F0.wireOp",EDGE,"E2.8.2.0");var subQ1=sQuery(id+"F0.wireOp",EDGE,"E2.8.1.0");var subQ2=makeQuery(id+"F0.imprint","INTERSECT",VERTEX,{"disambiguationData":[OD(0.0)],"derivedFrom":[subQ1,subQ0]});Q503=makeQuery(id+"F0.imprint","IMPRINT",FACE,{"disambiguationData":[TD([[makeQuery(id+"F0.imprint","IMPRINT",EDGE,{"disambiguationData":[TD([[subQ2,-1.0]])],"derivedFrom":subQ1}),1.0]])]});}
            var Q504;
            {var subQ0=sQuery(id+"F0.wireOp",EDGE,"E2.6.6.0");var subQ1=sQuery(id+"F0.wireOp",EDGE,"E2.6.5.0");var subQ2=makeQuery(id+"F0.imprint","INTERSECT",VERTEX,{"disambiguationData":[OD(0.0)],"derivedFrom":[subQ1,subQ0]});Q504=makeQuery(id+"F0.imprint","IMPRINT",FACE,{"disambiguationData":[TD([[makeQuery(id+"F0.imprint","IMPRINT",EDGE,{"disambiguationData":[TD([[subQ2,-1.0]])],"derivedFrom":subQ1}),1.0]])]});}
            var Q505;
            {var subQ0=sQuery(id+"F0.wireOp",EDGE,"E2.7.2.0");var subQ1=sQuery(id+"F0.wireOp",EDGE,"E2.7.1.0");var subQ2=makeQuery(id+"F0.imprint","INTERSECT",VERTEX,{"disambiguationData":[OD(0.0)],"derivedFrom":[subQ1,subQ0]});Q505=makeQuery(id+"F0.imprint","IMPRINT",FACE,{"disambiguationData":[TD([[makeQuery(id+"F0.imprint","IMPRINT",EDGE,{"disambiguationData":[TD([[subQ2,-1.0]])],"derivedFrom":subQ1}),1.0]])]});}
            var Q506;
            {var subQ0=sQuery(id+"F0.wireOp",EDGE,"E2.4.2.0");var subQ1=sQuery(id+"F0.wireOp",EDGE,"E2.4.1.0");var subQ2=makeQuery(id+"F0.imprint","INTERSECT",VERTEX,{"disambiguationData":[OD(0.0)],"derivedFrom":[subQ1,subQ0]});Q506=makeQuery(id+"F0.imprint","IMPRINT",FACE,{"disambiguationData":[TD([[makeQuery(id+"F0.imprint","IMPRINT",EDGE,{"disambiguationData":[TD([[subQ2,-1.0]])],"derivedFrom":subQ1}),1.0]])]});}
            var Q507;
            {var subQ0=sQuery(id+"F0.wireOp",EDGE,"E2.2.5.0");var subQ1=sQuery(id+"F0.wireOp",EDGE,"E2.2.4.0");var subQ2=makeQuery(id+"F0.imprint","INTERSECT",VERTEX,{"disambiguationData":[OD(0.0)],"derivedFrom":[subQ1,subQ0]});Q507=makeQuery(id+"F0.imprint","IMPRINT",FACE,{"disambiguationData":[TD([[makeQuery(id+"F0.imprint","IMPRINT",EDGE,{"disambiguationData":[TD([[subQ2,-1.0]])],"derivedFrom":subQ1}),1.0]])]});}
            var Q508;
            {var subQ0=sQuery(id+"F0.wireOp",EDGE,"E2.3.2.0");var subQ1=sQuery(id+"F0.wireOp",EDGE,"E2.3.1.0");var subQ2=makeQuery(id+"F0.imprint","INTERSECT",VERTEX,{"disambiguationData":[OD(0.0)],"derivedFrom":[subQ1,subQ0]});Q508=makeQuery(id+"F0.imprint","IMPRINT",FACE,{"disambiguationData":[TD([[makeQuery(id+"F0.imprint","IMPRINT",EDGE,{"disambiguationData":[TD([[subQ2,-1.0]])],"derivedFrom":subQ1}),1.0]])]});}
            var Q509;
            {var subQ0=sQuery(id+"F0.wireOp",EDGE,"E2.3.6.0");var subQ1=sQuery(id+"F0.wireOp",EDGE,"E2.3.5.0");var subQ2=makeQuery(id+"F0.imprint","INTERSECT",VERTEX,{"disambiguationData":[OD(0.0)],"derivedFrom":[subQ1,subQ0]});Q509=makeQuery(id+"F0.imprint","IMPRINT",FACE,{"disambiguationData":[TD([[makeQuery(id+"F0.imprint","IMPRINT",EDGE,{"disambiguationData":[TD([[subQ2,-1.0]])],"derivedFrom":subQ1}),1.0]])]});}
            var Q510;
            {var subQ0=sQuery(id+"F0.wireOp",EDGE,"E2.1.6.0");var subQ1=sQuery(id+"F0.wireOp",EDGE,"E2.1.5.0");var subQ2=makeQuery(id+"F0.imprint","INTERSECT",VERTEX,{"disambiguationData":[OD(0.0)],"derivedFrom":[subQ1,subQ0]});Q510=makeQuery(id+"F0.imprint","IMPRINT",FACE,{"disambiguationData":[TD([[makeQuery(id+"F0.imprint","IMPRINT",EDGE,{"disambiguationData":[TD([[subQ2,-1.0]])],"derivedFrom":subQ1}),1.0]])]});}
            var Q511;
            {var subQ0=sQuery(id+"F0.wireOp",EDGE,"E2.11.1.0");var subQ1=sQuery(id+"F0.wireOp",EDGE,"E2.10.1.0");var subQ2=makeQuery(id+"F0.imprint","INTERSECT",VERTEX,{"disambiguationData":[OD(0.0)],"derivedFrom":[subQ1,subQ0]});Q511=makeQuery(id+"F0.imprint","IMPRINT",FACE,{"disambiguationData":[TD([[makeQuery(id+"F0.imprint","IMPRINT",EDGE,{"disambiguationData":[TD([[subQ2,-1.0]])],"derivedFrom":subQ1}),-1.0]])]});}
            var Q512;
            {var subQ0=sQuery(id+"F0.wireOp",EDGE,"E2.11.0.0");var subQ1=sQuery(id+"F0.wireOp",EDGE,"E2.10.0.0");var subQ2=makeQuery(id+"F0.imprint","INTERSECT",VERTEX,{"disambiguationData":[OD(1.0)],"derivedFrom":[subQ1,subQ0]});Q512=makeQuery(id+"F0.imprint","IMPRINT",FACE,{"disambiguationData":[TD([[makeQuery(id+"F0.imprint","IMPRINT",EDGE,{"disambiguationData":[TD([[subQ2,-1.0]])],"derivedFrom":subQ1}),-1.0]])]});}
            var Q513;
            {var subQ0=sQuery(id+"F0.wireOp",EDGE,"E4");Q513=makeQuery(id+"F0.imprint","IMPRINT",FACE,{"disambiguationData":[TD([[makeQuery(id+"F0.imprint","IMPRINT",EDGE,{"derivedFrom":subQ0}),1.0]])]});}
            extrude(context, id + "F1", {"entities" : qUnion([Q0, Q1, Q2, Q3, Q4, Q5, Q6, Q7, Q8, Q9, Q10, Q11, Q12, Q13, Q14, Q15, Q16, Q17, Q18, Q19, Q20, Q21, Q22, Q23, Q24, Q25, Q26, Q27, Q28, Q29, Q30, Q31, Q32, Q33, Q34, Q35, Q36, Q37, Q38, Q39, Q40, Q41, Q42, Q43, Q44, Q45, Q46, Q47, Q48, Q49, Q50, Q51, Q52, Q53, Q54, Q55, Q56, Q57, Q58, Q59, Q60, Q61, Q62, Q63, Q64, Q65, Q66, Q67, Q68, Q69, Q70, Q71, Q72, Q73, Q74, Q75, Q76, Q77, Q78, Q79, Q80, Q81, Q82, Q83, Q84, Q85, Q86, Q87, Q88, Q89, Q90, Q91, Q92, Q93, Q94, Q95, Q96, Q97, Q98, Q99, Q100, Q101, Q102, Q103, Q104, Q105, Q106, Q107, Q108, Q109, Q110, Q111, Q112, Q113, Q114, Q115, Q116, Q117, Q118, Q119, Q120, Q121, Q122, Q123, Q124, Q125, Q126, Q127, Q128, Q129, Q130, Q131, Q132, Q133, Q134, Q135, Q136, Q137, Q138, Q139, Q140, Q141, Q142, Q143, Q144, Q145, Q146, Q147, Q148, Q149, Q150, Q151, Q152, Q153, Q154, Q155, Q156, Q157, Q158, Q159, Q160, Q161, Q162, Q163, Q164, Q165, Q166, Q167, Q168, Q169, Q170, Q171, Q172, Q173, Q174, Q175, Q176, Q177, Q178, Q179, Q180, Q181, Q182, Q183, Q184, Q185, Q186, Q187, Q188, Q189, Q190, Q191, Q192, Q193, Q194, Q195, Q196, Q197, Q198, Q199, Q200, Q201, Q202, Q203, Q204, Q205, Q206, Q207, Q208, Q209, Q210, Q211, Q212, Q213, Q214, Q215, Q216, Q217, Q218, Q219, Q220, Q221, Q222, Q223, Q224, Q225, Q226, Q227, Q228, Q229, Q230, Q231, Q232, Q233, Q234, Q235, Q236, Q237, Q238, Q239, Q240, Q241, Q242, Q243, Q244, Q245, Q246, Q247, Q248, Q249, Q250, Q251, Q252, Q253, Q254, Q255, Q256, Q257, Q258, Q259, Q260, Q261, Q262, Q263, Q264, Q265, Q266, Q267, Q268, Q269, Q270, Q271, Q272, Q273, Q274, Q275, Q276, Q277, Q278, Q279, Q280, Q281, Q282, Q283, Q284, Q285, Q286, Q287, Q288, Q289, Q290, Q291, Q292, Q293, Q294, Q295, Q296, Q297, Q298, Q299, Q300, Q301, Q302, Q303, Q304, Q305, Q306, Q307, Q308, Q309, Q310, Q311, Q312, Q313, Q314, Q315, Q316, Q317, Q318, Q319, Q320, Q321, Q322, Q323, Q324, Q325, Q326, Q327, Q328, Q329, Q330, Q331, Q332, Q333, Q334, Q335, Q336, Q337, Q338, Q339, Q340, Q341, Q342, Q343, Q344, Q345, Q346, Q347, Q348, Q349, Q350, Q351, Q352, Q353, Q354, Q355, Q356, Q357, Q358, Q359, Q360, Q361, Q362, Q363, Q364, Q365, Q366, Q367, Q368, Q369, Q370, Q371, Q372, Q373, Q374, Q375, Q376, Q377, Q378, Q379, Q380, Q381, Q382, Q383, Q384, Q385, Q386, Q387, Q388, Q389, Q390, Q391, Q392, Q393, Q394, Q395, Q396, Q397, Q398, Q399, Q400, Q401, Q402, Q403, Q404, Q405, Q406, Q407, Q408, Q409, Q410, Q411, Q412, Q413, Q414, Q415, Q416, Q417, Q418, Q419, Q420, Q421, Q422, Q423, Q424, Q425, Q426, Q427, Q428, Q429, Q430, Q431, Q432, Q433, Q434, Q435, Q436, Q437, Q438, Q439, Q440, Q441, Q442, Q443, Q444, Q445, Q446, Q447, Q448, Q449, Q450, Q451, Q452, Q453, Q454, Q455, Q456, Q457, Q458, Q459, Q460, Q461, Q462, Q463, Q464, Q465, Q466, Q467, Q468, Q469, Q470, Q471, Q472, Q473, Q474, Q475, Q476, Q477, Q478, Q479, Q480, Q481, Q482, Q483, Q484, Q485, Q486, Q487, Q488, Q489, Q490, Q491, Q492, Q493, Q494, Q495, Q496, Q497, Q498, Q499, Q500, Q501, Q502, Q503, Q504, Q505, Q506, Q507, Q508, Q509, Q510, Q511, Q512, Q513]), "depth" : 12.7 * mm});
        }
        {
            var Q0;
            Q0=makeQuery(id+"F1.opExtrude","CAP_FACE",FACE,{"disambiguationData":[OSD([sQuery(id+"F0.wireOp",EDGE,"E0"),sQuery(id+"F0.wireOp",EDGE,"E1.0"),sQuery(id+"F0.wireOp",EDGE,"E2.0.1.0"),sQuery(id+"F0.wireOp",EDGE,"E2.0.1.1"),sQuery(id+"F0.wireOp",EDGE,"E2.0.2.0"),sQuery(id+"F0.wireOp",EDGE,"E2.0.2.1"),sQuery(id+"F0.wireOp",EDGE,"E2.0.3.0"),sQuery(id+"F0.wireOp",EDGE,"E2.0.3.1"),sQuery(id+"F0.wireOp",EDGE,"E2.0.4.0"),sQuery(id+"F0.wireOp",EDGE,"E2.0.4.1"),sQuery(id+"F0.wireOp",EDGE,"E2.0.5.0"),sQuery(id+"F0.wireOp",EDGE,"E2.0.5.1"),sQuery(id+"F0.wireOp",EDGE,"E2.0.6.0"),sQuery(id+"F0.wireOp",EDGE,"E2.0.6.1"),sQuery(id+"F0.wireOp",EDGE,"E2.1.0.0"),sQuery(id+"F0.wireOp",EDGE,"E2.1.0.1"),sQuery(id+"F0.wireOp",EDGE,"E2.1.1.1"),sQuery(id+"F0.wireOp",EDGE,"E2.1.2.1"),sQuery(id+"F0.wireOp",EDGE,"E2.1.3.1"),sQuery(id+"F0.wireOp",EDGE,"E2.1.4.1"),sQuery(id+"F0.wireOp",EDGE,"E2.1.5.1"),sQuery(id+"F0.wireOp",EDGE,"E2.1.6.0"),sQuery(id+"F0.wireOp",EDGE,"E2.1.6.1"),sQuery(id+"F0.wireOp",EDGE,"E2.2.0.0"),sQuery(id+"F0.wireOp",EDGE,"E2.2.0.1"),sQuery(id+"F0.wireOp",EDGE,"E2.2.1.1"),sQuery(id+"F0.wireOp",EDGE,"E2.2.2.1"),sQuery(id+"F0.wireOp",EDGE,"E2.2.3.1"),sQuery(id+"F0.wireOp",EDGE,"E2.2.4.1"),sQuery(id+"F0.wireOp",EDGE,"E2.2.5.1"),sQuery(id+"F0.wireOp",EDGE,"E2.2.6.0"),sQuery(id+"F0.wireOp",EDGE,"E2.2.6.1"),sQuery(id+"F0.wireOp",EDGE,"E2.3.0.0"),sQuery(id+"F0.wireOp",EDGE,"E2.3.0.1"),sQuery(id+"F0.wireOp",EDGE,"E2.3.1.1"),sQuery(id+"F0.wireOp",EDGE,"E2.3.2.1"),sQuery(id+"F0.wireOp",EDGE,"E2.3.3.1"),sQuery(id+"F0.wireOp",EDGE,"E2.3.4.1"),sQuery(id+"F0.wireOp",EDGE,"E2.3.5.1"),sQuery(id+"F0.wireOp",EDGE,"E2.3.6.0"),sQuery(id+"F0.wireOp",EDGE,"E2.3.6.1"),sQuery(id+"F0.wireOp",EDGE,"E2.4.0.0"),sQuery(id+"F0.wireOp",EDGE,"E2.4.0.1"),sQuery(id+"F0.wireOp",EDGE,"E2.4.1.1"),sQuery(id+"F0.wireOp",EDGE,"E2.4.2.1"),sQuery(id+"F0.wireOp",EDGE,"E2.4.3.1"),sQuery(id+"F0.wireOp",EDGE,"E2.4.4.1"),sQuery(id+"F0.wireOp",EDGE,"E2.4.5.1"),sQuery(id+"F0.wireOp",EDGE,"E2.4.6.0"),sQuery(id+"F0.wireOp",EDGE,"E2.4.6.1"),sQuery(id+"F0.wireOp",EDGE,"E2.5.0.0"),sQuery(id+"F0.wireOp",EDGE,"E2.5.0.1"),sQuery(id+"F0.wireOp",EDGE,"E2.5.1.1"),sQuery(id+"F0.wireOp",EDGE,"E2.5.2.1"),sQuery(id+"F0.wireOp",EDGE,"E2.5.3.1"),sQuery(id+"F0.wireOp",EDGE,"E2.5.4.1"),sQuery(id+"F0.wireOp",EDGE,"E2.5.5.1"),sQuery(id+"F0.wireOp",EDGE,"E2.5.6.0"),sQuery(id+"F0.wireOp",EDGE,"E2.5.6.1"),sQuery(id+"F0.wireOp",EDGE,"E2.6.0.0"),sQuery(id+"F0.wireOp",EDGE,"E2.6.0.1"),sQuery(id+"F0.wireOp",EDGE,"E2.6.1.1"),sQuery(id+"F0.wireOp",EDGE,"E2.6.2.1"),sQuery(id+"F0.wireOp",EDGE,"E2.6.3.1"),sQuery(id+"F0.wireOp",EDGE,"E2.6.4.1"),sQuery(id+"F0.wireOp",EDGE,"E2.6.5.1"),sQuery(id+"F0.wireOp",EDGE,"E2.6.6.0"),sQuery(id+"F0.wireOp",EDGE,"E2.6.6.1"),sQuery(id+"F0.wireOp",EDGE,"E2.7.0.0"),sQuery(id+"F0.wireOp",EDGE,"E2.7.0.1"),sQuery(id+"F0.wireOp",EDGE,"E2.7.1.1"),sQuery(id+"F0.wireOp",EDGE,"E2.7.2.1"),sQuery(id+"F0.wireOp",EDGE,"E2.7.3.1"),sQuery(id+"F0.wireOp",EDGE,"E2.7.4.1"),sQuery(id+"F0.wireOp",EDGE,"E2.7.5.1"),sQuery(id+"F0.wireOp",EDGE,"E2.7.6.0"),sQuery(id+"F0.wireOp",EDGE,"E2.7.6.1"),sQuery(id+"F0.wireOp",EDGE,"E2.8.0.0"),sQuery(id+"F0.wireOp",EDGE,"E2.8.0.1"),sQuery(id+"F0.wireOp",EDGE,"E2.8.1.1"),sQuery(id+"F0.wireOp",EDGE,"E2.8.2.1"),sQuery(id+"F0.wireOp",EDGE,"E2.8.3.1"),sQuery(id+"F0.wireOp",EDGE,"E2.8.4.1"),sQuery(id+"F0.wireOp",EDGE,"E2.8.5.1"),sQuery(id+"F0.wireOp",EDGE,"E2.8.6.0"),sQuery(id+"F0.wireOp",EDGE,"E2.8.6.1"),sQuery(id+"F0.wireOp",EDGE,"E2.9.0.0"),sQuery(id+"F0.wireOp",EDGE,"E2.9.0.1"),sQuery(id+"F0.wireOp",EDGE,"E2.9.1.1"),sQuery(id+"F0.wireOp",EDGE,"E2.9.2.1"),sQuery(id+"F0.wireOp",EDGE,"E2.9.3.1"),sQuery(id+"F0.wireOp",EDGE,"E2.9.4.1"),sQuery(id+"F0.wireOp",EDGE,"E2.9.5.1"),sQuery(id+"F0.wireOp",EDGE,"E2.9.6.0"),sQuery(id+"F0.wireOp",EDGE,"E2.9.6.1"),sQuery(id+"F0.wireOp",EDGE,"E2.10.0.0"),sQuery(id+"F0.wireOp",EDGE,"E2.10.0.1"),sQuery(id+"F0.wireOp",EDGE,"E2.10.1.1"),sQuery(id+"F0.wireOp",EDGE,"E2.10.2.1"),sQuery(id+"F0.wireOp",EDGE,"E2.10.3.1"),sQuery(id+"F0.wireOp",EDGE,"E2.10.4.1"),sQuery(id+"F0.wireOp",EDGE,"E2.10.5.1"),sQuery(id+"F0.wireOp",EDGE,"E2.10.6.0"),sQuery(id+"F0.wireOp",EDGE,"E2.10.6.1"),sQuery(id+"F0.wireOp",EDGE,"E2.11.0.0"),sQuery(id+"F0.wireOp",EDGE,"E2.11.0.1"),sQuery(id+"F0.wireOp",EDGE,"E2.11.1.0"),sQuery(id+"F0.wireOp",EDGE,"E2.11.1.1"),sQuery(id+"F0.wireOp",EDGE,"E2.11.2.0"),sQuery(id+"F0.wireOp",EDGE,"E2.11.2.1"),sQuery(id+"F0.wireOp",EDGE,"E2.11.3.0"),sQuery(id+"F0.wireOp",EDGE,"E2.11.3.1"),sQuery(id+"F0.wireOp",EDGE,"E2.11.4.0"),sQuery(id+"F0.wireOp",EDGE,"E2.11.4.1"),sQuery(id+"F0.wireOp",EDGE,"E2.11.5.0"),sQuery(id+"F0.wireOp",EDGE,"E2.11.5.1"),sQuery(id+"F0.wireOp",EDGE,"E2.11.6.0"),sQuery(id+"F0.wireOp",EDGE,"E2.11.6.1")])],"isStart":false});
            var sketch = newSketch(context, id + "F2", { "sketchPlane" : qUnion([Q0])});
            skArc(sketch, "E8.0", {"start": v(-4.7, 10.5) * mm, "mid": v(-8.13, -8.13) * mm, "end": v(10.5, -4.7) * mm});
            skArc(sketch, "E9.0", {"start": v(10.5, 130.7) * mm, "mid": v(-8.13, 134.13) * mm, "end": v(-4.7, 115.5) * mm});
            skArc(sketch, "E10.0", {"start": v(94.5, -4.7) * mm, "mid": v(98.74, -9.65) * mm, "end": v(105, -11.5) * mm});
            skSolve(sketch);
        }
        {
            var Q0;
            Q0=makeQuery(id+"F2.imprint","IMPRINT",FACE,{"disambiguationData":[TD([[makeQuery(id+"F2.imprint","IMPRINT",EDGE,{"derivedFrom":sQuery(id+"F2.wireOp",EDGE,"E8.0")}),1.0]])]});
            var sketch = newSketch(context, id + "F3", { "sketchPlane" : qUnion([Q0])});
            skLineSegment(sketch, "E11", {"start": v(0, 0) * mm, "end": v(-5, 0) * mm, "construction": true});
            skLineSegment(sketch, "E12", {"start": v(-5, 0) * mm, "end": v(-5, -5) * mm, "construction": true});
            skLineSegment(sketch, "E13.bottom", {"start": v(-5, -5) * mm, "end": v(5, -5) * mm});
            skLineSegment(sketch, "E13.top", {"start": v(-5, 120) * mm, "end": v(5, 120) * mm});
            skLineSegment(sketch, "E13.left", {"start": v(-5, -5) * mm, "end": v(-5, 120) * mm});
            skLineSegment(sketch, "E13.right", {"start": v(5, -5) * mm, "end": v(5, 120) * mm});
            skLineSegment(sketch, "E14.1.0.0", {"start": v(15.5, -5) * mm, "end": v(25.5, -5) * mm});
            skLineSegment(sketch, "E14.1.0.1", {"start": v(25.5, -5) * mm, "end": v(25.5, 120) * mm});
            skLineSegment(sketch, "E14.1.0.2", {"start": v(15.5, -5) * mm, "end": v(15.5, 120) * mm});
            skLineSegment(sketch, "E14.1.0.3", {"start": v(15.5, 120) * mm, "end": v(25.5, 120) * mm});
            skLineSegment(sketch, "E14.2.0.0", {"start": v(36, -5) * mm, "end": v(46, -5) * mm});
            skLineSegment(sketch, "E14.2.0.1", {"start": v(46, -5) * mm, "end": v(46, 120) * mm});
            skLineSegment(sketch, "E14.2.0.2", {"start": v(36, -5) * mm, "end": v(36, 120) * mm});
            skLineSegment(sketch, "E14.2.0.3", {"start": v(36, 120) * mm, "end": v(46, 120) * mm});
            skLineSegment(sketch, "E14.3.0.0", {"start": v(56.5, -5) * mm, "end": v(66.5, -5) * mm});
            skLineSegment(sketch, "E14.3.0.1", {"start": v(66.5, -5) * mm, "end": v(66.5, 120) * mm});
            skLineSegment(sketch, "E14.3.0.2", {"start": v(56.5, -5) * mm, "end": v(56.5, 120) * mm});
            skLineSegment(sketch, "E14.3.0.3", {"start": v(56.5, 120) * mm, "end": v(66.5, 120) * mm});
            skLineSegment(sketch, "E14.4.0.0", {"start": v(77, -5) * mm, "end": v(87, -5) * mm});
            skLineSegment(sketch, "E14.4.0.1", {"start": v(87, -5) * mm, "end": v(87, 120) * mm});
            skLineSegment(sketch, "E14.4.0.2", {"start": v(77, -5) * mm, "end": v(77, 120) * mm});
            skLineSegment(sketch, "E14.4.0.3", {"start": v(77, 120) * mm, "end": v(87, 120) * mm});
            skLineSegment(sketch, "E14.5.0.0", {"start": v(97.5, -5) * mm, "end": v(107.5, -5) * mm});
            skLineSegment(sketch, "E14.5.0.1", {"start": v(107.5, -5) * mm, "end": v(107.5, 120) * mm});
            skLineSegment(sketch, "E14.5.0.2", {"start": v(97.5, -5) * mm, "end": v(97.5, 120) * mm});
            skLineSegment(sketch, "E14.5.0.3", {"start": v(97.5, 120) * mm, "end": v(107.5, 120) * mm});
            skLineSegment(sketch, "E14.direction1", {"start": v(-5, -5) * mm, "end": v(15.5, -5) * mm, "construction": true});
            skSolve(sketch);
        }
        {
            var Q0;
            Q0 = qSketchRegion(id + "F3", true);
            extrude(context, id + "F4", {"entities" : qUnion([Q0]), "operationType" : NewBodyOperationType.REMOVE, "oppositeDirection" : true, "depth" : 1 * mm});
        }
        {
            var Q0;
            Q0=makeQuery(id+"F2.imprint","IMPRINT",FACE,{"disambiguationData":[TD([[makeQuery(id+"F2.imprint","IMPRINT",EDGE,{"derivedFrom":sQuery(id+"F2.wireOp",EDGE,"E8.0")}),1.0]])]});
            var sketch = newSketch(context, id + "F5", { "sketchPlane" : qUnion([Q0])});
            skLineSegment(sketch, "E15", {"start": v(0, 0) * mm, "end": v(0, 5) * mm, "construction": true});
            skLineSegment(sketch, "E16", {"start": v(0, 5) * mm, "end": v(-5, 5) * mm, "construction": true});
            skLineSegment(sketch, "E17.bottom", {"start": v(-5, 5) * mm, "end": v(145, 5) * mm});
            skLineSegment(sketch, "E17.top", {"start": v(-5, -5) * mm, "end": v(145, -5) * mm});
            skLineSegment(sketch, "E17.left", {"start": v(-5, 5) * mm, "end": v(-5, -5) * mm});
            skLineSegment(sketch, "E17.right", {"start": v(145, 5) * mm, "end": v(145, -5) * mm});
            skLineSegment(sketch, "E18.0.1.0", {"start": v(-5, 25.5) * mm, "end": v(145, 25.5) * mm});
            skLineSegment(sketch, "E18.0.1.1", {"start": v(-5, 25.5) * mm, "end": v(-5, 15.5) * mm});
            skLineSegment(sketch, "E18.0.1.2", {"start": v(-5, 15.5) * mm, "end": v(145, 15.5) * mm});
            skLineSegment(sketch, "E18.0.1.3", {"start": v(145, 25.5) * mm, "end": v(145, 15.5) * mm});
            skLineSegment(sketch, "E18.0.2.0", {"start": v(-5, 46) * mm, "end": v(145, 46) * mm});
            skLineSegment(sketch, "E18.0.2.1", {"start": v(-5, 46) * mm, "end": v(-5, 36) * mm});
            skLineSegment(sketch, "E18.0.2.2", {"start": v(-5, 36) * mm, "end": v(145, 36) * mm});
            skLineSegment(sketch, "E18.0.2.3", {"start": v(145, 46) * mm, "end": v(145, 36) * mm});
            skLineSegment(sketch, "E18.0.3.0", {"start": v(-5, 66.5) * mm, "end": v(145, 66.5) * mm});
            skLineSegment(sketch, "E18.0.3.1", {"start": v(-5, 66.5) * mm, "end": v(-5, 56.5) * mm});
            skLineSegment(sketch, "E18.0.3.2", {"start": v(-5, 56.5) * mm, "end": v(145, 56.5) * mm});
            skLineSegment(sketch, "E18.0.3.3", {"start": v(145, 66.5) * mm, "end": v(145, 56.5) * mm});
            skLineSegment(sketch, "E18.0.4.0", {"start": v(-5, 87) * mm, "end": v(145, 87) * mm});
            skLineSegment(sketch, "E18.0.4.1", {"start": v(-5, 87) * mm, "end": v(-5, 77) * mm});
            skLineSegment(sketch, "E18.0.4.2", {"start": v(-5, 77) * mm, "end": v(145, 77) * mm});
            skLineSegment(sketch, "E18.0.4.3", {"start": v(145, 87) * mm, "end": v(145, 77) * mm});
            skLineSegment(sketch, "E18.0.5.0", {"start": v(-5, 107.5) * mm, "end": v(145, 107.5) * mm});
            skLineSegment(sketch, "E18.0.5.1", {"start": v(-5, 107.5) * mm, "end": v(-5, 97.5) * mm});
            skLineSegment(sketch, "E18.0.5.2", {"start": v(-5, 97.5) * mm, "end": v(145, 97.5) * mm});
            skLineSegment(sketch, "E18.0.5.3", {"start": v(145, 107.5) * mm, "end": v(145, 97.5) * mm});
            skLineSegment(sketch, "E18.0.6.0", {"start": v(-5, 128) * mm, "end": v(145, 128) * mm});
            skLineSegment(sketch, "E18.0.6.1", {"start": v(-5, 128) * mm, "end": v(-5, 118) * mm});
            skLineSegment(sketch, "E18.0.6.2", {"start": v(-5, 118) * mm, "end": v(145, 118) * mm});
            skLineSegment(sketch, "E18.0.6.3", {"start": v(145, 128) * mm, "end": v(145, 118) * mm});
            skLineSegment(sketch, "E18.direction1", {"start": v(-5, 5) * mm, "end": v(20, 5) * mm, "construction": true});
            skLineSegment(sketch, "E18.direction2", {"start": v(-5, 5) * mm, "end": v(-5, 25.5) * mm, "construction": true});
            skSolve(sketch);
        }
        {
            var Q0;
            Q0 = qSketchRegion(id + "F5", true);
            extrude(context, id + "F6", {"entities" : qUnion([Q0]), "operationType" : NewBodyOperationType.REMOVE, "oppositeDirection" : true, "depth" : 1 * mm});
        }
        {
            var Q0;
            Q0=makeQuery(id+"F1.opExtrude","CAP_EDGE",EDGE,{"disambiguationData":[OSD([sQuery(id+"F0.wireOp",EDGE,"E2.1.0.0")])],"isStart":true});
            var Q1;
            Q1=makeQuery(id+"F1.opExtrude","CAP_EDGE",EDGE,{"disambiguationData":[OSD([sQuery(id+"F0.wireOp",EDGE,"E2.2.0.0")])],"isStart":true});
            var Q2;
            Q2=makeQuery(id+"F1.opExtrude","CAP_EDGE",EDGE,{"disambiguationData":[OSD([sQuery(id+"F0.wireOp",EDGE,"E2.3.0.0")])],"isStart":true});
            var Q3;
            Q3=makeQuery(id+"F1.opExtrude","CAP_EDGE",EDGE,{"disambiguationData":[OSD([sQuery(id+"F0.wireOp",EDGE,"E2.4.0.0")])],"isStart":true});
            var Q4;
            Q4=makeQuery(id+"F1.opExtrude","CAP_EDGE",EDGE,{"disambiguationData":[OSD([sQuery(id+"F0.wireOp",EDGE,"E2.5.0.0")])],"isStart":true});
            var Q5;
            Q5=makeQuery(id+"F1.opExtrude","CAP_EDGE",EDGE,{"disambiguationData":[OSD([sQuery(id+"F0.wireOp",EDGE,"E4")])],"isStart":true});
            var Q6;
            Q6=makeQuery(id+"F1.opExtrude","CAP_EDGE",EDGE,{"disambiguationData":[OSD([sQuery(id+"F0.wireOp",EDGE,"E1.0")])],"isStart":true});
            var Q7;
            Q7=makeQuery(id+"F1.opExtrude","CAP_EDGE",EDGE,{"disambiguationData":[OSD([sQuery(id+"F0.wireOp",EDGE,"E2.0.1.0")])],"isStart":true});
            var Q8;
            Q8=makeQuery(id+"F1.opExtrude","CAP_EDGE",EDGE,{"disambiguationData":[OSD([sQuery(id+"F0.wireOp",EDGE,"E2.0.2.0")])],"isStart":true});
            var Q9;
            Q9=makeQuery(id+"F1.opExtrude","CAP_EDGE",EDGE,{"disambiguationData":[OSD([sQuery(id+"F0.wireOp",EDGE,"E2.0.3.0")])],"isStart":true});
            var Q10;
            Q10=makeQuery(id+"F1.opExtrude","CAP_EDGE",EDGE,{"disambiguationData":[OSD([sQuery(id+"F0.wireOp",EDGE,"E2.0.4.0")])],"isStart":true});
            var Q11;
            Q11=makeQuery(id+"F1.opExtrude","CAP_EDGE",EDGE,{"disambiguationData":[OSD([sQuery(id+"F0.wireOp",EDGE,"E2.0.5.0")])],"isStart":true});
            var Q12;
            Q12=makeQuery(id+"F1.opExtrude","CAP_EDGE",EDGE,{"disambiguationData":[OSD([sQuery(id+"F0.wireOp",EDGE,"E2.0.6.0")])],"isStart":true});
            var Q13;
            Q13=makeQuery(id+"F1.opExtrude","CAP_EDGE",EDGE,{"disambiguationData":[OSD([sQuery(id+"F0.wireOp",EDGE,"E2.1.6.0")])],"isStart":true});
            var Q14;
            Q14=makeQuery(id+"F1.opExtrude","CAP_EDGE",EDGE,{"disambiguationData":[OSD([sQuery(id+"F0.wireOp",EDGE,"E2.2.6.0")])],"isStart":true});
            var Q15;
            Q15=makeQuery(id+"F1.opExtrude","CAP_EDGE",EDGE,{"disambiguationData":[OSD([sQuery(id+"F0.wireOp",EDGE,"E2.3.6.0")])],"isStart":true});
            var Q16;
            Q16=makeQuery(id+"F1.opExtrude","CAP_EDGE",EDGE,{"disambiguationData":[OSD([sQuery(id+"F0.wireOp",EDGE,"E2.4.6.0")])],"isStart":true});
            var Q17;
            Q17=makeQuery(id+"F1.opExtrude","CAP_EDGE",EDGE,{"disambiguationData":[OSD([sQuery(id+"F0.wireOp",EDGE,"E2.5.6.0")])],"isStart":true});
            var Q18;
            Q18=makeQuery(id+"F1.opExtrude","CAP_EDGE",EDGE,{"disambiguationData":[OSD([sQuery(id+"F0.wireOp",EDGE,"E6")])],"isStart":true});
            var Q19;
            Q19=makeQuery(id+"F1.opExtrude","CAP_EDGE",EDGE,{"disambiguationData":[OSD([sQuery(id+"F0.wireOp",EDGE,"E7")])],"isStart":true});
            var Q20;
            Q20=makeQuery(id+"F1.opExtrude","CAP_EDGE",EDGE,{"disambiguationData":[OSD([sQuery(id+"F0.wireOp",EDGE,"E2.5.0.1")])],"isStart":true});
            var Q21;
            Q21=makeQuery(id+"F1.opExtrude","CAP_EDGE",EDGE,{"disambiguationData":[OSD([sQuery(id+"F0.wireOp",EDGE,"E2.5.1.1")])],"isStart":true});
            var Q22;
            Q22=makeQuery(id+"F1.opExtrude","CAP_EDGE",EDGE,{"disambiguationData":[OSD([sQuery(id+"F0.wireOp",EDGE,"E2.5.2.1")])],"isStart":true});
            var Q23;
            Q23=makeQuery(id+"F1.opExtrude","CAP_EDGE",EDGE,{"disambiguationData":[OSD([sQuery(id+"F0.wireOp",EDGE,"E2.5.3.1")])],"isStart":true});
            var Q24;
            Q24=makeQuery(id+"F1.opExtrude","CAP_EDGE",EDGE,{"disambiguationData":[OSD([sQuery(id+"F0.wireOp",EDGE,"E2.5.4.1")])],"isStart":true});
            var Q25;
            Q25=makeQuery(id+"F1.opExtrude","CAP_EDGE",EDGE,{"disambiguationData":[OSD([sQuery(id+"F0.wireOp",EDGE,"E2.5.5.1")])],"isStart":true});
            var Q26;
            Q26=makeQuery(id+"F1.opExtrude","CAP_EDGE",EDGE,{"disambiguationData":[OSD([sQuery(id+"F0.wireOp",EDGE,"E2.5.6.1")])],"isStart":true});
            var Q27;
            Q27=makeQuery(id+"F1.opExtrude","CAP_EDGE",EDGE,{"disambiguationData":[OSD([sQuery(id+"F0.wireOp",EDGE,"E2.4.6.1")])],"isStart":true});
            var Q28;
            Q28=makeQuery(id+"F1.opExtrude","CAP_EDGE",EDGE,{"disambiguationData":[OSD([sQuery(id+"F0.wireOp",EDGE,"E2.4.5.1")])],"isStart":true});
            var Q29;
            Q29=makeQuery(id+"F1.opExtrude","CAP_EDGE",EDGE,{"disambiguationData":[OSD([sQuery(id+"F0.wireOp",EDGE,"E2.4.4.1")])],"isStart":true});
            var Q30;
            Q30=makeQuery(id+"F1.opExtrude","CAP_EDGE",EDGE,{"disambiguationData":[OSD([sQuery(id+"F0.wireOp",EDGE,"E2.4.3.1")])],"isStart":true});
            var Q31;
            Q31=makeQuery(id+"F1.opExtrude","CAP_EDGE",EDGE,{"disambiguationData":[OSD([sQuery(id+"F0.wireOp",EDGE,"E2.4.2.1")])],"isStart":true});
            var Q32;
            Q32=makeQuery(id+"F1.opExtrude","CAP_EDGE",EDGE,{"disambiguationData":[OSD([sQuery(id+"F0.wireOp",EDGE,"E2.4.1.1")])],"isStart":true});
            var Q33;
            Q33=makeQuery(id+"F1.opExtrude","CAP_EDGE",EDGE,{"disambiguationData":[OSD([sQuery(id+"F0.wireOp",EDGE,"E2.4.0.1")])],"isStart":true});
            var Q34;
            Q34=makeQuery(id+"F1.opExtrude","CAP_EDGE",EDGE,{"disambiguationData":[OSD([sQuery(id+"F0.wireOp",EDGE,"E2.3.0.1")])],"isStart":true});
            var Q35;
            Q35=makeQuery(id+"F1.opExtrude","CAP_EDGE",EDGE,{"disambiguationData":[OSD([sQuery(id+"F0.wireOp",EDGE,"E2.3.1.1")])],"isStart":true});
            var Q36;
            Q36=makeQuery(id+"F1.opExtrude","CAP_EDGE",EDGE,{"disambiguationData":[OSD([sQuery(id+"F0.wireOp",EDGE,"E2.3.2.1")])],"isStart":true});
            var Q37;
            Q37=makeQuery(id+"F1.opExtrude","CAP_EDGE",EDGE,{"disambiguationData":[OSD([sQuery(id+"F0.wireOp",EDGE,"E2.3.3.1")])],"isStart":true});
            var Q38;
            Q38=makeQuery(id+"F1.opExtrude","CAP_EDGE",EDGE,{"disambiguationData":[OSD([sQuery(id+"F0.wireOp",EDGE,"E2.3.4.1")])],"isStart":true});
            var Q39;
            Q39=makeQuery(id+"F1.opExtrude","CAP_EDGE",EDGE,{"disambiguationData":[OSD([sQuery(id+"F0.wireOp",EDGE,"E2.3.5.1")])],"isStart":true});
            var Q40;
            Q40=makeQuery(id+"F1.opExtrude","CAP_EDGE",EDGE,{"disambiguationData":[OSD([sQuery(id+"F0.wireOp",EDGE,"E2.3.6.1")])],"isStart":true});
            var Q41;
            Q41=makeQuery(id+"F1.opExtrude","CAP_EDGE",EDGE,{"disambiguationData":[OSD([sQuery(id+"F0.wireOp",EDGE,"E2.2.6.1")])],"isStart":true});
            var Q42;
            Q42=makeQuery(id+"F1.opExtrude","CAP_EDGE",EDGE,{"disambiguationData":[OSD([sQuery(id+"F0.wireOp",EDGE,"E2.2.5.1")])],"isStart":true});
            var Q43;
            Q43=makeQuery(id+"F1.opExtrude","CAP_EDGE",EDGE,{"disambiguationData":[OSD([sQuery(id+"F0.wireOp",EDGE,"E2.2.4.1")])],"isStart":true});
            var Q44;
            Q44=makeQuery(id+"F1.opExtrude","CAP_EDGE",EDGE,{"disambiguationData":[OSD([sQuery(id+"F0.wireOp",EDGE,"E2.2.3.1")])],"isStart":true});
            var Q45;
            Q45=makeQuery(id+"F1.opExtrude","CAP_EDGE",EDGE,{"disambiguationData":[OSD([sQuery(id+"F0.wireOp",EDGE,"E2.2.2.1")])],"isStart":true});
            var Q46;
            Q46=makeQuery(id+"F1.opExtrude","CAP_EDGE",EDGE,{"disambiguationData":[OSD([sQuery(id+"F0.wireOp",EDGE,"E2.2.1.1")])],"isStart":true});
            var Q47;
            Q47=makeQuery(id+"F1.opExtrude","CAP_EDGE",EDGE,{"disambiguationData":[OSD([sQuery(id+"F0.wireOp",EDGE,"E2.2.0.1")])],"isStart":true});
            var Q48;
            Q48=makeQuery(id+"F1.opExtrude","CAP_EDGE",EDGE,{"disambiguationData":[OSD([sQuery(id+"F0.wireOp",EDGE,"E2.1.0.1")])],"isStart":true});
            var Q49;
            Q49=makeQuery(id+"F1.opExtrude","CAP_EDGE",EDGE,{"disambiguationData":[OSD([sQuery(id+"F0.wireOp",EDGE,"E2.1.1.1")])],"isStart":true});
            var Q50;
            Q50=makeQuery(id+"F1.opExtrude","CAP_EDGE",EDGE,{"disambiguationData":[OSD([sQuery(id+"F0.wireOp",EDGE,"E2.1.2.1")])],"isStart":true});
            var Q51;
            Q51=makeQuery(id+"F1.opExtrude","CAP_EDGE",EDGE,{"disambiguationData":[OSD([sQuery(id+"F0.wireOp",EDGE,"E2.1.3.1")])],"isStart":true});
            var Q52;
            Q52=makeQuery(id+"F1.opExtrude","CAP_EDGE",EDGE,{"disambiguationData":[OSD([sQuery(id+"F0.wireOp",EDGE,"E2.1.4.1")])],"isStart":true});
            var Q53;
            Q53=makeQuery(id+"F1.opExtrude","CAP_EDGE",EDGE,{"disambiguationData":[OSD([sQuery(id+"F0.wireOp",EDGE,"E2.1.5.1")])],"isStart":true});
            var Q54;
            Q54=makeQuery(id+"F1.opExtrude","CAP_EDGE",EDGE,{"disambiguationData":[OSD([sQuery(id+"F0.wireOp",EDGE,"E2.1.6.1")])],"isStart":true});
            var Q55;
            Q55=makeQuery(id+"F1.opExtrude","CAP_EDGE",EDGE,{"disambiguationData":[OSD([sQuery(id+"F0.wireOp",EDGE,"E2.0.6.1")])],"isStart":true});
            var Q56;
            Q56=makeQuery(id+"F1.opExtrude","CAP_EDGE",EDGE,{"disambiguationData":[OSD([sQuery(id+"F0.wireOp",EDGE,"E2.0.5.1")])],"isStart":true});
            var Q57;
            Q57=makeQuery(id+"F1.opExtrude","CAP_EDGE",EDGE,{"disambiguationData":[OSD([sQuery(id+"F0.wireOp",EDGE,"E2.0.4.1")])],"isStart":true});
            var Q58;
            Q58=makeQuery(id+"F1.opExtrude","CAP_EDGE",EDGE,{"disambiguationData":[OSD([sQuery(id+"F0.wireOp",EDGE,"E2.0.3.1")])],"isStart":true});
            var Q59;
            Q59=makeQuery(id+"F1.opExtrude","CAP_EDGE",EDGE,{"disambiguationData":[OSD([sQuery(id+"F0.wireOp",EDGE,"E2.0.2.1")])],"isStart":true});
            var Q60;
            Q60=makeQuery(id+"F1.opExtrude","CAP_EDGE",EDGE,{"disambiguationData":[OSD([sQuery(id+"F0.wireOp",EDGE,"E2.0.1.1")])],"isStart":true});
            var Q61;
            Q61=makeQuery(id+"F1.opExtrude","CAP_EDGE",EDGE,{"disambiguationData":[OSD([sQuery(id+"F0.wireOp",EDGE,"E0")])],"isStart":true});
            chamfer(context, id + "F7", {"entities" : qUnion([Q0, Q1, Q2, Q3, Q4, Q5, Q6, Q7, Q8, Q9, Q10, Q11, Q12, Q13, Q14, Q15, Q16, Q17, Q18, Q19, Q20, Q21, Q22, Q23, Q24, Q25, Q26, Q27, Q28, Q29, Q30, Q31, Q32, Q33, Q34, Q35, Q36, Q37, Q38, Q39, Q40, Q41, Q42, Q43, Q44, Q45, Q46, Q47, Q48, Q49, Q50, Q51, Q52, Q53, Q54, Q55, Q56, Q57, Q58, Q59, Q60, Q61]), "width" : 0.5 * mm, "tangentPropagation" : true});
        }
    });
